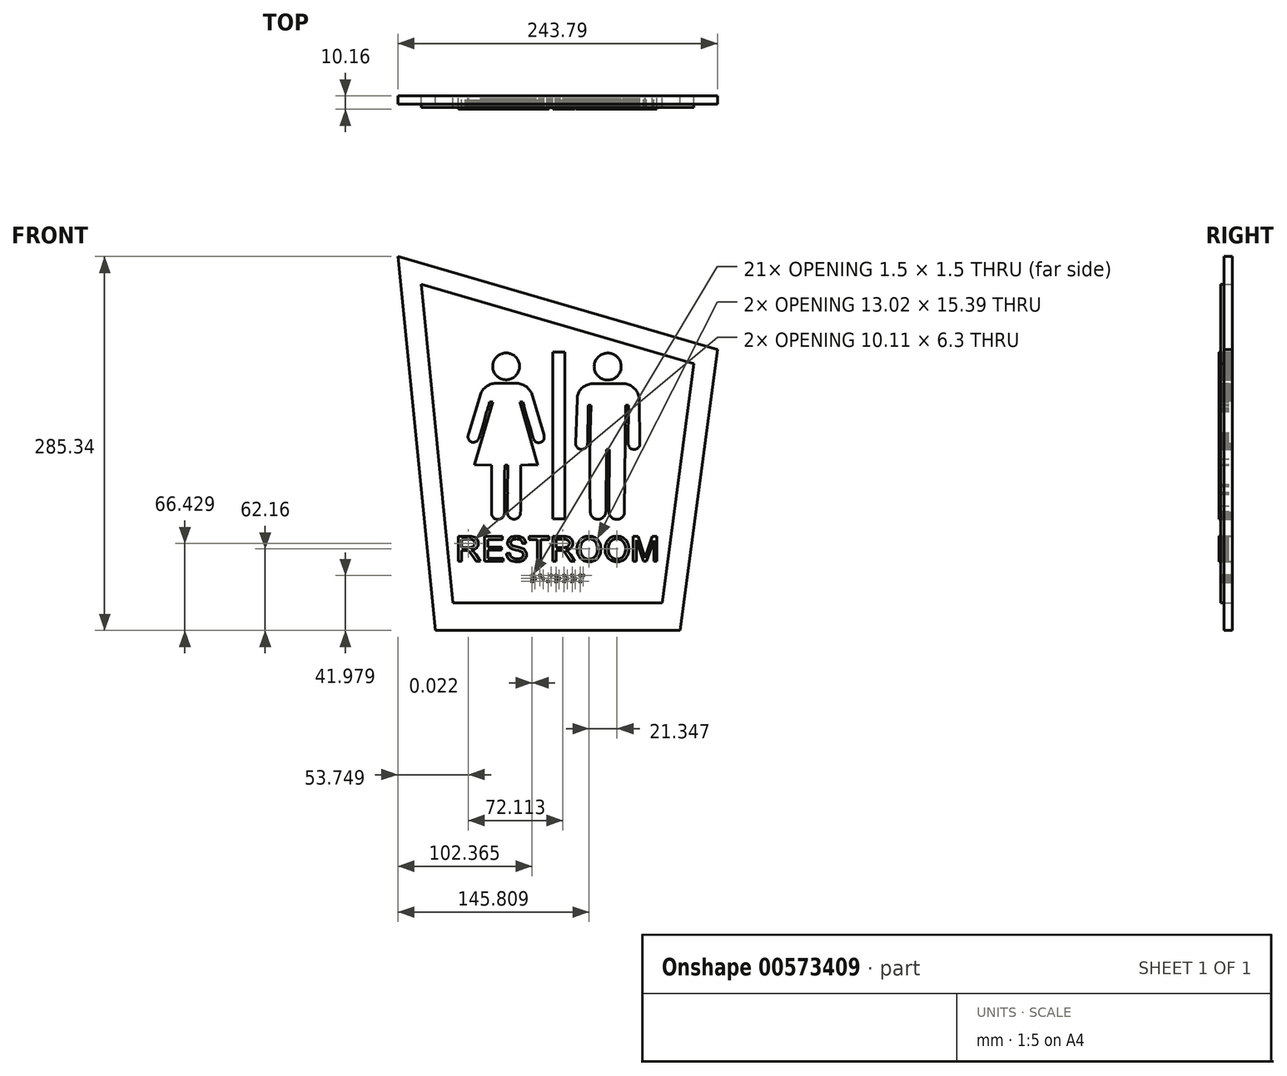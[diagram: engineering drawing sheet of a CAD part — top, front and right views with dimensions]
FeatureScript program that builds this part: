
annotation { "Feature Type Name" : "Feature", "Feature Type Description" : "" }
export const myFeature = defineFeature(function(context is Context, id is Id, definition is map)
    precondition{}
    {
        {
            var Q0;
            Q0=qCreatedBy(makeId("Front.planeOp"),FACE);
            var sketch = newSketch(context, id + "F0", { "sketchPlane" : qUnion([Q0])});
            skLineSegment(sketch, "E0", {"start": v(-172.43, -33.74) * mm, "end": v(-163.18, -33.74) * mm});
            skLineSegment(sketch, "E1", {"start": v(-163.18, -33.74) * mm, "end": v(-163.18, 93.38) * mm});
            skLineSegment(sketch, "E2", {"start": v(-163.18, 93.38) * mm, "end": v(-172.43, 93.38) * mm});
            skLineSegment(sketch, "E3", {"start": v(-172.43, 93.38) * mm, "end": v(-172.43, -33.74) * mm});
            skLineSegment(sketch, "E4", {"start": v(-119.78, 69.44) * mm, "end": v(-142.07, 69.36) * mm});
            skLineSegment(sketch, "E5", {"start": v(-142.07, 69.36) * mm, "end": v(-143.08, 69.24) * mm});
            skLineSegment(sketch, "E6", {"start": v(-143.08, 69.24) * mm, "end": v(-144.08, 69.04) * mm});
            skLineSegment(sketch, "E7", {"start": v(-144.08, 69.04) * mm, "end": v(-145.06, 68.76) * mm});
            skLineSegment(sketch, "E8", {"start": v(-145.06, 68.76) * mm, "end": v(-146.02, 68.41) * mm});
            skLineSegment(sketch, "E9", {"start": v(-146.02, 68.41) * mm, "end": v(-146.95, 68) * mm});
            skLineSegment(sketch, "E10", {"start": v(-146.95, 68) * mm, "end": v(-147.85, 67.5) * mm});
            skLineSegment(sketch, "E11", {"start": v(-147.85, 67.5) * mm, "end": v(-148.7, 66.95) * mm});
            skLineSegment(sketch, "E12", {"start": v(-148.7, 66.95) * mm, "end": v(-149.52, 66.33) * mm});
            skLineSegment(sketch, "E13", {"start": v(-149.52, 66.33) * mm, "end": v(-150.28, 65.66) * mm});
            skLineSegment(sketch, "E14", {"start": v(-150.28, 65.66) * mm, "end": v(-151, 64.92) * mm});
            skLineSegment(sketch, "E15", {"start": v(-151, 64.92) * mm, "end": v(-151.65, 64.14) * mm});
            skLineSegment(sketch, "E16", {"start": v(-151.65, 64.14) * mm, "end": v(-152.25, 63.31) * mm});
            skLineSegment(sketch, "E17", {"start": v(-152.25, 63.31) * mm, "end": v(-152.65, 62.43) * mm});
            skLineSegment(sketch, "E18", {"start": v(-152.65, 62.43) * mm, "end": v(-152.99, 61.51) * mm});
            skLineSegment(sketch, "E19", {"start": v(-152.99, 61.51) * mm, "end": v(-153.26, 60.57) * mm});
            skLineSegment(sketch, "E20", {"start": v(-153.26, 60.57) * mm, "end": v(-153.46, 59.62) * mm});
            skLineSegment(sketch, "E21", {"start": v(-153.46, 59.62) * mm, "end": v(-153.6, 58.65) * mm});
            skLineSegment(sketch, "E22", {"start": v(-153.6, 58.65) * mm, "end": v(-153.65, 57.68) * mm});
            skLineSegment(sketch, "E23", {"start": v(-153.65, 57.68) * mm, "end": v(-154.88, 23.77) * mm});
            skLineSegment(sketch, "E24", {"start": v(-154.88, 23.77) * mm, "end": v(-154.84, 23.18) * mm});
            skLineSegment(sketch, "E25", {"start": v(-154.84, 23.18) * mm, "end": v(-154.73, 22.59) * mm});
            skLineSegment(sketch, "E26", {"start": v(-154.73, 22.59) * mm, "end": v(-154.54, 22.02) * mm});
            skLineSegment(sketch, "E27", {"start": v(-154.54, 22.02) * mm, "end": v(-154.28, 21.48) * mm});
            skLineSegment(sketch, "E28", {"start": v(-154.28, 21.48) * mm, "end": v(-153.95, 20.98) * mm});
            skLineSegment(sketch, "E29", {"start": v(-153.95, 20.98) * mm, "end": v(-153.56, 20.53) * mm});
            skLineSegment(sketch, "E30", {"start": v(-153.56, 20.53) * mm, "end": v(-153.11, 20.14) * mm});
            skLineSegment(sketch, "E31", {"start": v(-153.11, 20.14) * mm, "end": v(-152.61, 19.8) * mm});
            skLineSegment(sketch, "E32", {"start": v(-152.61, 19.8) * mm, "end": v(-152.08, 19.54) * mm});
            skLineSegment(sketch, "E33", {"start": v(-152.08, 19.54) * mm, "end": v(-151.51, 19.34) * mm});
            skLineSegment(sketch, "E34", {"start": v(-151.51, 19.34) * mm, "end": v(-150.93, 19.22) * mm});
            skLineSegment(sketch, "E35", {"start": v(-150.93, 19.22) * mm, "end": v(-150.33, 19.18) * mm});
            skLineSegment(sketch, "E36", {"start": v(-150.33, 19.18) * mm, "end": v(-149.73, 19.22) * mm});
            skLineSegment(sketch, "E37", {"start": v(-149.73, 19.22) * mm, "end": v(-149.15, 19.33) * mm});
            skLineSegment(sketch, "E38", {"start": v(-149.15, 19.33) * mm, "end": v(-148.58, 19.53) * mm});
            skLineSegment(sketch, "E39", {"start": v(-148.58, 19.53) * mm, "end": v(-148.04, 19.8) * mm});
            skLineSegment(sketch, "E40", {"start": v(-148.04, 19.8) * mm, "end": v(-147.54, 20.12) * mm});
            skLineSegment(sketch, "E41", {"start": v(-147.54, 20.12) * mm, "end": v(-147.1, 20.52) * mm});
            skLineSegment(sketch, "E42", {"start": v(-147.1, 20.52) * mm, "end": v(-146.7, 20.97) * mm});
            skLineSegment(sketch, "E43", {"start": v(-146.7, 20.97) * mm, "end": v(-146.37, 21.46) * mm});
            skLineSegment(sketch, "E44", {"start": v(-146.37, 21.46) * mm, "end": v(-146.1, 22) * mm});
            skLineSegment(sketch, "E45", {"start": v(-146.1, 22) * mm, "end": v(-145.91, 22.57) * mm});
            skLineSegment(sketch, "E46", {"start": v(-145.91, 22.57) * mm, "end": v(-145.8, 23.16) * mm});
            skLineSegment(sketch, "E47", {"start": v(-145.8, 23.16) * mm, "end": v(-145.76, 23.75) * mm});
            skLineSegment(sketch, "E48", {"start": v(-145.76, 23.75) * mm, "end": v(-145.43, 52.87) * mm});
            skLineSegment(sketch, "E49", {"start": v(-145.43, 52.87) * mm, "end": v(-143.25, 52.85) * mm});
            skLineSegment(sketch, "E50", {"start": v(-143.25, 52.85) * mm, "end": v(-143.72, 32.37) * mm});
            skLineSegment(sketch, "E51", {"start": v(-143.72, 32.37) * mm, "end": v(-143.99, 11.9) * mm});
            skLineSegment(sketch, "E52", {"start": v(-143.99, 11.9) * mm, "end": v(-143.93, -8.58) * mm});
            skLineSegment(sketch, "E53", {"start": v(-143.93, -8.58) * mm, "end": v(-143.66, -29.05) * mm});
            skLineSegment(sketch, "E54", {"start": v(-143.66, -29.05) * mm, "end": v(-143.56, -29.71) * mm});
            skLineSegment(sketch, "E55", {"start": v(-143.56, -29.71) * mm, "end": v(-143.37, -30.35) * mm});
            skLineSegment(sketch, "E56", {"start": v(-143.37, -30.35) * mm, "end": v(-143.12, -30.97) * mm});
            skLineSegment(sketch, "E57", {"start": v(-143.12, -30.97) * mm, "end": v(-142.8, -31.56) * mm});
            skLineSegment(sketch, "E58", {"start": v(-142.8, -31.56) * mm, "end": v(-142.4, -32.1) * mm});
            skLineSegment(sketch, "E59", {"start": v(-142.4, -32.1) * mm, "end": v(-141.96, -32.6) * mm});
            skLineSegment(sketch, "E60", {"start": v(-141.96, -32.6) * mm, "end": v(-141.46, -33.04) * mm});
            skLineSegment(sketch, "E61", {"start": v(-141.46, -33.04) * mm, "end": v(-140.92, -33.43) * mm});
            skLineSegment(sketch, "E62", {"start": v(-140.92, -33.43) * mm, "end": v(-140.33, -33.75) * mm});
            skLineSegment(sketch, "E63", {"start": v(-140.33, -33.75) * mm, "end": v(-139.71, -34) * mm});
            skLineSegment(sketch, "E64", {"start": v(-139.71, -34) * mm, "end": v(-139.07, -34.18) * mm});
            skLineSegment(sketch, "E65", {"start": v(-139.07, -34.18) * mm, "end": v(-138.4, -34.3) * mm});
            skLineSegment(sketch, "E66", {"start": v(-138.4, -34.3) * mm, "end": v(-137.74, -34.32) * mm});
            skLineSegment(sketch, "E67", {"start": v(-137.74, -34.32) * mm, "end": v(-137.07, -34.28) * mm});
            skLineSegment(sketch, "E68", {"start": v(-137.07, -34.28) * mm, "end": v(-136.42, -34.16) * mm});
            skLineSegment(sketch, "E69", {"start": v(-136.42, -34.16) * mm, "end": v(-135.78, -33.97) * mm});
            skLineSegment(sketch, "E70", {"start": v(-135.78, -33.97) * mm, "end": v(-135.16, -33.7) * mm});
            skLineSegment(sketch, "E71", {"start": v(-135.16, -33.7) * mm, "end": v(-134.58, -33.38) * mm});
            skLineSegment(sketch, "E72", {"start": v(-134.58, -33.38) * mm, "end": v(-134.04, -32.98) * mm});
            skLineSegment(sketch, "E73", {"start": v(-134.04, -32.98) * mm, "end": v(-133.55, -32.53) * mm});
            skLineSegment(sketch, "E74", {"start": v(-133.55, -32.53) * mm, "end": v(-133.11, -32.03) * mm});
            skLineSegment(sketch, "E75", {"start": v(-133.11, -32.03) * mm, "end": v(-132.73, -31.48) * mm});
            skLineSegment(sketch, "E76", {"start": v(-132.73, -31.48) * mm, "end": v(-132.42, -30.89) * mm});
            skLineSegment(sketch, "E77", {"start": v(-132.42, -30.89) * mm, "end": v(-132.18, -30.26) * mm});
            skLineSegment(sketch, "E78", {"start": v(-132.18, -30.26) * mm, "end": v(-132, -29.62) * mm});
            skLineSegment(sketch, "E79", {"start": v(-132, -29.62) * mm, "end": v(-131.9, -28.96) * mm});
            skLineSegment(sketch, "E80", {"start": v(-131.9, -28.96) * mm, "end": v(-131.8, -28.12) * mm});
            skLineSegment(sketch, "E81", {"start": v(-131.8, -28.12) * mm, "end": v(-131.31, 19.01) * mm});
            skLineSegment(sketch, "E82", {"start": v(-131.31, 19.01) * mm, "end": v(-129.15, 19) * mm});
            skLineSegment(sketch, "E83", {"start": v(-129.15, 19) * mm, "end": v(-129.56, -24.14) * mm});
            skLineSegment(sketch, "E84", {"start": v(-129.56, -24.14) * mm, "end": v(-129.37, -29.3) * mm});
            skLineSegment(sketch, "E85", {"start": v(-129.37, -29.3) * mm, "end": v(-129.23, -29.95) * mm});
            skLineSegment(sketch, "E86", {"start": v(-129.23, -29.95) * mm, "end": v(-129.02, -30.58) * mm});
            skLineSegment(sketch, "E87", {"start": v(-129.02, -30.58) * mm, "end": v(-128.73, -31.18) * mm});
            skLineSegment(sketch, "E88", {"start": v(-128.73, -31.18) * mm, "end": v(-128.38, -31.75) * mm});
            skLineSegment(sketch, "E89", {"start": v(-128.38, -31.75) * mm, "end": v(-127.97, -32.27) * mm});
            skLineSegment(sketch, "E90", {"start": v(-127.97, -32.27) * mm, "end": v(-127.5, -32.75) * mm});
            skLineSegment(sketch, "E91", {"start": v(-127.5, -32.75) * mm, "end": v(-126.99, -33.17) * mm});
            skLineSegment(sketch, "E92", {"start": v(-126.99, -33.17) * mm, "end": v(-126.43, -33.52) * mm});
            skLineSegment(sketch, "E93", {"start": v(-126.43, -33.52) * mm, "end": v(-125.83, -33.82) * mm});
            skLineSegment(sketch, "E94", {"start": v(-125.83, -33.82) * mm, "end": v(-125.2, -34.05) * mm});
            skLineSegment(sketch, "E95", {"start": v(-125.2, -34.05) * mm, "end": v(-124.56, -34.2) * mm});
            skLineSegment(sketch, "E96", {"start": v(-124.56, -34.2) * mm, "end": v(-123.9, -34.28) * mm});
            skLineSegment(sketch, "E97", {"start": v(-123.9, -34.28) * mm, "end": v(-123.23, -34.29) * mm});
            skLineSegment(sketch, "E98", {"start": v(-123.23, -34.29) * mm, "end": v(-122.57, -34.22) * mm});
            skLineSegment(sketch, "E99", {"start": v(-122.57, -34.22) * mm, "end": v(-121.92, -34.08) * mm});
            skLineSegment(sketch, "E100", {"start": v(-121.92, -34.08) * mm, "end": v(-121.3, -33.87) * mm});
            skLineSegment(sketch, "E101", {"start": v(-121.3, -33.87) * mm, "end": v(-120.69, -33.59) * mm});
            skLineSegment(sketch, "E102", {"start": v(-120.69, -33.59) * mm, "end": v(-120.12, -33.24) * mm});
            skLineSegment(sketch, "E103", {"start": v(-120.12, -33.24) * mm, "end": v(-119.6, -32.83) * mm});
            skLineSegment(sketch, "E104", {"start": v(-119.6, -32.83) * mm, "end": v(-119.12, -32.37) * mm});
            skLineSegment(sketch, "E105", {"start": v(-119.12, -32.37) * mm, "end": v(-118.7, -31.85) * mm});
            skLineSegment(sketch, "E106", {"start": v(-118.7, -31.85) * mm, "end": v(-118.33, -31.3) * mm});
            skLineSegment(sketch, "E107", {"start": v(-118.33, -31.3) * mm, "end": v(-118.04, -30.7) * mm});
            skLineSegment(sketch, "E108", {"start": v(-118.04, -30.7) * mm, "end": v(-117.8, -30.07) * mm});
            skLineSegment(sketch, "E109", {"start": v(-117.8, -30.07) * mm, "end": v(-117.65, -29.43) * mm});
            skLineSegment(sketch, "E110", {"start": v(-117.65, -29.43) * mm, "end": v(-117.57, -28.77) * mm});
            skLineSegment(sketch, "E111", {"start": v(-117.57, -28.77) * mm, "end": v(-117.56, -28.1) * mm});
            skLineSegment(sketch, "E112", {"start": v(-117.56, -28.1) * mm, "end": v(-116.87, 52.77) * mm});
            skLineSegment(sketch, "E113", {"start": v(-116.87, 52.77) * mm, "end": v(-114.63, 52.77) * mm});
            skLineSegment(sketch, "E114", {"start": v(-114.63, 52.77) * mm, "end": v(-114.74, 23.45) * mm});
            skLineSegment(sketch, "E115", {"start": v(-114.74, 23.45) * mm, "end": v(-114.72, 23.1) * mm});
            skLineSegment(sketch, "E116", {"start": v(-114.72, 23.1) * mm, "end": v(-114.67, 22.74) * mm});
            skLineSegment(sketch, "E117", {"start": v(-114.67, 22.74) * mm, "end": v(-114.54, 22.17) * mm});
            skLineSegment(sketch, "E118", {"start": v(-114.54, 22.17) * mm, "end": v(-114.33, 21.63) * mm});
            skLineSegment(sketch, "E119", {"start": v(-114.33, 21.63) * mm, "end": v(-114.04, 21.11) * mm});
            skLineSegment(sketch, "E120", {"start": v(-114.04, 21.11) * mm, "end": v(-113.7, 20.64) * mm});
            skLineSegment(sketch, "E121", {"start": v(-113.7, 20.64) * mm, "end": v(-113.3, 20.22) * mm});
            skLineSegment(sketch, "E122", {"start": v(-113.3, 20.22) * mm, "end": v(-112.84, 19.85) * mm});
            skLineSegment(sketch, "E123", {"start": v(-112.84, 19.85) * mm, "end": v(-112.33, 19.55) * mm});
            skLineSegment(sketch, "E124", {"start": v(-112.33, 19.55) * mm, "end": v(-111.8, 19.31) * mm});
            skLineSegment(sketch, "E125", {"start": v(-111.8, 19.31) * mm, "end": v(-111.24, 19.15) * mm});
            skLineSegment(sketch, "E126", {"start": v(-111.24, 19.15) * mm, "end": v(-110.66, 19.06) * mm});
            skLineSegment(sketch, "E127", {"start": v(-110.66, 19.06) * mm, "end": v(-110.07, 19.05) * mm});
            skLineSegment(sketch, "E128", {"start": v(-110.07, 19.05) * mm, "end": v(-109.49, 19.12) * mm});
            skLineSegment(sketch, "E129", {"start": v(-109.49, 19.12) * mm, "end": v(-108.92, 19.26) * mm});
            skLineSegment(sketch, "E130", {"start": v(-108.92, 19.26) * mm, "end": v(-108.37, 19.48) * mm});
            skLineSegment(sketch, "E131", {"start": v(-108.37, 19.48) * mm, "end": v(-107.86, 19.76) * mm});
            skLineSegment(sketch, "E132", {"start": v(-107.86, 19.76) * mm, "end": v(-107.4, 20.11) * mm});
            skLineSegment(sketch, "E133", {"start": v(-107.4, 20.11) * mm, "end": v(-106.97, 20.52) * mm});
            skLineSegment(sketch, "E134", {"start": v(-106.97, 20.52) * mm, "end": v(-106.61, 20.98) * mm});
            skLineSegment(sketch, "E135", {"start": v(-106.61, 20.98) * mm, "end": v(-106.31, 21.48) * mm});
            skLineSegment(sketch, "E136", {"start": v(-106.31, 21.48) * mm, "end": v(-106.08, 22.02) * mm});
            skLineSegment(sketch, "E137", {"start": v(-106.08, 22.02) * mm, "end": v(-105.92, 22.59) * mm});
            skLineSegment(sketch, "E138", {"start": v(-105.92, 22.59) * mm, "end": v(-105.84, 23.17) * mm});
            skLineSegment(sketch, "E139", {"start": v(-105.84, 23.17) * mm, "end": v(-105.83, 23.75) * mm});
            skLineSegment(sketch, "E140", {"start": v(-105.83, 23.75) * mm, "end": v(-106.14, 56.43) * mm});
            skLineSegment(sketch, "E141", {"start": v(-106.14, 56.43) * mm, "end": v(-106.16, 56.95) * mm});
            skLineSegment(sketch, "E142", {"start": v(-106.16, 56.95) * mm, "end": v(-106.2, 57.47) * mm});
            skLineSegment(sketch, "E143", {"start": v(-106.2, 57.47) * mm, "end": v(-106.26, 58) * mm});
            skLineSegment(sketch, "E144", {"start": v(-106.26, 58) * mm, "end": v(-106.34, 58.51) * mm});
            skLineSegment(sketch, "E145", {"start": v(-106.34, 58.51) * mm, "end": v(-106.55, 59.49) * mm});
            skLineSegment(sketch, "E146", {"start": v(-106.55, 59.49) * mm, "end": v(-106.83, 60.44) * mm});
            skLineSegment(sketch, "E147", {"start": v(-106.83, 60.44) * mm, "end": v(-107.18, 61.37) * mm});
            skLineSegment(sketch, "E148", {"start": v(-107.18, 61.37) * mm, "end": v(-107.6, 62.27) * mm});
            skLineSegment(sketch, "E149", {"start": v(-107.6, 62.27) * mm, "end": v(-108.09, 63.14) * mm});
            skLineSegment(sketch, "E150", {"start": v(-108.09, 63.14) * mm, "end": v(-108.64, 63.96) * mm});
            skLineSegment(sketch, "E151", {"start": v(-108.64, 63.96) * mm, "end": v(-109.25, 64.75) * mm});
            skLineSegment(sketch, "E152", {"start": v(-109.25, 64.75) * mm, "end": v(-109.92, 65.48) * mm});
            skLineSegment(sketch, "E153", {"start": v(-109.92, 65.48) * mm, "end": v(-110.64, 66.17) * mm});
            skLineSegment(sketch, "E154", {"start": v(-110.64, 66.17) * mm, "end": v(-111.41, 66.8) * mm});
            skLineSegment(sketch, "E155", {"start": v(-111.41, 66.8) * mm, "end": v(-112.23, 67.36) * mm});
            skLineSegment(sketch, "E156", {"start": v(-112.23, 67.36) * mm, "end": v(-113.09, 67.86) * mm});
            skLineSegment(sketch, "E157", {"start": v(-113.09, 67.86) * mm, "end": v(-113.98, 68.3) * mm});
            skLineSegment(sketch, "E158", {"start": v(-113.98, 68.3) * mm, "end": v(-114.9, 68.67) * mm});
            skLineSegment(sketch, "E159", {"start": v(-114.9, 68.67) * mm, "end": v(-115.85, 68.97) * mm});
            skLineSegment(sketch, "E160", {"start": v(-115.85, 68.97) * mm, "end": v(-116.82, 69.2) * mm});
            skLineSegment(sketch, "E161", {"start": v(-116.82, 69.2) * mm, "end": v(-117.8, 69.36) * mm});
            skLineSegment(sketch, "E162", {"start": v(-117.8, 69.36) * mm, "end": v(-118.79, 69.44) * mm});
            skLineSegment(sketch, "E163", {"start": v(-118.79, 69.44) * mm, "end": v(-119.78, 69.44) * mm});
            skLineSegment(sketch, "E164", {"start": v(-140.72, 82.37) * mm, "end": v(-140.7, 81.57) * mm});
            skLineSegment(sketch, "E165", {"start": v(-140.7, 81.57) * mm, "end": v(-140.6, 80.77) * mm});
            skLineSegment(sketch, "E166", {"start": v(-140.6, 80.77) * mm, "end": v(-140.43, 79.9) * mm});
            skLineSegment(sketch, "E167", {"start": v(-140.43, 79.9) * mm, "end": v(-140.17, 79.03) * mm});
            skLineSegment(sketch, "E168", {"start": v(-140.17, 79.03) * mm, "end": v(-139.85, 78.19) * mm});
            skLineSegment(sketch, "E169", {"start": v(-139.85, 78.19) * mm, "end": v(-139.45, 77.38) * mm});
            skLineSegment(sketch, "E170", {"start": v(-139.45, 77.38) * mm, "end": v(-138.98, 76.6) * mm});
            skLineSegment(sketch, "E171", {"start": v(-138.98, 76.6) * mm, "end": v(-138.45, 75.88) * mm});
            skLineSegment(sketch, "E172", {"start": v(-138.45, 75.88) * mm, "end": v(-137.86, 75.2) * mm});
            skLineSegment(sketch, "E173", {"start": v(-137.86, 75.2) * mm, "end": v(-137.2, 74.58) * mm});
            skLineSegment(sketch, "E174", {"start": v(-137.2, 74.58) * mm, "end": v(-136.5, 74.02) * mm});
            skLineSegment(sketch, "E175", {"start": v(-136.5, 74.02) * mm, "end": v(-135.76, 73.52) * mm});
            skLineSegment(sketch, "E176", {"start": v(-135.76, 73.52) * mm, "end": v(-134.97, 73.08) * mm});
            skLineSegment(sketch, "E177", {"start": v(-134.97, 73.08) * mm, "end": v(-134.15, 72.72) * mm});
            skLineSegment(sketch, "E178", {"start": v(-134.15, 72.72) * mm, "end": v(-133.3, 72.43) * mm});
            skLineSegment(sketch, "E179", {"start": v(-133.3, 72.43) * mm, "end": v(-132.42, 72.21) * mm});
            skLineSegment(sketch, "E180", {"start": v(-132.42, 72.21) * mm, "end": v(-131.53, 72.08) * mm});
            skLineSegment(sketch, "E181", {"start": v(-131.53, 72.08) * mm, "end": v(-130.63, 72.02) * mm});
            skLineSegment(sketch, "E182", {"start": v(-130.63, 72.02) * mm, "end": v(-129.73, 72.04) * mm});
            skLineSegment(sketch, "E183", {"start": v(-129.73, 72.04) * mm, "end": v(-128.84, 72.13) * mm});
            skLineSegment(sketch, "E184", {"start": v(-128.84, 72.13) * mm, "end": v(-127.95, 72.3) * mm});
            skLineSegment(sketch, "E185", {"start": v(-127.95, 72.3) * mm, "end": v(-127.09, 72.56) * mm});
            skLineSegment(sketch, "E186", {"start": v(-127.09, 72.56) * mm, "end": v(-126.25, 72.89) * mm});
            skLineSegment(sketch, "E187", {"start": v(-126.25, 72.89) * mm, "end": v(-125.44, 73.28) * mm});
            skLineSegment(sketch, "E188", {"start": v(-125.44, 73.28) * mm, "end": v(-124.67, 73.75) * mm});
            skLineSegment(sketch, "E189", {"start": v(-124.67, 73.75) * mm, "end": v(-123.97, 74.26) * mm});
            skLineSegment(sketch, "E190", {"start": v(-123.97, 74.26) * mm, "end": v(-123.31, 74.83) * mm});
            skLineSegment(sketch, "E191", {"start": v(-123.31, 74.83) * mm, "end": v(-122.7, 75.46) * mm});
            skLineSegment(sketch, "E192", {"start": v(-122.7, 75.46) * mm, "end": v(-122.16, 76.13) * mm});
            skLineSegment(sketch, "E193", {"start": v(-122.16, 76.13) * mm, "end": v(-121.66, 76.84) * mm});
            skLineSegment(sketch, "E194", {"start": v(-121.66, 76.84) * mm, "end": v(-121.23, 77.6) * mm});
            skLineSegment(sketch, "E195", {"start": v(-121.23, 77.6) * mm, "end": v(-120.87, 78.39) * mm});
            skLineSegment(sketch, "E196", {"start": v(-120.87, 78.39) * mm, "end": v(-120.57, 79.2) * mm});
            skLineSegment(sketch, "E197", {"start": v(-120.57, 79.2) * mm, "end": v(-120.34, 80.04) * mm});
            skLineSegment(sketch, "E198", {"start": v(-120.34, 80.04) * mm, "end": v(-120.18, 80.9) * mm});
            skLineSegment(sketch, "E199", {"start": v(-120.18, 80.9) * mm, "end": v(-120.1, 81.76) * mm});
            skLineSegment(sketch, "E200", {"start": v(-120.1, 81.76) * mm, "end": v(-120.08, 82.56) * mm});
            skLineSegment(sketch, "E201", {"start": v(-120.08, 82.56) * mm, "end": v(-120.13, 83.36) * mm});
            skLineSegment(sketch, "E202", {"start": v(-120.13, 83.36) * mm, "end": v(-120.24, 84.17) * mm});
            skLineSegment(sketch, "E203", {"start": v(-120.24, 84.17) * mm, "end": v(-120.42, 84.98) * mm});
            skLineSegment(sketch, "E204", {"start": v(-120.42, 84.98) * mm, "end": v(-120.66, 85.77) * mm});
            skLineSegment(sketch, "E205", {"start": v(-120.66, 85.77) * mm, "end": v(-120.97, 86.53) * mm});
            skLineSegment(sketch, "E206", {"start": v(-120.97, 86.53) * mm, "end": v(-121.33, 87.27) * mm});
            skLineSegment(sketch, "E207", {"start": v(-121.33, 87.27) * mm, "end": v(-121.76, 87.98) * mm});
            skLineSegment(sketch, "E208", {"start": v(-121.76, 87.98) * mm, "end": v(-122.24, 88.66) * mm});
            skLineSegment(sketch, "E209", {"start": v(-122.24, 88.66) * mm, "end": v(-122.77, 89.3) * mm});
            skLineSegment(sketch, "E210", {"start": v(-122.77, 89.3) * mm, "end": v(-123.35, 89.88) * mm});
            skLineSegment(sketch, "E211", {"start": v(-123.35, 89.88) * mm, "end": v(-123.97, 90.42) * mm});
            skLineSegment(sketch, "E212", {"start": v(-123.97, 90.42) * mm, "end": v(-124.7, 90.95) * mm});
            skLineSegment(sketch, "E213", {"start": v(-124.7, 90.95) * mm, "end": v(-125.47, 91.41) * mm});
            skLineSegment(sketch, "E214", {"start": v(-125.47, 91.41) * mm, "end": v(-126.28, 91.8) * mm});
            skLineSegment(sketch, "E215", {"start": v(-126.28, 91.8) * mm, "end": v(-127.12, 92.13) * mm});
            skLineSegment(sketch, "E216", {"start": v(-127.12, 92.13) * mm, "end": v(-127.99, 92.38) * mm});
            skLineSegment(sketch, "E217", {"start": v(-127.99, 92.38) * mm, "end": v(-128.87, 92.55) * mm});
            skLineSegment(sketch, "E218", {"start": v(-128.87, 92.55) * mm, "end": v(-129.77, 92.65) * mm});
            skLineSegment(sketch, "E219", {"start": v(-129.77, 92.65) * mm, "end": v(-130.67, 92.66) * mm});
            skLineSegment(sketch, "E220", {"start": v(-130.67, 92.66) * mm, "end": v(-131.57, 92.6) * mm});
            skLineSegment(sketch, "E221", {"start": v(-131.57, 92.6) * mm, "end": v(-132.46, 92.46) * mm});
            skLineSegment(sketch, "E222", {"start": v(-132.46, 92.46) * mm, "end": v(-133.33, 92.24) * mm});
            skLineSegment(sketch, "E223", {"start": v(-133.33, 92.24) * mm, "end": v(-134.19, 91.95) * mm});
            skLineSegment(sketch, "E224", {"start": v(-134.19, 91.95) * mm, "end": v(-135, 91.58) * mm});
            skLineSegment(sketch, "E225", {"start": v(-135, 91.58) * mm, "end": v(-135.8, 91.14) * mm});
            skLineSegment(sketch, "E226", {"start": v(-135.8, 91.14) * mm, "end": v(-136.54, 90.64) * mm});
            skLineSegment(sketch, "E227", {"start": v(-136.54, 90.64) * mm, "end": v(-137.24, 90.07) * mm});
            skLineSegment(sketch, "E228", {"start": v(-137.24, 90.07) * mm, "end": v(-137.9, 89.44) * mm});
            skLineSegment(sketch, "E229", {"start": v(-137.9, 89.44) * mm, "end": v(-138.48, 88.76) * mm});
            skLineSegment(sketch, "E230", {"start": v(-138.48, 88.76) * mm, "end": v(-139.01, 88.03) * mm});
            skLineSegment(sketch, "E231", {"start": v(-139.01, 88.03) * mm, "end": v(-139.47, 87.26) * mm});
            skLineSegment(sketch, "E232", {"start": v(-139.47, 87.26) * mm, "end": v(-139.87, 86.45) * mm});
            skLineSegment(sketch, "E233", {"start": v(-139.87, 86.45) * mm, "end": v(-140.19, 85.6) * mm});
            skLineSegment(sketch, "E234", {"start": v(-140.19, 85.6) * mm, "end": v(-140.42, 84.82) * mm});
            skLineSegment(sketch, "E235", {"start": v(-140.42, 84.82) * mm, "end": v(-140.58, 84) * mm});
            skLineSegment(sketch, "E236", {"start": v(-140.58, 84) * mm, "end": v(-140.68, 83.2) * mm});
            skLineSegment(sketch, "E237", {"start": v(-140.68, 83.2) * mm, "end": v(-140.72, 82.37) * mm});
            skLineSegment(sketch, "E238", {"start": v(-215.65, 69.67) * mm, "end": v(-216.63, 69.6) * mm});
            skLineSegment(sketch, "E239", {"start": v(-216.63, 69.6) * mm, "end": v(-217.6, 69.44) * mm});
            skLineSegment(sketch, "E240", {"start": v(-217.6, 69.44) * mm, "end": v(-218.56, 69.21) * mm});
            skLineSegment(sketch, "E241", {"start": v(-218.56, 69.21) * mm, "end": v(-219.5, 68.92) * mm});
            skLineSegment(sketch, "E242", {"start": v(-219.5, 68.92) * mm, "end": v(-220.42, 68.56) * mm});
            skLineSegment(sketch, "E243", {"start": v(-220.42, 68.56) * mm, "end": v(-221.3, 68.13) * mm});
            skLineSegment(sketch, "E244", {"start": v(-221.3, 68.13) * mm, "end": v(-222.16, 67.64) * mm});
            skLineSegment(sketch, "E245", {"start": v(-222.16, 67.64) * mm, "end": v(-222.98, 67.09) * mm});
            skLineSegment(sketch, "E246", {"start": v(-222.98, 67.09) * mm, "end": v(-223.75, 66.48) * mm});
            skLineSegment(sketch, "E247", {"start": v(-223.75, 66.48) * mm, "end": v(-224.48, 65.82) * mm});
            skLineSegment(sketch, "E248", {"start": v(-224.48, 65.82) * mm, "end": v(-225.16, 65.1) * mm});
            skLineSegment(sketch, "E249", {"start": v(-225.16, 65.1) * mm, "end": v(-225.78, 64.34) * mm});
            skLineSegment(sketch, "E250", {"start": v(-225.78, 64.34) * mm, "end": v(-226.35, 63.53) * mm});
            skLineSegment(sketch, "E251", {"start": v(-226.35, 63.53) * mm, "end": v(-226.86, 62.69) * mm});
            skLineSegment(sketch, "E252", {"start": v(-226.86, 62.69) * mm, "end": v(-227.3, 61.8) * mm});
            skLineSegment(sketch, "E253", {"start": v(-227.3, 61.8) * mm, "end": v(-236.47, 31.18) * mm});
            skLineSegment(sketch, "E254", {"start": v(-236.47, 31.18) * mm, "end": v(-236.7, 30.52) * mm});
            skLineSegment(sketch, "E255", {"start": v(-236.7, 30.52) * mm, "end": v(-236.85, 29.84) * mm});
            skLineSegment(sketch, "E256", {"start": v(-236.85, 29.84) * mm, "end": v(-236.93, 29.15) * mm});
            skLineSegment(sketch, "E257", {"start": v(-236.93, 29.15) * mm, "end": v(-236.94, 28.46) * mm});
            skLineSegment(sketch, "E258", {"start": v(-236.94, 28.46) * mm, "end": v(-236.88, 27.76) * mm});
            skLineSegment(sketch, "E259", {"start": v(-236.88, 27.76) * mm, "end": v(-236.72, 27.22) * mm});
            skLineSegment(sketch, "E260", {"start": v(-236.72, 27.22) * mm, "end": v(-236.5, 26.7) * mm});
            skLineSegment(sketch, "E261", {"start": v(-236.5, 26.7) * mm, "end": v(-236.2, 26.22) * mm});
            skLineSegment(sketch, "E262", {"start": v(-236.2, 26.22) * mm, "end": v(-235.83, 25.79) * mm});
            skLineSegment(sketch, "E263", {"start": v(-235.83, 25.79) * mm, "end": v(-235.41, 25.4) * mm});
            skLineSegment(sketch, "E264", {"start": v(-235.41, 25.4) * mm, "end": v(-234.95, 25.09) * mm});
            skLineSegment(sketch, "E265", {"start": v(-234.95, 25.09) * mm, "end": v(-234.44, 24.84) * mm});
            skLineSegment(sketch, "E266", {"start": v(-234.44, 24.84) * mm, "end": v(-233.9, 24.66) * mm});
            skLineSegment(sketch, "E267", {"start": v(-233.9, 24.66) * mm, "end": v(-233.35, 24.55) * mm});
            skLineSegment(sketch, "E268", {"start": v(-233.35, 24.55) * mm, "end": v(-232.78, 24.53) * mm});
            skLineSegment(sketch, "E269", {"start": v(-232.78, 24.53) * mm, "end": v(-232.22, 24.58) * mm});
            skLineSegment(sketch, "E270", {"start": v(-232.22, 24.58) * mm, "end": v(-231.67, 24.7) * mm});
            skLineSegment(sketch, "E271", {"start": v(-231.67, 24.7) * mm, "end": v(-231.14, 24.91) * mm});
            skLineSegment(sketch, "E272", {"start": v(-231.14, 24.91) * mm, "end": v(-230.65, 25.19) * mm});
            skLineSegment(sketch, "E273", {"start": v(-230.65, 25.19) * mm, "end": v(-230.2, 25.53) * mm});
            skLineSegment(sketch, "E274", {"start": v(-230.2, 25.53) * mm, "end": v(-229.8, 25.9) * mm});
            skLineSegment(sketch, "E275", {"start": v(-229.8, 25.9) * mm, "end": v(-229.46, 26.3) * mm});
            skLineSegment(sketch, "E276", {"start": v(-229.46, 26.3) * mm, "end": v(-229.17, 26.76) * mm});
            skLineSegment(sketch, "E277", {"start": v(-229.17, 26.76) * mm, "end": v(-228.93, 27.24) * mm});
            skLineSegment(sketch, "E278", {"start": v(-228.93, 27.24) * mm, "end": v(-228.59, 28.13) * mm});
            skLineSegment(sketch, "E279", {"start": v(-228.59, 28.13) * mm, "end": v(-228.26, 29.04) * mm});
            skLineSegment(sketch, "E280", {"start": v(-228.26, 29.04) * mm, "end": v(-227.92, 30.09) * mm});
            skLineSegment(sketch, "E281", {"start": v(-227.92, 30.09) * mm, "end": v(-227.68, 30.87) * mm});
            skLineSegment(sketch, "E282", {"start": v(-227.68, 30.87) * mm, "end": v(-227.35, 31.98) * mm});
            skLineSegment(sketch, "E283", {"start": v(-227.35, 31.98) * mm, "end": v(-225.14, 39.4) * mm});
            skLineSegment(sketch, "E284", {"start": v(-225.14, 39.4) * mm, "end": v(-222.61, 47.94) * mm});
            skLineSegment(sketch, "E285", {"start": v(-222.61, 47.94) * mm, "end": v(-222.2, 49.44) * mm});
            skLineSegment(sketch, "E286", {"start": v(-222.2, 49.44) * mm, "end": v(-221.78, 50.92) * mm});
            skLineSegment(sketch, "E287", {"start": v(-221.78, 50.92) * mm, "end": v(-221.33, 52.4) * mm});
            skLineSegment(sketch, "E288", {"start": v(-221.33, 52.4) * mm, "end": v(-220.86, 53.88) * mm});
            skLineSegment(sketch, "E289", {"start": v(-220.86, 53.88) * mm, "end": v(-220.48, 55.23) * mm});
            skLineSegment(sketch, "E290", {"start": v(-220.48, 55.23) * mm, "end": v(-219.2, 55.23) * mm});
            skLineSegment(sketch, "E291", {"start": v(-219.2, 55.23) * mm, "end": v(-218.93, 55.2) * mm});
            skLineSegment(sketch, "E292", {"start": v(-218.93, 55.2) * mm, "end": v(-218.67, 55.2) * mm});
            skLineSegment(sketch, "E293", {"start": v(-218.67, 55.2) * mm, "end": v(-218.4, 55.2) * mm});
            skLineSegment(sketch, "E294", {"start": v(-218.4, 55.2) * mm, "end": v(-218.15, 55.23) * mm});
            skLineSegment(sketch, "E295", {"start": v(-218.15, 55.23) * mm, "end": v(-231.99, 7.54) * mm});
            skLineSegment(sketch, "E296", {"start": v(-231.99, 7.54) * mm, "end": v(-232.03, 7.34) * mm});
            skLineSegment(sketch, "E297", {"start": v(-232.03, 7.34) * mm, "end": v(-231.62, 7.27) * mm});
            skLineSegment(sketch, "E298", {"start": v(-231.62, 7.27) * mm, "end": v(-231.5, 7.27) * mm});
            skLineSegment(sketch, "E299", {"start": v(-231.5, 7.27) * mm, "end": v(-231.36, 7.26) * mm});
            skLineSegment(sketch, "E300", {"start": v(-231.36, 7.26) * mm, "end": v(-230.97, 7.26) * mm});
            skLineSegment(sketch, "E301", {"start": v(-230.97, 7.26) * mm, "end": v(-230.26, 7.25) * mm});
            skLineSegment(sketch, "E302", {"start": v(-230.26, 7.25) * mm, "end": v(-219.05, 7.22) * mm});
            skLineSegment(sketch, "E303", {"start": v(-219.05, 7.22) * mm, "end": v(-219.11, -28.37) * mm});
            skLineSegment(sketch, "E304", {"start": v(-219.11, -28.37) * mm, "end": v(-219.11, -28.68) * mm});
            skLineSegment(sketch, "E305", {"start": v(-219.11, -28.68) * mm, "end": v(-219.11, -28.9) * mm});
            skLineSegment(sketch, "E306", {"start": v(-219.11, -28.9) * mm, "end": v(-219.1, -29.25) * mm});
            skLineSegment(sketch, "E307", {"start": v(-219.1, -29.25) * mm, "end": v(-219.08, -29.59) * mm});
            skLineSegment(sketch, "E308", {"start": v(-219.08, -29.59) * mm, "end": v(-219.05, -29.89) * mm});
            skLineSegment(sketch, "E309", {"start": v(-219.05, -29.89) * mm, "end": v(-218.98, -30.34) * mm});
            skLineSegment(sketch, "E310", {"start": v(-218.98, -30.34) * mm, "end": v(-218.89, -30.79) * mm});
            skLineSegment(sketch, "E311", {"start": v(-218.89, -30.79) * mm, "end": v(-218.7, -31.33) * mm});
            skLineSegment(sketch, "E312", {"start": v(-218.7, -31.33) * mm, "end": v(-218.46, -31.84) * mm});
            skLineSegment(sketch, "E313", {"start": v(-218.46, -31.84) * mm, "end": v(-218.15, -32.33) * mm});
            skLineSegment(sketch, "E314", {"start": v(-218.15, -32.33) * mm, "end": v(-217.79, -32.77) * mm});
            skLineSegment(sketch, "E315", {"start": v(-217.79, -32.77) * mm, "end": v(-217.37, -33.16) * mm});
            skLineSegment(sketch, "E316", {"start": v(-217.37, -33.16) * mm, "end": v(-216.91, -33.5) * mm});
            skLineSegment(sketch, "E317", {"start": v(-216.91, -33.5) * mm, "end": v(-216.42, -33.79) * mm});
            skLineSegment(sketch, "E318", {"start": v(-216.42, -33.79) * mm, "end": v(-215.9, -34) * mm});
            skLineSegment(sketch, "E319", {"start": v(-215.9, -34) * mm, "end": v(-215.34, -34.16) * mm});
            skLineSegment(sketch, "E320", {"start": v(-215.34, -34.16) * mm, "end": v(-214.78, -34.25) * mm});
            skLineSegment(sketch, "E321", {"start": v(-214.78, -34.25) * mm, "end": v(-214.2, -34.28) * mm});
            skLineSegment(sketch, "E322", {"start": v(-214.2, -34.28) * mm, "end": v(-213.64, -34.23) * mm});
            skLineSegment(sketch, "E323", {"start": v(-213.64, -34.23) * mm, "end": v(-213.1, -34.13) * mm});
            skLineSegment(sketch, "E324", {"start": v(-213.1, -34.13) * mm, "end": v(-212.56, -33.97) * mm});
            skLineSegment(sketch, "E325", {"start": v(-212.56, -33.97) * mm, "end": v(-212.05, -33.76) * mm});
            skLineSegment(sketch, "E326", {"start": v(-212.05, -33.76) * mm, "end": v(-211.57, -33.48) * mm});
            skLineSegment(sketch, "E327", {"start": v(-211.57, -33.48) * mm, "end": v(-211.13, -33.22) * mm});
            skLineSegment(sketch, "E328", {"start": v(-211.13, -33.22) * mm, "end": v(-210.73, -32.9) * mm});
            skLineSegment(sketch, "E329", {"start": v(-210.73, -32.9) * mm, "end": v(-210.37, -32.54) * mm});
            skLineSegment(sketch, "E330", {"start": v(-210.37, -32.54) * mm, "end": v(-210.06, -32.13) * mm});
            skLineSegment(sketch, "E331", {"start": v(-210.06, -32.13) * mm, "end": v(-209.8, -31.68) * mm});
            skLineSegment(sketch, "E332", {"start": v(-209.8, -31.68) * mm, "end": v(-209.61, -31.21) * mm});
            skLineSegment(sketch, "E333", {"start": v(-209.61, -31.21) * mm, "end": v(-209.54, -31.01) * mm});
            skLineSegment(sketch, "E334", {"start": v(-209.54, -31.01) * mm, "end": v(-209.43, -30.72) * mm});
            skLineSegment(sketch, "E335", {"start": v(-209.43, -30.72) * mm, "end": v(-209.33, -30.41) * mm});
            skLineSegment(sketch, "E336", {"start": v(-209.33, -30.41) * mm, "end": v(-209.29, -30.2) * mm});
            skLineSegment(sketch, "E337", {"start": v(-209.29, -30.2) * mm, "end": v(-209.23, -29.9) * mm});
            skLineSegment(sketch, "E338", {"start": v(-209.23, -29.9) * mm, "end": v(-209.2, -29.58) * mm});
            skLineSegment(sketch, "E339", {"start": v(-209.2, -29.58) * mm, "end": v(-209.16, -29.38) * mm});
            skLineSegment(sketch, "E340", {"start": v(-209.16, -29.38) * mm, "end": v(-209.13, -29.17) * mm});
            skLineSegment(sketch, "E341", {"start": v(-209.13, -29.17) * mm, "end": v(-209.11, -28.96) * mm});
            skLineSegment(sketch, "E342", {"start": v(-209.11, -28.96) * mm, "end": v(-209.11, -28.76) * mm});
            skLineSegment(sketch, "E343", {"start": v(-209.11, -28.76) * mm, "end": v(-209.1, -8.98) * mm});
            skLineSegment(sketch, "E344", {"start": v(-209.1, -8.98) * mm, "end": v(-209.07, -8.65) * mm});
            skLineSegment(sketch, "E345", {"start": v(-209.07, -8.65) * mm, "end": v(-209.04, -7.98) * mm});
            skLineSegment(sketch, "E346", {"start": v(-209.04, -7.98) * mm, "end": v(-209.03, -7.65) * mm});
            skLineSegment(sketch, "E347", {"start": v(-209.03, -7.65) * mm, "end": v(-209, -0.26) * mm});
            skLineSegment(sketch, "E348", {"start": v(-209, -0.26) * mm, "end": v(-208.93, 7.12) * mm});
            skLineSegment(sketch, "E349", {"start": v(-208.93, 7.12) * mm, "end": v(-206.68, 7.14) * mm});
            skLineSegment(sketch, "E350", {"start": v(-206.68, 7.14) * mm, "end": v(-206.74, -13.44) * mm});
            skLineSegment(sketch, "E351", {"start": v(-206.74, -13.44) * mm, "end": v(-206.72, -13.9) * mm});
            skLineSegment(sketch, "E352", {"start": v(-206.72, -13.9) * mm, "end": v(-206.72, -14.35) * mm});
            skLineSegment(sketch, "E353", {"start": v(-206.72, -14.35) * mm, "end": v(-206.74, -14.8) * mm});
            skLineSegment(sketch, "E354", {"start": v(-206.74, -14.8) * mm, "end": v(-206.78, -15.25) * mm});
            skLineSegment(sketch, "E355", {"start": v(-206.78, -15.25) * mm, "end": v(-206.82, -28.63) * mm});
            skLineSegment(sketch, "E356", {"start": v(-206.82, -28.63) * mm, "end": v(-206.82, -28.93) * mm});
            skLineSegment(sketch, "E357", {"start": v(-206.82, -28.93) * mm, "end": v(-206.81, -29.16) * mm});
            skLineSegment(sketch, "E358", {"start": v(-206.81, -29.16) * mm, "end": v(-206.8, -29.5) * mm});
            skLineSegment(sketch, "E359", {"start": v(-206.8, -29.5) * mm, "end": v(-206.76, -29.83) * mm});
            skLineSegment(sketch, "E360", {"start": v(-206.76, -29.83) * mm, "end": v(-206.7, -30.12) * mm});
            skLineSegment(sketch, "E361", {"start": v(-206.7, -30.12) * mm, "end": v(-206.66, -30.34) * mm});
            skLineSegment(sketch, "E362", {"start": v(-206.66, -30.34) * mm, "end": v(-206.57, -30.66) * mm});
            skLineSegment(sketch, "E363", {"start": v(-206.57, -30.66) * mm, "end": v(-206.48, -30.99) * mm});
            skLineSegment(sketch, "E364", {"start": v(-206.48, -30.99) * mm, "end": v(-206.2, -31.53) * mm});
            skLineSegment(sketch, "E365", {"start": v(-206.2, -31.53) * mm, "end": v(-205.88, -32.03) * mm});
            skLineSegment(sketch, "E366", {"start": v(-205.88, -32.03) * mm, "end": v(-205.5, -32.5) * mm});
            skLineSegment(sketch, "E367", {"start": v(-205.5, -32.5) * mm, "end": v(-205.08, -32.93) * mm});
            skLineSegment(sketch, "E368", {"start": v(-205.08, -32.93) * mm, "end": v(-204.6, -33.3) * mm});
            skLineSegment(sketch, "E369", {"start": v(-204.6, -33.3) * mm, "end": v(-204.1, -33.62) * mm});
            skLineSegment(sketch, "E370", {"start": v(-204.1, -33.62) * mm, "end": v(-203.78, -33.76) * mm});
            skLineSegment(sketch, "E371", {"start": v(-203.78, -33.76) * mm, "end": v(-203.46, -33.9) * mm});
            skLineSegment(sketch, "E372", {"start": v(-203.46, -33.9) * mm, "end": v(-203.14, -34.01) * mm});
            skLineSegment(sketch, "E373", {"start": v(-203.14, -34.01) * mm, "end": v(-202.81, -34.13) * mm});
            skLineSegment(sketch, "E374", {"start": v(-202.81, -34.13) * mm, "end": v(-202.34, -34.22) * mm});
            skLineSegment(sketch, "E375", {"start": v(-202.34, -34.22) * mm, "end": v(-201.86, -34.26) * mm});
            skLineSegment(sketch, "E376", {"start": v(-201.86, -34.26) * mm, "end": v(-201.38, -34.24) * mm});
            skLineSegment(sketch, "E377", {"start": v(-201.38, -34.24) * mm, "end": v(-200.9, -34.17) * mm});
            skLineSegment(sketch, "E378", {"start": v(-200.9, -34.17) * mm, "end": v(-200.44, -34.05) * mm});
            skLineSegment(sketch, "E379", {"start": v(-200.44, -34.05) * mm, "end": v(-200, -33.87) * mm});
            skLineSegment(sketch, "E380", {"start": v(-200, -33.87) * mm, "end": v(-199.53, -33.63) * mm});
            skLineSegment(sketch, "E381", {"start": v(-199.53, -33.63) * mm, "end": v(-199.08, -33.35) * mm});
            skLineSegment(sketch, "E382", {"start": v(-199.08, -33.35) * mm, "end": v(-198.67, -33.03) * mm});
            skLineSegment(sketch, "E383", {"start": v(-198.67, -33.03) * mm, "end": v(-198.29, -32.67) * mm});
            skLineSegment(sketch, "E384", {"start": v(-198.29, -32.67) * mm, "end": v(-197.94, -32.28) * mm});
            skLineSegment(sketch, "E385", {"start": v(-197.94, -32.28) * mm, "end": v(-197.65, -31.8) * mm});
            skLineSegment(sketch, "E386", {"start": v(-197.65, -31.8) * mm, "end": v(-197.4, -31.29) * mm});
            skLineSegment(sketch, "E387", {"start": v(-197.4, -31.29) * mm, "end": v(-197.21, -30.76) * mm});
            skLineSegment(sketch, "E388", {"start": v(-197.21, -30.76) * mm, "end": v(-197.07, -30.22) * mm});
            skLineSegment(sketch, "E389", {"start": v(-197.07, -30.22) * mm, "end": v(-196.98, -29.66) * mm});
            skLineSegment(sketch, "E390", {"start": v(-196.98, -29.66) * mm, "end": v(-196.92, -29.34) * mm});
            skLineSegment(sketch, "E391", {"start": v(-196.92, -29.34) * mm, "end": v(-196.9, -27.47) * mm});
            skLineSegment(sketch, "E392", {"start": v(-196.9, -27.47) * mm, "end": v(-196.8, 7.2) * mm});
            skLineSegment(sketch, "E393", {"start": v(-196.8, 7.2) * mm, "end": v(-191.14, 7.23) * mm});
            skLineSegment(sketch, "E394", {"start": v(-191.14, 7.23) * mm, "end": v(-188.32, 7.25) * mm});
            skLineSegment(sketch, "E395", {"start": v(-188.32, 7.25) * mm, "end": v(-185.49, 7.24) * mm});
            skLineSegment(sketch, "E396", {"start": v(-185.49, 7.24) * mm, "end": v(-183.82, 7.22) * mm});
            skLineSegment(sketch, "E397", {"start": v(-183.82, 7.22) * mm, "end": v(-197.42, 55.23) * mm});
            skLineSegment(sketch, "E398", {"start": v(-197.42, 55.23) * mm, "end": v(-196.82, 55.23) * mm});
            skLineSegment(sketch, "E399", {"start": v(-196.82, 55.23) * mm, "end": v(-195.63, 55.22) * mm});
            skLineSegment(sketch, "E400", {"start": v(-195.63, 55.22) * mm, "end": v(-195.03, 55.2) * mm});
            skLineSegment(sketch, "E401", {"start": v(-195.03, 55.2) * mm, "end": v(-194.32, 52.47) * mm});
            skLineSegment(sketch, "E402", {"start": v(-194.32, 52.47) * mm, "end": v(-193.73, 50.25) * mm});
            skLineSegment(sketch, "E403", {"start": v(-193.73, 50.25) * mm, "end": v(-193.12, 48.03) * mm});
            skLineSegment(sketch, "E404", {"start": v(-193.12, 48.03) * mm, "end": v(-191.85, 43.6) * mm});
            skLineSegment(sketch, "E405", {"start": v(-191.85, 43.6) * mm, "end": v(-189.6, 35.73) * mm});
            skLineSegment(sketch, "E406", {"start": v(-189.6, 35.73) * mm, "end": v(-188.9, 33.37) * mm});
            skLineSegment(sketch, "E407", {"start": v(-188.9, 33.37) * mm, "end": v(-188.43, 31.73) * mm});
            skLineSegment(sketch, "E408", {"start": v(-188.43, 31.73) * mm, "end": v(-187.6, 28.69) * mm});
            skLineSegment(sketch, "E409", {"start": v(-187.6, 28.69) * mm, "end": v(-187.48, 28.37) * mm});
            skLineSegment(sketch, "E410", {"start": v(-187.48, 28.37) * mm, "end": v(-187.36, 28.05) * mm});
            skLineSegment(sketch, "E411", {"start": v(-187.36, 28.05) * mm, "end": v(-187.24, 27.73) * mm});
            skLineSegment(sketch, "E412", {"start": v(-187.24, 27.73) * mm, "end": v(-187.14, 27.4) * mm});
            skLineSegment(sketch, "E413", {"start": v(-187.14, 27.4) * mm, "end": v(-186.95, 26.93) * mm});
            skLineSegment(sketch, "E414", {"start": v(-186.95, 26.93) * mm, "end": v(-186.71, 26.47) * mm});
            skLineSegment(sketch, "E415", {"start": v(-186.71, 26.47) * mm, "end": v(-186.44, 26.04) * mm});
            skLineSegment(sketch, "E416", {"start": v(-186.44, 26.04) * mm, "end": v(-186.13, 25.63) * mm});
            skLineSegment(sketch, "E417", {"start": v(-186.13, 25.63) * mm, "end": v(-185.72, 25.24) * mm});
            skLineSegment(sketch, "E418", {"start": v(-185.72, 25.24) * mm, "end": v(-185.26, 24.9) * mm});
            skLineSegment(sketch, "E419", {"start": v(-185.26, 24.9) * mm, "end": v(-184.76, 24.64) * mm});
            skLineSegment(sketch, "E420", {"start": v(-184.76, 24.64) * mm, "end": v(-184.23, 24.44) * mm});
            skLineSegment(sketch, "E421", {"start": v(-184.23, 24.44) * mm, "end": v(-183.68, 24.32) * mm});
            skLineSegment(sketch, "E422", {"start": v(-183.68, 24.32) * mm, "end": v(-183.11, 24.27) * mm});
            skLineSegment(sketch, "E423", {"start": v(-183.11, 24.27) * mm, "end": v(-182.54, 24.3) * mm});
            skLineSegment(sketch, "E424", {"start": v(-182.54, 24.3) * mm, "end": v(-181.99, 24.4) * mm});
            skLineSegment(sketch, "E425", {"start": v(-181.99, 24.4) * mm, "end": v(-181.45, 24.57) * mm});
            skLineSegment(sketch, "E426", {"start": v(-181.45, 24.57) * mm, "end": v(-180.94, 24.82) * mm});
            skLineSegment(sketch, "E427", {"start": v(-180.94, 24.82) * mm, "end": v(-180.46, 25.13) * mm});
            skLineSegment(sketch, "E428", {"start": v(-180.46, 25.13) * mm, "end": v(-180.04, 25.5) * mm});
            skLineSegment(sketch, "E429", {"start": v(-180.04, 25.5) * mm, "end": v(-179.66, 25.94) * mm});
            skLineSegment(sketch, "E430", {"start": v(-179.66, 25.94) * mm, "end": v(-179.35, 26.4) * mm});
            skLineSegment(sketch, "E431", {"start": v(-179.35, 26.4) * mm, "end": v(-179.1, 26.92) * mm});
            skLineSegment(sketch, "E432", {"start": v(-179.1, 26.92) * mm, "end": v(-178.93, 27.46) * mm});
            skLineSegment(sketch, "E433", {"start": v(-178.93, 27.46) * mm, "end": v(-178.9, 27.82) * mm});
            skLineSegment(sketch, "E434", {"start": v(-178.9, 27.82) * mm, "end": v(-178.85, 28.53) * mm});
            skLineSegment(sketch, "E435", {"start": v(-178.85, 28.53) * mm, "end": v(-178.83, 28.89) * mm});
            skLineSegment(sketch, "E436", {"start": v(-178.83, 28.89) * mm, "end": v(-178.86, 29.25) * mm});
            skLineSegment(sketch, "E437", {"start": v(-178.86, 29.25) * mm, "end": v(-178.9, 29.6) * mm});
            skLineSegment(sketch, "E438", {"start": v(-178.9, 29.6) * mm, "end": v(-178.97, 29.96) * mm});
            skLineSegment(sketch, "E439", {"start": v(-178.97, 29.96) * mm, "end": v(-179.05, 30.32) * mm});
            skLineSegment(sketch, "E440", {"start": v(-179.05, 30.32) * mm, "end": v(-188.59, 62.2) * mm});
            skLineSegment(sketch, "E441", {"start": v(-188.59, 62.2) * mm, "end": v(-188.84, 62.66) * mm});
            skLineSegment(sketch, "E442", {"start": v(-188.84, 62.66) * mm, "end": v(-189.22, 63.34) * mm});
            skLineSegment(sketch, "E443", {"start": v(-189.22, 63.34) * mm, "end": v(-189.64, 63.99) * mm});
            skLineSegment(sketch, "E444", {"start": v(-189.64, 63.99) * mm, "end": v(-189.94, 64.4) * mm});
            skLineSegment(sketch, "E445", {"start": v(-189.94, 64.4) * mm, "end": v(-190.43, 65) * mm});
            skLineSegment(sketch, "E446", {"start": v(-190.43, 65) * mm, "end": v(-190.94, 65.59) * mm});
            skLineSegment(sketch, "E447", {"start": v(-190.94, 65.59) * mm, "end": v(-191.33, 65.93) * mm});
            skLineSegment(sketch, "E448", {"start": v(-191.33, 65.93) * mm, "end": v(-192.08, 66.64) * mm});
            skLineSegment(sketch, "E449", {"start": v(-192.08, 66.64) * mm, "end": v(-192.45, 67) * mm});
            skLineSegment(sketch, "E450", {"start": v(-192.45, 67) * mm, "end": v(-193.25, 67.54) * mm});
            skLineSegment(sketch, "E451", {"start": v(-193.25, 67.54) * mm, "end": v(-194.08, 68.03) * mm});
            skLineSegment(sketch, "E452", {"start": v(-194.08, 68.03) * mm, "end": v(-194.95, 68.45) * mm});
            skLineSegment(sketch, "E453", {"start": v(-194.95, 68.45) * mm, "end": v(-195.85, 68.81) * mm});
            skLineSegment(sketch, "E454", {"start": v(-195.85, 68.81) * mm, "end": v(-196.76, 69.11) * mm});
            skLineSegment(sketch, "E455", {"start": v(-196.76, 69.11) * mm, "end": v(-197.7, 69.34) * mm});
            skLineSegment(sketch, "E456", {"start": v(-197.7, 69.34) * mm, "end": v(-198.65, 69.5) * mm});
            skLineSegment(sketch, "E457", {"start": v(-198.65, 69.5) * mm, "end": v(-199.61, 69.6) * mm});
            skLineSegment(sketch, "E458", {"start": v(-199.61, 69.6) * mm, "end": v(-200.58, 69.63) * mm});
            skLineSegment(sketch, "E459", {"start": v(-200.58, 69.63) * mm, "end": v(-201.45, 69.71) * mm});
            skLineSegment(sketch, "E460", {"start": v(-201.45, 69.71) * mm, "end": v(-201.69, 69.72) * mm});
            skLineSegment(sketch, "E461", {"start": v(-201.69, 69.72) * mm, "end": v(-202.24, 69.73) * mm});
            skLineSegment(sketch, "E462", {"start": v(-202.24, 69.73) * mm, "end": v(-203.3, 69.74) * mm});
            skLineSegment(sketch, "E463", {"start": v(-203.3, 69.74) * mm, "end": v(-209, 69.74) * mm});
            skLineSegment(sketch, "E464", {"start": v(-209, 69.74) * mm, "end": v(-215.65, 69.67) * mm});
            skLineSegment(sketch, "E465", {"start": v(-216.94, 77.68) * mm, "end": v(-216.67, 77.25) * mm});
            skLineSegment(sketch, "E466", {"start": v(-216.67, 77.25) * mm, "end": v(-216.4, 76.83) * mm});
            skLineSegment(sketch, "E467", {"start": v(-216.4, 76.83) * mm, "end": v(-216.12, 76.4) * mm});
            skLineSegment(sketch, "E468", {"start": v(-216.12, 76.4) * mm, "end": v(-215.83, 76) * mm});
            skLineSegment(sketch, "E469", {"start": v(-215.83, 76) * mm, "end": v(-215.65, 75.82) * mm});
            skLineSegment(sketch, "E470", {"start": v(-215.65, 75.82) * mm, "end": v(-215.48, 75.64) * mm});
            skLineSegment(sketch, "E471", {"start": v(-215.48, 75.64) * mm, "end": v(-215.31, 75.46) * mm});
            skLineSegment(sketch, "E472", {"start": v(-215.31, 75.46) * mm, "end": v(-215.15, 75.27) * mm});
            skLineSegment(sketch, "E473", {"start": v(-215.15, 75.27) * mm, "end": v(-214.55, 74.72) * mm});
            skLineSegment(sketch, "E474", {"start": v(-214.55, 74.72) * mm, "end": v(-213.92, 74.23) * mm});
            skLineSegment(sketch, "E475", {"start": v(-213.92, 74.23) * mm, "end": v(-213.25, 73.78) * mm});
            skLineSegment(sketch, "E476", {"start": v(-213.25, 73.78) * mm, "end": v(-212.55, 73.38) * mm});
            skLineSegment(sketch, "E477", {"start": v(-212.55, 73.38) * mm, "end": v(-211.83, 73.03) * mm});
            skLineSegment(sketch, "E478", {"start": v(-211.83, 73.03) * mm, "end": v(-211.59, 72.96) * mm});
            skLineSegment(sketch, "E479", {"start": v(-211.59, 72.96) * mm, "end": v(-211.35, 72.87) * mm});
            skLineSegment(sketch, "E480", {"start": v(-211.35, 72.87) * mm, "end": v(-211.12, 72.79) * mm});
            skLineSegment(sketch, "E481", {"start": v(-211.12, 72.79) * mm, "end": v(-210.88, 72.7) * mm});
            skLineSegment(sketch, "E482", {"start": v(-210.88, 72.7) * mm, "end": v(-210.04, 72.48) * mm});
            skLineSegment(sketch, "E483", {"start": v(-210.04, 72.48) * mm, "end": v(-209.18, 72.34) * mm});
            skLineSegment(sketch, "E484", {"start": v(-209.18, 72.34) * mm, "end": v(-208.32, 72.28) * mm});
            skLineSegment(sketch, "E485", {"start": v(-208.32, 72.28) * mm, "end": v(-207.45, 72.28) * mm});
            skLineSegment(sketch, "E486", {"start": v(-207.45, 72.28) * mm, "end": v(-206.58, 72.36) * mm});
            skLineSegment(sketch, "E487", {"start": v(-206.58, 72.36) * mm, "end": v(-205.73, 72.5) * mm});
            skLineSegment(sketch, "E488", {"start": v(-205.73, 72.5) * mm, "end": v(-204.89, 72.72) * mm});
            skLineSegment(sketch, "E489", {"start": v(-204.89, 72.72) * mm, "end": v(-204.07, 73) * mm});
            skLineSegment(sketch, "E490", {"start": v(-204.07, 73) * mm, "end": v(-203.27, 73.36) * mm});
            skLineSegment(sketch, "E491", {"start": v(-203.27, 73.36) * mm, "end": v(-202.51, 73.78) * mm});
            skLineSegment(sketch, "E492", {"start": v(-202.51, 73.78) * mm, "end": v(-201.79, 74.26) * mm});
            skLineSegment(sketch, "E493", {"start": v(-201.79, 74.26) * mm, "end": v(-201.7, 74.35) * mm});
            skLineSegment(sketch, "E494", {"start": v(-201.7, 74.35) * mm, "end": v(-201.56, 74.48) * mm});
            skLineSegment(sketch, "E495", {"start": v(-201.56, 74.48) * mm, "end": v(-201.42, 74.6) * mm});
            skLineSegment(sketch, "E496", {"start": v(-201.42, 74.6) * mm, "end": v(-201.32, 74.7) * mm});
            skLineSegment(sketch, "E497", {"start": v(-201.32, 74.7) * mm, "end": v(-201.17, 74.8) * mm});
            skLineSegment(sketch, "E498", {"start": v(-201.17, 74.8) * mm, "end": v(-201.02, 74.93) * mm});
            skLineSegment(sketch, "E499", {"start": v(-201.02, 74.93) * mm, "end": v(-200.41, 75.52) * mm});
            skLineSegment(sketch, "E500", {"start": v(-200.41, 75.52) * mm, "end": v(-199.86, 76.17) * mm});
            skLineSegment(sketch, "E501", {"start": v(-199.86, 76.17) * mm, "end": v(-199.35, 76.86) * mm});
            skLineSegment(sketch, "E502", {"start": v(-199.35, 76.86) * mm, "end": v(-198.91, 77.59) * mm});
            skLineSegment(sketch, "E503", {"start": v(-198.91, 77.59) * mm, "end": v(-198.53, 78.35) * mm});
            skLineSegment(sketch, "E504", {"start": v(-198.53, 78.35) * mm, "end": v(-198.22, 79.15) * mm});
            skLineSegment(sketch, "E505", {"start": v(-198.22, 79.15) * mm, "end": v(-197.97, 79.97) * mm});
            skLineSegment(sketch, "E506", {"start": v(-197.97, 79.97) * mm, "end": v(-197.8, 80.8) * mm});
            skLineSegment(sketch, "E507", {"start": v(-197.8, 80.8) * mm, "end": v(-197.69, 81.65) * mm});
            skLineSegment(sketch, "E508", {"start": v(-197.69, 81.65) * mm, "end": v(-197.65, 82.5) * mm});
            skLineSegment(sketch, "E509", {"start": v(-197.65, 82.5) * mm, "end": v(-197.69, 83.35) * mm});
            skLineSegment(sketch, "E510", {"start": v(-197.69, 83.35) * mm, "end": v(-197.8, 84.2) * mm});
            skLineSegment(sketch, "E511", {"start": v(-197.8, 84.2) * mm, "end": v(-197.97, 85.04) * mm});
            skLineSegment(sketch, "E512", {"start": v(-197.97, 85.04) * mm, "end": v(-198.22, 85.85) * mm});
            skLineSegment(sketch, "E513", {"start": v(-198.22, 85.85) * mm, "end": v(-198.53, 86.65) * mm});
            skLineSegment(sketch, "E514", {"start": v(-198.53, 86.65) * mm, "end": v(-198.91, 87.41) * mm});
            skLineSegment(sketch, "E515", {"start": v(-198.91, 87.41) * mm, "end": v(-199.35, 88.14) * mm});
            skLineSegment(sketch, "E516", {"start": v(-199.35, 88.14) * mm, "end": v(-199.86, 88.83) * mm});
            skLineSegment(sketch, "E517", {"start": v(-199.86, 88.83) * mm, "end": v(-200.41, 89.48) * mm});
            skLineSegment(sketch, "E518", {"start": v(-200.41, 89.48) * mm, "end": v(-201.02, 90.08) * mm});
            skLineSegment(sketch, "E519", {"start": v(-201.02, 90.08) * mm, "end": v(-201.12, 90.15) * mm});
            skLineSegment(sketch, "E520", {"start": v(-201.12, 90.15) * mm, "end": v(-201.27, 90.27) * mm});
            skLineSegment(sketch, "E521", {"start": v(-201.27, 90.27) * mm, "end": v(-201.42, 90.4) * mm});
            skLineSegment(sketch, "E522", {"start": v(-201.42, 90.4) * mm, "end": v(-201.51, 90.48) * mm});
            skLineSegment(sketch, "E523", {"start": v(-201.51, 90.48) * mm, "end": v(-201.65, 90.6) * mm});
            skLineSegment(sketch, "E524", {"start": v(-201.65, 90.6) * mm, "end": v(-201.79, 90.74) * mm});
            skLineSegment(sketch, "E525", {"start": v(-201.79, 90.74) * mm, "end": v(-202.5, 91.22) * mm});
            skLineSegment(sketch, "E526", {"start": v(-202.5, 91.22) * mm, "end": v(-203.26, 91.64) * mm});
            skLineSegment(sketch, "E527", {"start": v(-203.26, 91.64) * mm, "end": v(-204.05, 92) * mm});
            skLineSegment(sketch, "E528", {"start": v(-204.05, 92) * mm, "end": v(-204.87, 92.28) * mm});
            skLineSegment(sketch, "E529", {"start": v(-204.87, 92.28) * mm, "end": v(-205.7, 92.5) * mm});
            skLineSegment(sketch, "E530", {"start": v(-205.7, 92.5) * mm, "end": v(-206.56, 92.65) * mm});
            skLineSegment(sketch, "E531", {"start": v(-206.56, 92.65) * mm, "end": v(-207.42, 92.72) * mm});
            skLineSegment(sketch, "E532", {"start": v(-207.42, 92.72) * mm, "end": v(-208.29, 92.72) * mm});
            skLineSegment(sketch, "E533", {"start": v(-208.29, 92.72) * mm, "end": v(-209.15, 92.65) * mm});
            skLineSegment(sketch, "E534", {"start": v(-209.15, 92.65) * mm, "end": v(-210, 92.51) * mm});
            skLineSegment(sketch, "E535", {"start": v(-210, 92.51) * mm, "end": v(-210.84, 92.3) * mm});
            skLineSegment(sketch, "E536", {"start": v(-210.84, 92.3) * mm, "end": v(-211.66, 92.02) * mm});
            skLineSegment(sketch, "E537", {"start": v(-211.66, 92.02) * mm, "end": v(-212.45, 91.67) * mm});
            skLineSegment(sketch, "E538", {"start": v(-212.45, 91.67) * mm, "end": v(-213.21, 91.25) * mm});
            skLineSegment(sketch, "E539", {"start": v(-213.21, 91.25) * mm, "end": v(-213.94, 90.78) * mm});
            skLineSegment(sketch, "E540", {"start": v(-213.94, 90.78) * mm, "end": v(-214.62, 90.24) * mm});
            skLineSegment(sketch, "E541", {"start": v(-214.62, 90.24) * mm, "end": v(-215.25, 89.65) * mm});
            skLineSegment(sketch, "E542", {"start": v(-215.25, 89.65) * mm, "end": v(-215.83, 89) * mm});
            skLineSegment(sketch, "E543", {"start": v(-215.83, 89) * mm, "end": v(-216.12, 88.6) * mm});
            skLineSegment(sketch, "E544", {"start": v(-216.12, 88.6) * mm, "end": v(-216.4, 88.18) * mm});
            skLineSegment(sketch, "E545", {"start": v(-216.4, 88.18) * mm, "end": v(-216.67, 87.76) * mm});
            skLineSegment(sketch, "E546", {"start": v(-216.67, 87.76) * mm, "end": v(-216.94, 87.34) * mm});
            skLineSegment(sketch, "E547", {"start": v(-216.94, 87.34) * mm, "end": v(-217.1, 87) * mm});
            skLineSegment(sketch, "E548", {"start": v(-217.1, 87) * mm, "end": v(-217.34, 86.48) * mm});
            skLineSegment(sketch, "E549", {"start": v(-217.34, 86.48) * mm, "end": v(-217.55, 85.95) * mm});
            skLineSegment(sketch, "E550", {"start": v(-217.55, 85.95) * mm, "end": v(-217.67, 85.6) * mm});
            skLineSegment(sketch, "E551", {"start": v(-217.67, 85.6) * mm, "end": v(-217.82, 85.05) * mm});
            skLineSegment(sketch, "E552", {"start": v(-217.82, 85.05) * mm, "end": v(-217.96, 84.5) * mm});
            skLineSegment(sketch, "E553", {"start": v(-217.96, 84.5) * mm, "end": v(-218.09, 83.63) * mm});
            skLineSegment(sketch, "E554", {"start": v(-218.09, 83.63) * mm, "end": v(-218.14, 82.76) * mm});
            skLineSegment(sketch, "E555", {"start": v(-218.14, 82.76) * mm, "end": v(-218.12, 81.88) * mm});
            skLineSegment(sketch, "E556", {"start": v(-218.12, 81.88) * mm, "end": v(-218.02, 81) * mm});
            skLineSegment(sketch, "E557", {"start": v(-218.02, 81) * mm, "end": v(-217.86, 80.14) * mm});
            skLineSegment(sketch, "E558", {"start": v(-217.86, 80.14) * mm, "end": v(-217.62, 79.3) * mm});
            skLineSegment(sketch, "E559", {"start": v(-217.62, 79.3) * mm, "end": v(-217.31, 78.48) * mm});
            skLineSegment(sketch, "E560", {"start": v(-217.31, 78.48) * mm, "end": v(-216.94, 77.68) * mm});
            skLineSegment(sketch, "E561", {"start": v(-111.05, -66.41) * mm, "end": v(-111.05, -47.36) * mm});
            skLineSegment(sketch, "E562", {"start": v(-111.05, -47.36) * mm, "end": v(-107.26, -47.36) * mm});
            skLineSegment(sketch, "E563", {"start": v(-107.26, -47.36) * mm, "end": v(-102.75, -60.85) * mm});
            skLineSegment(sketch, "E564", {"start": v(-102.75, -60.85) * mm, "end": v(-102.21, -62.5) * mm});
            skLineSegment(sketch, "E565", {"start": v(-102.21, -62.5) * mm, "end": v(-101.84, -63.67) * mm});
            skLineSegment(sketch, "E566", {"start": v(-101.84, -63.67) * mm, "end": v(-101.42, -62.39) * mm});
            skLineSegment(sketch, "E567", {"start": v(-101.42, -62.39) * mm, "end": v(-100.83, -60.62) * mm});
            skLineSegment(sketch, "E568", {"start": v(-100.83, -60.62) * mm, "end": v(-96.27, -47.36) * mm});
            skLineSegment(sketch, "E569", {"start": v(-96.27, -47.36) * mm, "end": v(-92.87, -47.36) * mm});
            skLineSegment(sketch, "E570", {"start": v(-92.87, -47.36) * mm, "end": v(-92.87, -66.41) * mm});
            skLineSegment(sketch, "E571", {"start": v(-92.87, -66.41) * mm, "end": v(-95.3, -66.41) * mm});
            skLineSegment(sketch, "E572", {"start": v(-95.3, -66.41) * mm, "end": v(-95.3, -50.47) * mm});
            skLineSegment(sketch, "E573", {"start": v(-95.3, -50.47) * mm, "end": v(-100.84, -66.41) * mm});
            skLineSegment(sketch, "E574", {"start": v(-100.84, -66.41) * mm, "end": v(-103.11, -66.41) * mm});
            skLineSegment(sketch, "E575", {"start": v(-103.11, -66.41) * mm, "end": v(-108.62, -50.2) * mm});
            skLineSegment(sketch, "E576", {"start": v(-108.62, -50.2) * mm, "end": v(-108.62, -66.41) * mm});
            skLineSegment(sketch, "E577", {"start": v(-108.62, -66.41) * mm, "end": v(-111.05, -66.41) * mm});
            skLineSegment(sketch, "E578", {"start": v(-129.9, -49.71) * mm, "end": v(-129.02, -48.9) * mm});
            skLineSegment(sketch, "E579", {"start": v(-129.02, -48.9) * mm, "end": v(-128.04, -48.23) * mm});
            skLineSegment(sketch, "E580", {"start": v(-128.04, -48.23) * mm, "end": v(-126.98, -47.7) * mm});
            skLineSegment(sketch, "E581", {"start": v(-126.98, -47.7) * mm, "end": v(-125.8, -47.32) * mm});
            skLineSegment(sketch, "E582", {"start": v(-125.8, -47.32) * mm, "end": v(-124.57, -47.1) * mm});
            skLineSegment(sketch, "E583", {"start": v(-124.57, -47.1) * mm, "end": v(-123.32, -47.03) * mm});
            skLineSegment(sketch, "E584", {"start": v(-123.32, -47.03) * mm, "end": v(-122.08, -47.1) * mm});
            skLineSegment(sketch, "E585", {"start": v(-122.08, -47.1) * mm, "end": v(-120.86, -47.33) * mm});
            skLineSegment(sketch, "E586", {"start": v(-120.86, -47.33) * mm, "end": v(-119.68, -47.73) * mm});
            skLineSegment(sketch, "E587", {"start": v(-119.68, -47.73) * mm, "end": v(-118.56, -48.29) * mm});
            skLineSegment(sketch, "E588", {"start": v(-118.56, -48.29) * mm, "end": v(-117.57, -48.98) * mm});
            skLineSegment(sketch, "E589", {"start": v(-117.57, -48.98) * mm, "end": v(-116.69, -49.8) * mm});
            skLineSegment(sketch, "E590", {"start": v(-116.69, -49.8) * mm, "end": v(-115.94, -50.75) * mm});
            skLineSegment(sketch, "E591", {"start": v(-115.94, -50.75) * mm, "end": v(-115.34, -51.8) * mm});
            skLineSegment(sketch, "E592", {"start": v(-115.34, -51.8) * mm, "end": v(-114.85, -52.98) * mm});
            skLineSegment(sketch, "E593", {"start": v(-114.85, -52.98) * mm, "end": v(-114.5, -54.2) * mm});
            skLineSegment(sketch, "E594", {"start": v(-114.5, -54.2) * mm, "end": v(-114.3, -55.55) * mm});
            skLineSegment(sketch, "E595", {"start": v(-114.3, -55.55) * mm, "end": v(-114.22, -56.92) * mm});
            skLineSegment(sketch, "E596", {"start": v(-114.22, -56.92) * mm, "end": v(-114.28, -58.26) * mm});
            skLineSegment(sketch, "E597", {"start": v(-114.28, -58.26) * mm, "end": v(-114.5, -59.58) * mm});
            skLineSegment(sketch, "E598", {"start": v(-114.5, -59.58) * mm, "end": v(-114.87, -60.87) * mm});
            skLineSegment(sketch, "E599", {"start": v(-114.87, -60.87) * mm, "end": v(-115.4, -62.1) * mm});
            skLineSegment(sketch, "E600", {"start": v(-115.4, -62.1) * mm, "end": v(-116.01, -63.15) * mm});
            skLineSegment(sketch, "E601", {"start": v(-116.01, -63.15) * mm, "end": v(-116.78, -64.09) * mm});
            skLineSegment(sketch, "E602", {"start": v(-116.78, -64.09) * mm, "end": v(-117.69, -64.9) * mm});
            skLineSegment(sketch, "E603", {"start": v(-117.69, -64.9) * mm, "end": v(-118.7, -65.56) * mm});
            skLineSegment(sketch, "E604", {"start": v(-118.7, -65.56) * mm, "end": v(-119.8, -66.08) * mm});
            skLineSegment(sketch, "E605", {"start": v(-119.8, -66.08) * mm, "end": v(-120.94, -66.45) * mm});
            skLineSegment(sketch, "E606", {"start": v(-120.94, -66.45) * mm, "end": v(-122.13, -66.67) * mm});
            skLineSegment(sketch, "E607", {"start": v(-122.13, -66.67) * mm, "end": v(-123.33, -66.74) * mm});
            skLineSegment(sketch, "E608", {"start": v(-123.33, -66.74) * mm, "end": v(-124.6, -66.67) * mm});
            skLineSegment(sketch, "E609", {"start": v(-124.6, -66.67) * mm, "end": v(-125.83, -66.43) * mm});
            skLineSegment(sketch, "E610", {"start": v(-125.83, -66.43) * mm, "end": v(-127.02, -66.02) * mm});
            skLineSegment(sketch, "E611", {"start": v(-127.02, -66.02) * mm, "end": v(-128.14, -65.44) * mm});
            skLineSegment(sketch, "E612", {"start": v(-128.14, -65.44) * mm, "end": v(-129.13, -64.74) * mm});
            skLineSegment(sketch, "E613", {"start": v(-129.13, -64.74) * mm, "end": v(-130, -63.9) * mm});
            skLineSegment(sketch, "E614", {"start": v(-130, -63.9) * mm, "end": v(-130.75, -62.95) * mm});
            skLineSegment(sketch, "E615", {"start": v(-130.75, -62.95) * mm, "end": v(-131.35, -61.9) * mm});
            skLineSegment(sketch, "E616", {"start": v(-131.35, -61.9) * mm, "end": v(-131.83, -60.76) * mm});
            skLineSegment(sketch, "E617", {"start": v(-131.83, -60.76) * mm, "end": v(-132.17, -59.58) * mm});
            skLineSegment(sketch, "E618", {"start": v(-132.17, -59.58) * mm, "end": v(-132.38, -58.36) * mm});
            skLineSegment(sketch, "E619", {"start": v(-132.38, -58.36) * mm, "end": v(-132.44, -57.14) * mm});
            skLineSegment(sketch, "E620", {"start": v(-132.44, -57.14) * mm, "end": v(-132.39, -55.7) * mm});
            skLineSegment(sketch, "E621", {"start": v(-132.39, -55.7) * mm, "end": v(-132.17, -54.3) * mm});
            skLineSegment(sketch, "E622", {"start": v(-132.17, -54.3) * mm, "end": v(-131.8, -52.9) * mm});
            skLineSegment(sketch, "E623", {"start": v(-131.8, -52.9) * mm, "end": v(-131.33, -51.75) * mm});
            skLineSegment(sketch, "E624", {"start": v(-131.33, -51.75) * mm, "end": v(-130.69, -50.68) * mm});
            skLineSegment(sketch, "E625", {"start": v(-130.69, -50.68) * mm, "end": v(-129.9, -49.71) * mm});
            skLineSegment(sketch, "E626", {"start": v(-128, -62.6) * mm, "end": v(-127.37, -63.2) * mm});
            skLineSegment(sketch, "E627", {"start": v(-127.37, -63.2) * mm, "end": v(-126.67, -63.7) * mm});
            skLineSegment(sketch, "E628", {"start": v(-126.67, -63.7) * mm, "end": v(-125.9, -64.09) * mm});
            skLineSegment(sketch, "E629", {"start": v(-125.9, -64.09) * mm, "end": v(-125.08, -64.37) * mm});
            skLineSegment(sketch, "E630", {"start": v(-125.08, -64.37) * mm, "end": v(-124.22, -64.53) * mm});
            skLineSegment(sketch, "E631", {"start": v(-124.22, -64.53) * mm, "end": v(-123.35, -64.58) * mm});
            skLineSegment(sketch, "E632", {"start": v(-123.35, -64.58) * mm, "end": v(-122.3, -64.52) * mm});
            skLineSegment(sketch, "E633", {"start": v(-122.3, -64.52) * mm, "end": v(-121.28, -64.28) * mm});
            skLineSegment(sketch, "E634", {"start": v(-121.28, -64.28) * mm, "end": v(-120.31, -63.87) * mm});
            skLineSegment(sketch, "E635", {"start": v(-120.31, -63.87) * mm, "end": v(-119.43, -63.3) * mm});
            skLineSegment(sketch, "E636", {"start": v(-119.43, -63.3) * mm, "end": v(-118.66, -62.58) * mm});
            skLineSegment(sketch, "E637", {"start": v(-118.66, -62.58) * mm, "end": v(-118.09, -61.84) * mm});
            skLineSegment(sketch, "E638", {"start": v(-118.09, -61.84) * mm, "end": v(-117.62, -61.03) * mm});
            skLineSegment(sketch, "E639", {"start": v(-117.62, -61.03) * mm, "end": v(-117.28, -60.16) * mm});
            skLineSegment(sketch, "E640", {"start": v(-117.28, -60.16) * mm, "end": v(-117.02, -59.1) * mm});
            skLineSegment(sketch, "E641", {"start": v(-117.02, -59.1) * mm, "end": v(-116.86, -58) * mm});
            skLineSegment(sketch, "E642", {"start": v(-116.86, -58) * mm, "end": v(-116.82, -56.9) * mm});
            skLineSegment(sketch, "E643", {"start": v(-116.82, -56.9) * mm, "end": v(-116.9, -55.52) * mm});
            skLineSegment(sketch, "E644", {"start": v(-116.9, -55.52) * mm, "end": v(-117.16, -54.15) * mm});
            skLineSegment(sketch, "E645", {"start": v(-117.16, -54.15) * mm, "end": v(-117.6, -52.84) * mm});
            skLineSegment(sketch, "E646", {"start": v(-117.6, -52.84) * mm, "end": v(-118.03, -52.05) * mm});
            skLineSegment(sketch, "E647", {"start": v(-118.03, -52.05) * mm, "end": v(-118.56, -51.32) * mm});
            skLineSegment(sketch, "E648", {"start": v(-118.56, -51.32) * mm, "end": v(-119.2, -50.69) * mm});
            skLineSegment(sketch, "E649", {"start": v(-119.2, -50.69) * mm, "end": v(-119.9, -50.15) * mm});
            skLineSegment(sketch, "E650", {"start": v(-119.9, -50.15) * mm, "end": v(-120.69, -49.74) * mm});
            skLineSegment(sketch, "E651", {"start": v(-120.69, -49.74) * mm, "end": v(-121.52, -49.44) * mm});
            skLineSegment(sketch, "E652", {"start": v(-121.52, -49.44) * mm, "end": v(-122.4, -49.25) * mm});
            skLineSegment(sketch, "E653", {"start": v(-122.4, -49.25) * mm, "end": v(-123.3, -49.2) * mm});
            skLineSegment(sketch, "E654", {"start": v(-123.3, -49.2) * mm, "end": v(-124.32, -49.26) * mm});
            skLineSegment(sketch, "E655", {"start": v(-124.32, -49.26) * mm, "end": v(-125.32, -49.49) * mm});
            skLineSegment(sketch, "E656", {"start": v(-125.32, -49.49) * mm, "end": v(-126.26, -49.86) * mm});
            skLineSegment(sketch, "E657", {"start": v(-126.26, -49.86) * mm, "end": v(-127.13, -50.38) * mm});
            skLineSegment(sketch, "E658", {"start": v(-127.13, -50.38) * mm, "end": v(-127.91, -51.04) * mm});
            skLineSegment(sketch, "E659", {"start": v(-127.91, -51.04) * mm, "end": v(-128.53, -51.77) * mm});
            skLineSegment(sketch, "E660", {"start": v(-128.53, -51.77) * mm, "end": v(-129.02, -52.6) * mm});
            skLineSegment(sketch, "E661", {"start": v(-129.02, -52.6) * mm, "end": v(-129.36, -53.5) * mm});
            skLineSegment(sketch, "E662", {"start": v(-129.36, -53.5) * mm, "end": v(-129.65, -54.7) * mm});
            skLineSegment(sketch, "E663", {"start": v(-129.65, -54.7) * mm, "end": v(-129.8, -55.93) * mm});
            skLineSegment(sketch, "E664", {"start": v(-129.8, -55.93) * mm, "end": v(-129.84, -57.18) * mm});
            skLineSegment(sketch, "E665", {"start": v(-129.84, -57.18) * mm, "end": v(-129.8, -58.22) * mm});
            skLineSegment(sketch, "E666", {"start": v(-129.8, -58.22) * mm, "end": v(-129.65, -59.25) * mm});
            skLineSegment(sketch, "E667", {"start": v(-129.65, -59.25) * mm, "end": v(-129.38, -60.25) * mm});
            skLineSegment(sketch, "E668", {"start": v(-129.38, -60.25) * mm, "end": v(-129.03, -61.1) * mm});
            skLineSegment(sketch, "E669", {"start": v(-129.03, -61.1) * mm, "end": v(-128.57, -61.89) * mm});
            skLineSegment(sketch, "E670", {"start": v(-128.57, -61.89) * mm, "end": v(-128, -62.6) * mm});
            skLineSegment(sketch, "E671", {"start": v(-151.24, -49.71) * mm, "end": v(-150.37, -48.9) * mm});
            skLineSegment(sketch, "E672", {"start": v(-150.37, -48.9) * mm, "end": v(-149.4, -48.23) * mm});
            skLineSegment(sketch, "E673", {"start": v(-149.4, -48.23) * mm, "end": v(-148.33, -47.7) * mm});
            skLineSegment(sketch, "E674", {"start": v(-148.33, -47.7) * mm, "end": v(-147.14, -47.32) * mm});
            skLineSegment(sketch, "E675", {"start": v(-147.14, -47.32) * mm, "end": v(-145.91, -47.1) * mm});
            skLineSegment(sketch, "E676", {"start": v(-145.91, -47.1) * mm, "end": v(-144.67, -47.03) * mm});
            skLineSegment(sketch, "E677", {"start": v(-144.67, -47.03) * mm, "end": v(-143.43, -47.1) * mm});
            skLineSegment(sketch, "E678", {"start": v(-143.43, -47.1) * mm, "end": v(-142.2, -47.33) * mm});
            skLineSegment(sketch, "E679", {"start": v(-142.2, -47.33) * mm, "end": v(-141.03, -47.73) * mm});
            skLineSegment(sketch, "E680", {"start": v(-141.03, -47.73) * mm, "end": v(-139.91, -48.29) * mm});
            skLineSegment(sketch, "E681", {"start": v(-139.91, -48.29) * mm, "end": v(-138.92, -48.98) * mm});
            skLineSegment(sketch, "E682", {"start": v(-138.92, -48.98) * mm, "end": v(-138.04, -49.8) * mm});
            skLineSegment(sketch, "E683", {"start": v(-138.04, -49.8) * mm, "end": v(-137.29, -50.75) * mm});
            skLineSegment(sketch, "E684", {"start": v(-137.29, -50.75) * mm, "end": v(-136.68, -51.8) * mm});
            skLineSegment(sketch, "E685", {"start": v(-136.68, -51.8) * mm, "end": v(-136.2, -52.98) * mm});
            skLineSegment(sketch, "E686", {"start": v(-136.2, -52.98) * mm, "end": v(-135.85, -54.2) * mm});
            skLineSegment(sketch, "E687", {"start": v(-135.85, -54.2) * mm, "end": v(-135.64, -55.55) * mm});
            skLineSegment(sketch, "E688", {"start": v(-135.64, -55.55) * mm, "end": v(-135.57, -56.92) * mm});
            skLineSegment(sketch, "E689", {"start": v(-135.57, -56.92) * mm, "end": v(-135.63, -58.26) * mm});
            skLineSegment(sketch, "E690", {"start": v(-135.63, -58.26) * mm, "end": v(-135.85, -59.58) * mm});
            skLineSegment(sketch, "E691", {"start": v(-135.85, -59.58) * mm, "end": v(-136.22, -60.87) * mm});
            skLineSegment(sketch, "E692", {"start": v(-136.22, -60.87) * mm, "end": v(-136.74, -62.1) * mm});
            skLineSegment(sketch, "E693", {"start": v(-136.74, -62.1) * mm, "end": v(-137.36, -63.15) * mm});
            skLineSegment(sketch, "E694", {"start": v(-137.36, -63.15) * mm, "end": v(-138.13, -64.09) * mm});
            skLineSegment(sketch, "E695", {"start": v(-138.13, -64.09) * mm, "end": v(-139.04, -64.9) * mm});
            skLineSegment(sketch, "E696", {"start": v(-139.04, -64.9) * mm, "end": v(-140.06, -65.56) * mm});
            skLineSegment(sketch, "E697", {"start": v(-140.06, -65.56) * mm, "end": v(-141.14, -66.08) * mm});
            skLineSegment(sketch, "E698", {"start": v(-141.14, -66.08) * mm, "end": v(-142.28, -66.45) * mm});
            skLineSegment(sketch, "E699", {"start": v(-142.28, -66.45) * mm, "end": v(-143.47, -66.67) * mm});
            skLineSegment(sketch, "E700", {"start": v(-143.47, -66.67) * mm, "end": v(-144.68, -66.74) * mm});
            skLineSegment(sketch, "E701", {"start": v(-144.68, -66.74) * mm, "end": v(-145.94, -66.67) * mm});
            skLineSegment(sketch, "E702", {"start": v(-145.94, -66.67) * mm, "end": v(-147.18, -66.43) * mm});
            skLineSegment(sketch, "E703", {"start": v(-147.18, -66.43) * mm, "end": v(-148.37, -66.02) * mm});
            skLineSegment(sketch, "E704", {"start": v(-148.37, -66.02) * mm, "end": v(-149.49, -65.44) * mm});
            skLineSegment(sketch, "E705", {"start": v(-149.49, -65.44) * mm, "end": v(-150.48, -64.74) * mm});
            skLineSegment(sketch, "E706", {"start": v(-150.48, -64.74) * mm, "end": v(-151.35, -63.9) * mm});
            skLineSegment(sketch, "E707", {"start": v(-151.35, -63.9) * mm, "end": v(-152.1, -62.95) * mm});
            skLineSegment(sketch, "E708", {"start": v(-152.1, -62.95) * mm, "end": v(-152.7, -61.9) * mm});
            skLineSegment(sketch, "E709", {"start": v(-152.7, -61.9) * mm, "end": v(-153.17, -60.76) * mm});
            skLineSegment(sketch, "E710", {"start": v(-153.17, -60.76) * mm, "end": v(-153.52, -59.58) * mm});
            skLineSegment(sketch, "E711", {"start": v(-153.52, -59.58) * mm, "end": v(-153.72, -58.36) * mm});
            skLineSegment(sketch, "E712", {"start": v(-153.72, -58.36) * mm, "end": v(-153.8, -57.14) * mm});
            skLineSegment(sketch, "E713", {"start": v(-153.8, -57.14) * mm, "end": v(-153.73, -55.7) * mm});
            skLineSegment(sketch, "E714", {"start": v(-153.73, -55.7) * mm, "end": v(-153.52, -54.3) * mm});
            skLineSegment(sketch, "E715", {"start": v(-153.52, -54.3) * mm, "end": v(-153.15, -52.9) * mm});
            skLineSegment(sketch, "E716", {"start": v(-153.15, -52.9) * mm, "end": v(-152.67, -51.75) * mm});
            skLineSegment(sketch, "E717", {"start": v(-152.67, -51.75) * mm, "end": v(-152.03, -50.68) * mm});
            skLineSegment(sketch, "E718", {"start": v(-152.03, -50.68) * mm, "end": v(-151.24, -49.71) * mm});
            skLineSegment(sketch, "E719", {"start": v(-149.34, -62.6) * mm, "end": v(-148.72, -63.2) * mm});
            skLineSegment(sketch, "E720", {"start": v(-148.72, -63.2) * mm, "end": v(-148.02, -63.7) * mm});
            skLineSegment(sketch, "E721", {"start": v(-148.02, -63.7) * mm, "end": v(-147.25, -64.09) * mm});
            skLineSegment(sketch, "E722", {"start": v(-147.25, -64.09) * mm, "end": v(-146.42, -64.37) * mm});
            skLineSegment(sketch, "E723", {"start": v(-146.42, -64.37) * mm, "end": v(-145.57, -64.53) * mm});
            skLineSegment(sketch, "E724", {"start": v(-145.57, -64.53) * mm, "end": v(-144.7, -64.58) * mm});
            skLineSegment(sketch, "E725", {"start": v(-144.7, -64.58) * mm, "end": v(-143.65, -64.52) * mm});
            skLineSegment(sketch, "E726", {"start": v(-143.65, -64.52) * mm, "end": v(-142.62, -64.28) * mm});
            skLineSegment(sketch, "E727", {"start": v(-142.62, -64.28) * mm, "end": v(-141.66, -63.87) * mm});
            skLineSegment(sketch, "E728", {"start": v(-141.66, -63.87) * mm, "end": v(-140.78, -63.3) * mm});
            skLineSegment(sketch, "E729", {"start": v(-140.78, -63.3) * mm, "end": v(-140, -62.58) * mm});
            skLineSegment(sketch, "E730", {"start": v(-140, -62.58) * mm, "end": v(-139.43, -61.84) * mm});
            skLineSegment(sketch, "E731", {"start": v(-139.43, -61.84) * mm, "end": v(-138.97, -61.03) * mm});
            skLineSegment(sketch, "E732", {"start": v(-138.97, -61.03) * mm, "end": v(-138.63, -60.16) * mm});
            skLineSegment(sketch, "E733", {"start": v(-138.63, -60.16) * mm, "end": v(-138.36, -59.1) * mm});
            skLineSegment(sketch, "E734", {"start": v(-138.36, -59.1) * mm, "end": v(-138.21, -58) * mm});
            skLineSegment(sketch, "E735", {"start": v(-138.21, -58) * mm, "end": v(-138.17, -56.9) * mm});
            skLineSegment(sketch, "E736", {"start": v(-138.17, -56.9) * mm, "end": v(-138.24, -55.52) * mm});
            skLineSegment(sketch, "E737", {"start": v(-138.24, -55.52) * mm, "end": v(-138.5, -54.15) * mm});
            skLineSegment(sketch, "E738", {"start": v(-138.5, -54.15) * mm, "end": v(-138.96, -52.84) * mm});
            skLineSegment(sketch, "E739", {"start": v(-138.96, -52.84) * mm, "end": v(-139.38, -52.05) * mm});
            skLineSegment(sketch, "E740", {"start": v(-139.38, -52.05) * mm, "end": v(-139.9, -51.32) * mm});
            skLineSegment(sketch, "E741", {"start": v(-139.9, -51.32) * mm, "end": v(-140.54, -50.69) * mm});
            skLineSegment(sketch, "E742", {"start": v(-140.54, -50.69) * mm, "end": v(-141.26, -50.15) * mm});
            skLineSegment(sketch, "E743", {"start": v(-141.26, -50.15) * mm, "end": v(-142.03, -49.74) * mm});
            skLineSegment(sketch, "E744", {"start": v(-142.03, -49.74) * mm, "end": v(-142.86, -49.44) * mm});
            skLineSegment(sketch, "E745", {"start": v(-142.86, -49.44) * mm, "end": v(-143.75, -49.25) * mm});
            skLineSegment(sketch, "E746", {"start": v(-143.75, -49.25) * mm, "end": v(-144.66, -49.2) * mm});
            skLineSegment(sketch, "E747", {"start": v(-144.66, -49.2) * mm, "end": v(-145.67, -49.26) * mm});
            skLineSegment(sketch, "E748", {"start": v(-145.67, -49.26) * mm, "end": v(-146.66, -49.49) * mm});
            skLineSegment(sketch, "E749", {"start": v(-146.66, -49.49) * mm, "end": v(-147.6, -49.86) * mm});
            skLineSegment(sketch, "E750", {"start": v(-147.6, -49.86) * mm, "end": v(-148.48, -50.38) * mm});
            skLineSegment(sketch, "E751", {"start": v(-148.48, -50.38) * mm, "end": v(-149.26, -51.04) * mm});
            skLineSegment(sketch, "E752", {"start": v(-149.26, -51.04) * mm, "end": v(-149.88, -51.77) * mm});
            skLineSegment(sketch, "E753", {"start": v(-149.88, -51.77) * mm, "end": v(-150.37, -52.6) * mm});
            skLineSegment(sketch, "E754", {"start": v(-150.37, -52.6) * mm, "end": v(-150.7, -53.5) * mm});
            skLineSegment(sketch, "E755", {"start": v(-150.7, -53.5) * mm, "end": v(-151, -54.7) * mm});
            skLineSegment(sketch, "E756", {"start": v(-151, -54.7) * mm, "end": v(-151.15, -55.93) * mm});
            skLineSegment(sketch, "E757", {"start": v(-151.15, -55.93) * mm, "end": v(-151.2, -57.18) * mm});
            skLineSegment(sketch, "E758", {"start": v(-151.2, -57.18) * mm, "end": v(-151.15, -58.22) * mm});
            skLineSegment(sketch, "E759", {"start": v(-151.15, -58.22) * mm, "end": v(-151, -59.25) * mm});
            skLineSegment(sketch, "E760", {"start": v(-151, -59.25) * mm, "end": v(-150.73, -60.25) * mm});
            skLineSegment(sketch, "E761", {"start": v(-150.73, -60.25) * mm, "end": v(-150.38, -61.1) * mm});
            skLineSegment(sketch, "E762", {"start": v(-150.38, -61.1) * mm, "end": v(-149.91, -61.89) * mm});
            skLineSegment(sketch, "E763", {"start": v(-149.91, -61.89) * mm, "end": v(-149.34, -62.6) * mm});
            skLineSegment(sketch, "E764", {"start": v(-172.2, -66.41) * mm, "end": v(-172.2, -47.36) * mm});
            skLineSegment(sketch, "E765", {"start": v(-172.2, -47.36) * mm, "end": v(-163.76, -47.36) * mm});
            skLineSegment(sketch, "E766", {"start": v(-163.76, -47.36) * mm, "end": v(-162.45, -47.38) * mm});
            skLineSegment(sketch, "E767", {"start": v(-162.45, -47.38) * mm, "end": v(-161.15, -47.56) * mm});
            skLineSegment(sketch, "E768", {"start": v(-161.15, -47.56) * mm, "end": v(-159.88, -47.88) * mm});
            skLineSegment(sketch, "E769", {"start": v(-159.88, -47.88) * mm, "end": v(-159.25, -48.2) * mm});
            skLineSegment(sketch, "E770", {"start": v(-159.25, -48.2) * mm, "end": v(-158.67, -48.6) * mm});
            skLineSegment(sketch, "E771", {"start": v(-158.67, -48.6) * mm, "end": v(-158.17, -49.1) * mm});
            skLineSegment(sketch, "E772", {"start": v(-158.17, -49.1) * mm, "end": v(-157.77, -49.7) * mm});
            skLineSegment(sketch, "E773", {"start": v(-157.77, -49.7) * mm, "end": v(-157.32, -50.6) * mm});
            skLineSegment(sketch, "E774", {"start": v(-157.32, -50.6) * mm, "end": v(-157.06, -51.56) * mm});
            skLineSegment(sketch, "E775", {"start": v(-157.06, -51.56) * mm, "end": v(-156.97, -52.56) * mm});
            skLineSegment(sketch, "E776", {"start": v(-156.97, -52.56) * mm, "end": v(-157.04, -53.5) * mm});
            skLineSegment(sketch, "E777", {"start": v(-157.04, -53.5) * mm, "end": v(-157.3, -54.4) * mm});
            skLineSegment(sketch, "E778", {"start": v(-157.3, -54.4) * mm, "end": v(-157.71, -55.24) * mm});
            skLineSegment(sketch, "E779", {"start": v(-157.71, -55.24) * mm, "end": v(-158.29, -55.98) * mm});
            skLineSegment(sketch, "E780", {"start": v(-158.29, -55.98) * mm, "end": v(-158.8, -56.43) * mm});
            skLineSegment(sketch, "E781", {"start": v(-158.8, -56.43) * mm, "end": v(-159.35, -56.81) * mm});
            skLineSegment(sketch, "E782", {"start": v(-159.35, -56.81) * mm, "end": v(-159.96, -57.12) * mm});
            skLineSegment(sketch, "E783", {"start": v(-159.96, -57.12) * mm, "end": v(-161.13, -57.51) * mm});
            skLineSegment(sketch, "E784", {"start": v(-161.13, -57.51) * mm, "end": v(-162.34, -57.75) * mm});
            skLineSegment(sketch, "E785", {"start": v(-162.34, -57.75) * mm, "end": v(-161.46, -58.23) * mm});
            skLineSegment(sketch, "E786", {"start": v(-161.46, -58.23) * mm, "end": v(-160.82, -58.7) * mm});
            skLineSegment(sketch, "E787", {"start": v(-160.82, -58.7) * mm, "end": v(-160.26, -59.25) * mm});
            skLineSegment(sketch, "E788", {"start": v(-160.26, -59.25) * mm, "end": v(-159.75, -59.84) * mm});
            skLineSegment(sketch, "E789", {"start": v(-159.75, -59.84) * mm, "end": v(-158.73, -61.23) * mm});
            skLineSegment(sketch, "E790", {"start": v(-158.73, -61.23) * mm, "end": v(-155.41, -66.41) * mm});
            skLineSegment(sketch, "E791", {"start": v(-155.41, -66.41) * mm, "end": v(-158.59, -66.41) * mm});
            skLineSegment(sketch, "E792", {"start": v(-158.59, -66.41) * mm, "end": v(-161.1, -62.45) * mm});
            skLineSegment(sketch, "E793", {"start": v(-161.1, -62.45) * mm, "end": v(-161.99, -61.12) * mm});
            skLineSegment(sketch, "E794", {"start": v(-161.99, -61.12) * mm, "end": v(-162.93, -59.83) * mm});
            skLineSegment(sketch, "E795", {"start": v(-162.93, -59.83) * mm, "end": v(-163.52, -59.14) * mm});
            skLineSegment(sketch, "E796", {"start": v(-163.52, -59.14) * mm, "end": v(-164.2, -58.55) * mm});
            skLineSegment(sketch, "E797", {"start": v(-164.2, -58.55) * mm, "end": v(-164.76, -58.25) * mm});
            skLineSegment(sketch, "E798", {"start": v(-164.76, -58.25) * mm, "end": v(-165.36, -58.05) * mm});
            skLineSegment(sketch, "E799", {"start": v(-165.36, -58.05) * mm, "end": v(-165.92, -57.98) * mm});
            skLineSegment(sketch, "E800", {"start": v(-165.92, -57.98) * mm, "end": v(-166.76, -57.96) * mm});
            skLineSegment(sketch, "E801", {"start": v(-166.76, -57.96) * mm, "end": v(-169.68, -57.96) * mm});
            skLineSegment(sketch, "E802", {"start": v(-169.68, -57.96) * mm, "end": v(-169.68, -66.41) * mm});
            skLineSegment(sketch, "E803", {"start": v(-169.68, -66.41) * mm, "end": v(-172.2, -66.41) * mm});
            skLineSegment(sketch, "E804", {"start": v(-169.68, -55.77) * mm, "end": v(-164.26, -55.77) * mm});
            skLineSegment(sketch, "E805", {"start": v(-164.26, -55.77) * mm, "end": v(-163.35, -55.75) * mm});
            skLineSegment(sketch, "E806", {"start": v(-163.35, -55.75) * mm, "end": v(-162.45, -55.64) * mm});
            skLineSegment(sketch, "E807", {"start": v(-162.45, -55.64) * mm, "end": v(-161.56, -55.41) * mm});
            skLineSegment(sketch, "E808", {"start": v(-161.56, -55.41) * mm, "end": v(-160.99, -55.15) * mm});
            skLineSegment(sketch, "E809", {"start": v(-160.99, -55.15) * mm, "end": v(-160.48, -54.76) * mm});
            skLineSegment(sketch, "E810", {"start": v(-160.48, -54.76) * mm, "end": v(-160.08, -54.27) * mm});
            skLineSegment(sketch, "E811", {"start": v(-160.08, -54.27) * mm, "end": v(-159.8, -53.74) * mm});
            skLineSegment(sketch, "E812", {"start": v(-159.8, -53.74) * mm, "end": v(-159.63, -53.16) * mm});
            skLineSegment(sketch, "E813", {"start": v(-159.63, -53.16) * mm, "end": v(-159.57, -52.56) * mm});
            skLineSegment(sketch, "E814", {"start": v(-159.57, -52.56) * mm, "end": v(-159.63, -51.94) * mm});
            skLineSegment(sketch, "E815", {"start": v(-159.63, -51.94) * mm, "end": v(-159.81, -51.34) * mm});
            skLineSegment(sketch, "E816", {"start": v(-159.81, -51.34) * mm, "end": v(-160.13, -50.8) * mm});
            skLineSegment(sketch, "E817", {"start": v(-160.13, -50.8) * mm, "end": v(-160.55, -50.34) * mm});
            skLineSegment(sketch, "E818", {"start": v(-160.55, -50.34) * mm, "end": v(-161.15, -49.94) * mm});
            skLineSegment(sketch, "E819", {"start": v(-161.15, -49.94) * mm, "end": v(-161.82, -49.69) * mm});
            skLineSegment(sketch, "E820", {"start": v(-161.82, -49.69) * mm, "end": v(-162.73, -49.52) * mm});
            skLineSegment(sketch, "E821", {"start": v(-162.73, -49.52) * mm, "end": v(-163.65, -49.47) * mm});
            skLineSegment(sketch, "E822", {"start": v(-163.65, -49.47) * mm, "end": v(-169.68, -49.47) * mm});
            skLineSegment(sketch, "E823", {"start": v(-169.68, -49.47) * mm, "end": v(-169.68, -55.77) * mm});
            skLineSegment(sketch, "E824", {"start": v(-184.06, -66.41) * mm, "end": v(-184.06, -49.61) * mm});
            skLineSegment(sketch, "E825", {"start": v(-184.06, -49.61) * mm, "end": v(-190.34, -49.61) * mm});
            skLineSegment(sketch, "E826", {"start": v(-190.34, -49.61) * mm, "end": v(-190.34, -47.36) * mm});
            skLineSegment(sketch, "E827", {"start": v(-190.34, -47.36) * mm, "end": v(-175.24, -47.36) * mm});
            skLineSegment(sketch, "E828", {"start": v(-175.24, -47.36) * mm, "end": v(-175.24, -49.61) * mm});
            skLineSegment(sketch, "E829", {"start": v(-175.24, -49.61) * mm, "end": v(-181.54, -49.61) * mm});
            skLineSegment(sketch, "E830", {"start": v(-181.54, -49.61) * mm, "end": v(-181.54, -66.41) * mm});
            skLineSegment(sketch, "E831", {"start": v(-181.54, -66.41) * mm, "end": v(-184.06, -66.41) * mm});
            skLineSegment(sketch, "E832", {"start": v(-205.14, -60.09) * mm, "end": v(-205, -60.9) * mm});
            skLineSegment(sketch, "E833", {"start": v(-205, -60.9) * mm, "end": v(-204.74, -61.7) * mm});
            skLineSegment(sketch, "E834", {"start": v(-204.74, -61.7) * mm, "end": v(-204.36, -62.43) * mm});
            skLineSegment(sketch, "E835", {"start": v(-204.36, -62.43) * mm, "end": v(-203.82, -63.05) * mm});
            skLineSegment(sketch, "E836", {"start": v(-203.82, -63.05) * mm, "end": v(-203.17, -63.55) * mm});
            skLineSegment(sketch, "E837", {"start": v(-203.17, -63.55) * mm, "end": v(-202.44, -63.91) * mm});
            skLineSegment(sketch, "E838", {"start": v(-202.44, -63.91) * mm, "end": v(-201.76, -64.16) * mm});
            skLineSegment(sketch, "E839", {"start": v(-201.76, -64.16) * mm, "end": v(-201.06, -64.34) * mm});
            skLineSegment(sketch, "E840", {"start": v(-201.06, -64.34) * mm, "end": v(-200.29, -64.44) * mm});
            skLineSegment(sketch, "E841", {"start": v(-200.29, -64.44) * mm, "end": v(-199.52, -64.48) * mm});
            skLineSegment(sketch, "E842", {"start": v(-199.52, -64.48) * mm, "end": v(-198.65, -64.44) * mm});
            skLineSegment(sketch, "E843", {"start": v(-198.65, -64.44) * mm, "end": v(-197.8, -64.3) * mm});
            skLineSegment(sketch, "E844", {"start": v(-197.8, -64.3) * mm, "end": v(-196.97, -64.05) * mm});
            skLineSegment(sketch, "E845", {"start": v(-196.97, -64.05) * mm, "end": v(-196.27, -63.75) * mm});
            skLineSegment(sketch, "E846", {"start": v(-196.27, -63.75) * mm, "end": v(-195.67, -63.29) * mm});
            skLineSegment(sketch, "E847", {"start": v(-195.67, -63.29) * mm, "end": v(-195.2, -62.69) * mm});
            skLineSegment(sketch, "E848", {"start": v(-195.2, -62.69) * mm, "end": v(-194.9, -62) * mm});
            skLineSegment(sketch, "E849", {"start": v(-194.9, -62) * mm, "end": v(-194.79, -61.24) * mm});
            skLineSegment(sketch, "E850", {"start": v(-194.79, -61.24) * mm, "end": v(-194.84, -60.69) * mm});
            skLineSegment(sketch, "E851", {"start": v(-194.84, -60.69) * mm, "end": v(-195.01, -60.16) * mm});
            skLineSegment(sketch, "E852", {"start": v(-195.01, -60.16) * mm, "end": v(-195.3, -59.68) * mm});
            skLineSegment(sketch, "E853", {"start": v(-195.3, -59.68) * mm, "end": v(-195.62, -59.34) * mm});
            skLineSegment(sketch, "E854", {"start": v(-195.62, -59.34) * mm, "end": v(-196, -59.06) * mm});
            skLineSegment(sketch, "E855", {"start": v(-196, -59.06) * mm, "end": v(-196.5, -58.78) * mm});
            skLineSegment(sketch, "E856", {"start": v(-196.5, -58.78) * mm, "end": v(-197.02, -58.55) * mm});
            skLineSegment(sketch, "E857", {"start": v(-197.02, -58.55) * mm, "end": v(-198.7, -58.04) * mm});
            skLineSegment(sketch, "E858", {"start": v(-198.7, -58.04) * mm, "end": v(-200.41, -57.62) * mm});
            skLineSegment(sketch, "E859", {"start": v(-200.41, -57.62) * mm, "end": v(-202.64, -57.01) * mm});
            skLineSegment(sketch, "E860", {"start": v(-202.64, -57.01) * mm, "end": v(-203.38, -56.75) * mm});
            skLineSegment(sketch, "E861", {"start": v(-203.38, -56.75) * mm, "end": v(-204.09, -56.44) * mm});
            skLineSegment(sketch, "E862", {"start": v(-204.09, -56.44) * mm, "end": v(-204.78, -56.04) * mm});
            skLineSegment(sketch, "E863", {"start": v(-204.78, -56.04) * mm, "end": v(-205.4, -55.54) * mm});
            skLineSegment(sketch, "E864", {"start": v(-205.4, -55.54) * mm, "end": v(-205.91, -54.95) * mm});
            skLineSegment(sketch, "E865", {"start": v(-205.91, -54.95) * mm, "end": v(-206.33, -54.27) * mm});
            skLineSegment(sketch, "E866", {"start": v(-206.33, -54.27) * mm, "end": v(-206.62, -53.54) * mm});
            skLineSegment(sketch, "E867", {"start": v(-206.62, -53.54) * mm, "end": v(-206.75, -52.92) * mm});
            skLineSegment(sketch, "E868", {"start": v(-206.75, -52.92) * mm, "end": v(-206.8, -52.29) * mm});
            skLineSegment(sketch, "E869", {"start": v(-206.8, -52.29) * mm, "end": v(-206.7, -51.34) * mm});
            skLineSegment(sketch, "E870", {"start": v(-206.7, -51.34) * mm, "end": v(-206.42, -50.43) * mm});
            skLineSegment(sketch, "E871", {"start": v(-206.42, -50.43) * mm, "end": v(-205.97, -49.6) * mm});
            skLineSegment(sketch, "E872", {"start": v(-205.97, -49.6) * mm, "end": v(-205.5, -48.98) * mm});
            skLineSegment(sketch, "E873", {"start": v(-205.5, -48.98) * mm, "end": v(-204.92, -48.46) * mm});
            skLineSegment(sketch, "E874", {"start": v(-204.92, -48.46) * mm, "end": v(-204.28, -48.02) * mm});
            skLineSegment(sketch, "E875", {"start": v(-204.28, -48.02) * mm, "end": v(-203.58, -47.69) * mm});
            skLineSegment(sketch, "E876", {"start": v(-203.58, -47.69) * mm, "end": v(-202.76, -47.4) * mm});
            skLineSegment(sketch, "E877", {"start": v(-202.76, -47.4) * mm, "end": v(-201.92, -47.2) * mm});
            skLineSegment(sketch, "E878", {"start": v(-201.92, -47.2) * mm, "end": v(-201, -47.08) * mm});
            skLineSegment(sketch, "E879", {"start": v(-201, -47.08) * mm, "end": v(-200.09, -47.04) * mm});
            skLineSegment(sketch, "E880", {"start": v(-200.09, -47.04) * mm, "end": v(-198.81, -47.1) * mm});
            skLineSegment(sketch, "E881", {"start": v(-198.81, -47.1) * mm, "end": v(-197.56, -47.33) * mm});
            skLineSegment(sketch, "E882", {"start": v(-197.56, -47.33) * mm, "end": v(-196.35, -47.72) * mm});
            skLineSegment(sketch, "E883", {"start": v(-196.35, -47.72) * mm, "end": v(-195.62, -48.08) * mm});
            skLineSegment(sketch, "E884", {"start": v(-195.62, -48.08) * mm, "end": v(-194.95, -48.54) * mm});
            skLineSegment(sketch, "E885", {"start": v(-194.95, -48.54) * mm, "end": v(-194.36, -49.1) * mm});
            skLineSegment(sketch, "E886", {"start": v(-194.36, -49.1) * mm, "end": v(-193.86, -49.73) * mm});
            skLineSegment(sketch, "E887", {"start": v(-193.86, -49.73) * mm, "end": v(-193.48, -50.41) * mm});
            skLineSegment(sketch, "E888", {"start": v(-193.48, -50.41) * mm, "end": v(-193.2, -51.14) * mm});
            skLineSegment(sketch, "E889", {"start": v(-193.2, -51.14) * mm, "end": v(-193, -51.93) * mm});
            skLineSegment(sketch, "E890", {"start": v(-193, -51.93) * mm, "end": v(-192.93, -52.73) * mm});
            skLineSegment(sketch, "E891", {"start": v(-192.93, -52.73) * mm, "end": v(-195.34, -52.91) * mm});
            skLineSegment(sketch, "E892", {"start": v(-195.34, -52.91) * mm, "end": v(-195.46, -52.15) * mm});
            skLineSegment(sketch, "E893", {"start": v(-195.46, -52.15) * mm, "end": v(-195.73, -51.42) * mm});
            skLineSegment(sketch, "E894", {"start": v(-195.73, -51.42) * mm, "end": v(-196.13, -50.75) * mm});
            skLineSegment(sketch, "E895", {"start": v(-196.13, -50.75) * mm, "end": v(-196.66, -50.18) * mm});
            skLineSegment(sketch, "E896", {"start": v(-196.66, -50.18) * mm, "end": v(-197.32, -49.77) * mm});
            skLineSegment(sketch, "E897", {"start": v(-197.32, -49.77) * mm, "end": v(-198.05, -49.5) * mm});
            skLineSegment(sketch, "E898", {"start": v(-198.05, -49.5) * mm, "end": v(-199.01, -49.31) * mm});
            skLineSegment(sketch, "E899", {"start": v(-199.01, -49.31) * mm, "end": v(-199.98, -49.26) * mm});
            skLineSegment(sketch, "E900", {"start": v(-199.98, -49.26) * mm, "end": v(-200.98, -49.3) * mm});
            skLineSegment(sketch, "E901", {"start": v(-200.98, -49.3) * mm, "end": v(-201.96, -49.47) * mm});
            skLineSegment(sketch, "E902", {"start": v(-201.96, -49.47) * mm, "end": v(-202.67, -49.71) * mm});
            skLineSegment(sketch, "E903", {"start": v(-202.67, -49.71) * mm, "end": v(-203.32, -50.1) * mm});
            skLineSegment(sketch, "E904", {"start": v(-203.32, -50.1) * mm, "end": v(-203.76, -50.52) * mm});
            skLineSegment(sketch, "E905", {"start": v(-203.76, -50.52) * mm, "end": v(-204.1, -51.02) * mm});
            skLineSegment(sketch, "E906", {"start": v(-204.1, -51.02) * mm, "end": v(-204.3, -51.56) * mm});
            skLineSegment(sketch, "E907", {"start": v(-204.3, -51.56) * mm, "end": v(-204.36, -52.12) * mm});
            skLineSegment(sketch, "E908", {"start": v(-204.36, -52.12) * mm, "end": v(-204.32, -52.6) * mm});
            skLineSegment(sketch, "E909", {"start": v(-204.32, -52.6) * mm, "end": v(-204.18, -53.06) * mm});
            skLineSegment(sketch, "E910", {"start": v(-204.18, -53.06) * mm, "end": v(-203.94, -53.46) * mm});
            skLineSegment(sketch, "E911", {"start": v(-203.94, -53.46) * mm, "end": v(-203.62, -53.81) * mm});
            skLineSegment(sketch, "E912", {"start": v(-203.62, -53.81) * mm, "end": v(-203, -54.2) * mm});
            skLineSegment(sketch, "E913", {"start": v(-203, -54.2) * mm, "end": v(-202.3, -54.48) * mm});
            skLineSegment(sketch, "E914", {"start": v(-202.3, -54.48) * mm, "end": v(-201.07, -54.86) * mm});
            skLineSegment(sketch, "E915", {"start": v(-201.07, -54.86) * mm, "end": v(-199.82, -55.17) * mm});
            skLineSegment(sketch, "E916", {"start": v(-199.82, -55.17) * mm, "end": v(-197.23, -55.82) * mm});
            skLineSegment(sketch, "E917", {"start": v(-197.23, -55.82) * mm, "end": v(-196.4, -56.07) * mm});
            skLineSegment(sketch, "E918", {"start": v(-196.4, -56.07) * mm, "end": v(-195.6, -56.38) * mm});
            skLineSegment(sketch, "E919", {"start": v(-195.6, -56.38) * mm, "end": v(-194.67, -56.88) * mm});
            skLineSegment(sketch, "E920", {"start": v(-194.67, -56.88) * mm, "end": v(-193.84, -57.53) * mm});
            skLineSegment(sketch, "E921", {"start": v(-193.84, -57.53) * mm, "end": v(-193.15, -58.33) * mm});
            skLineSegment(sketch, "E922", {"start": v(-193.15, -58.33) * mm, "end": v(-192.8, -58.94) * mm});
            skLineSegment(sketch, "E923", {"start": v(-192.8, -58.94) * mm, "end": v(-192.55, -59.6) * mm});
            skLineSegment(sketch, "E924", {"start": v(-192.55, -59.6) * mm, "end": v(-192.4, -60.3) * mm});
            skLineSegment(sketch, "E925", {"start": v(-192.4, -60.3) * mm, "end": v(-192.36, -61.04) * mm});
            skLineSegment(sketch, "E926", {"start": v(-192.36, -61.04) * mm, "end": v(-192.46, -62.04) * mm});
            skLineSegment(sketch, "E927", {"start": v(-192.46, -62.04) * mm, "end": v(-192.75, -63) * mm});
            skLineSegment(sketch, "E928", {"start": v(-192.75, -63) * mm, "end": v(-193.23, -63.9) * mm});
            skLineSegment(sketch, "E929", {"start": v(-193.23, -63.9) * mm, "end": v(-193.73, -64.55) * mm});
            skLineSegment(sketch, "E930", {"start": v(-193.73, -64.55) * mm, "end": v(-194.32, -65.13) * mm});
            skLineSegment(sketch, "E931", {"start": v(-194.32, -65.13) * mm, "end": v(-195, -65.61) * mm});
            skLineSegment(sketch, "E932", {"start": v(-195, -65.61) * mm, "end": v(-195.73, -66) * mm});
            skLineSegment(sketch, "E933", {"start": v(-195.73, -66) * mm, "end": v(-196.58, -66.32) * mm});
            skLineSegment(sketch, "E934", {"start": v(-196.58, -66.32) * mm, "end": v(-197.46, -66.55) * mm});
            skLineSegment(sketch, "E935", {"start": v(-197.46, -66.55) * mm, "end": v(-198.42, -66.7) * mm});
            skLineSegment(sketch, "E936", {"start": v(-198.42, -66.7) * mm, "end": v(-199.4, -66.74) * mm});
            skLineSegment(sketch, "E937", {"start": v(-199.4, -66.74) * mm, "end": v(-200.87, -66.68) * mm});
            skLineSegment(sketch, "E938", {"start": v(-200.87, -66.68) * mm, "end": v(-202.33, -66.43) * mm});
            skLineSegment(sketch, "E939", {"start": v(-202.33, -66.43) * mm, "end": v(-203.73, -65.99) * mm});
            skLineSegment(sketch, "E940", {"start": v(-203.73, -65.99) * mm, "end": v(-204.54, -65.58) * mm});
            skLineSegment(sketch, "E941", {"start": v(-204.54, -65.58) * mm, "end": v(-205.27, -65.06) * mm});
            skLineSegment(sketch, "E942", {"start": v(-205.27, -65.06) * mm, "end": v(-205.92, -64.43) * mm});
            skLineSegment(sketch, "E943", {"start": v(-205.92, -64.43) * mm, "end": v(-206.47, -63.72) * mm});
            skLineSegment(sketch, "E944", {"start": v(-206.47, -63.72) * mm, "end": v(-206.91, -62.94) * mm});
            skLineSegment(sketch, "E945", {"start": v(-206.91, -62.94) * mm, "end": v(-207.23, -62.1) * mm});
            skLineSegment(sketch, "E946", {"start": v(-207.23, -62.1) * mm, "end": v(-207.44, -61.2) * mm});
            skLineSegment(sketch, "E947", {"start": v(-207.44, -61.2) * mm, "end": v(-207.52, -60.3) * mm});
            skLineSegment(sketch, "E948", {"start": v(-207.52, -60.3) * mm, "end": v(-205.14, -60.09) * mm});
            skLineSegment(sketch, "E949", {"start": v(-224.36, -66.41) * mm, "end": v(-224.36, -47.36) * mm});
            skLineSegment(sketch, "E950", {"start": v(-224.36, -47.36) * mm, "end": v(-210.59, -47.36) * mm});
            skLineSegment(sketch, "E951", {"start": v(-210.59, -47.36) * mm, "end": v(-210.59, -49.61) * mm});
            skLineSegment(sketch, "E952", {"start": v(-210.59, -49.61) * mm, "end": v(-221.84, -49.61) * mm});
            skLineSegment(sketch, "E953", {"start": v(-221.84, -49.61) * mm, "end": v(-221.84, -55.45) * mm});
            skLineSegment(sketch, "E954", {"start": v(-221.84, -55.45) * mm, "end": v(-211.3, -55.45) * mm});
            skLineSegment(sketch, "E955", {"start": v(-211.3, -55.45) * mm, "end": v(-211.3, -57.68) * mm});
            skLineSegment(sketch, "E956", {"start": v(-211.3, -57.68) * mm, "end": v(-221.84, -57.68) * mm});
            skLineSegment(sketch, "E957", {"start": v(-221.84, -57.68) * mm, "end": v(-221.84, -64.17) * mm});
            skLineSegment(sketch, "E958", {"start": v(-221.84, -64.17) * mm, "end": v(-210.14, -64.17) * mm});
            skLineSegment(sketch, "E959", {"start": v(-210.14, -64.17) * mm, "end": v(-210.14, -66.41) * mm});
            skLineSegment(sketch, "E960", {"start": v(-210.14, -66.41) * mm, "end": v(-224.36, -66.41) * mm});
            skLineSegment(sketch, "E961", {"start": v(-244.32, -66.41) * mm, "end": v(-244.32, -47.36) * mm});
            skLineSegment(sketch, "E962", {"start": v(-244.32, -47.36) * mm, "end": v(-235.87, -47.36) * mm});
            skLineSegment(sketch, "E963", {"start": v(-235.87, -47.36) * mm, "end": v(-234.56, -47.38) * mm});
            skLineSegment(sketch, "E964", {"start": v(-234.56, -47.38) * mm, "end": v(-233.27, -47.56) * mm});
            skLineSegment(sketch, "E965", {"start": v(-233.27, -47.56) * mm, "end": v(-232, -47.88) * mm});
            skLineSegment(sketch, "E966", {"start": v(-232, -47.88) * mm, "end": v(-231.36, -48.2) * mm});
            skLineSegment(sketch, "E967", {"start": v(-231.36, -48.2) * mm, "end": v(-230.79, -48.6) * mm});
            skLineSegment(sketch, "E968", {"start": v(-230.79, -48.6) * mm, "end": v(-230.29, -49.1) * mm});
            skLineSegment(sketch, "E969", {"start": v(-230.29, -49.1) * mm, "end": v(-229.88, -49.7) * mm});
            skLineSegment(sketch, "E970", {"start": v(-229.88, -49.7) * mm, "end": v(-229.44, -50.6) * mm});
            skLineSegment(sketch, "E971", {"start": v(-229.44, -50.6) * mm, "end": v(-229.17, -51.56) * mm});
            skLineSegment(sketch, "E972", {"start": v(-229.17, -51.56) * mm, "end": v(-229.09, -52.56) * mm});
            skLineSegment(sketch, "E973", {"start": v(-229.09, -52.56) * mm, "end": v(-229.15, -53.5) * mm});
            skLineSegment(sketch, "E974", {"start": v(-229.15, -53.5) * mm, "end": v(-229.4, -54.4) * mm});
            skLineSegment(sketch, "E975", {"start": v(-229.4, -54.4) * mm, "end": v(-229.82, -55.24) * mm});
            skLineSegment(sketch, "E976", {"start": v(-229.82, -55.24) * mm, "end": v(-230.4, -55.98) * mm});
            skLineSegment(sketch, "E977", {"start": v(-230.4, -55.98) * mm, "end": v(-230.9, -56.43) * mm});
            skLineSegment(sketch, "E978", {"start": v(-230.9, -56.43) * mm, "end": v(-231.46, -56.81) * mm});
            skLineSegment(sketch, "E979", {"start": v(-231.46, -56.81) * mm, "end": v(-232.07, -57.12) * mm});
            skLineSegment(sketch, "E980", {"start": v(-232.07, -57.12) * mm, "end": v(-233.24, -57.51) * mm});
            skLineSegment(sketch, "E981", {"start": v(-233.24, -57.51) * mm, "end": v(-234.45, -57.75) * mm});
            skLineSegment(sketch, "E982", {"start": v(-234.45, -57.75) * mm, "end": v(-233.57, -58.23) * mm});
            skLineSegment(sketch, "E983", {"start": v(-233.57, -58.23) * mm, "end": v(-232.93, -58.7) * mm});
            skLineSegment(sketch, "E984", {"start": v(-232.93, -58.7) * mm, "end": v(-232.38, -59.25) * mm});
            skLineSegment(sketch, "E985", {"start": v(-232.38, -59.25) * mm, "end": v(-231.86, -59.84) * mm});
            skLineSegment(sketch, "E986", {"start": v(-231.86, -59.84) * mm, "end": v(-230.84, -61.23) * mm});
            skLineSegment(sketch, "E987", {"start": v(-230.84, -61.23) * mm, "end": v(-227.53, -66.41) * mm});
            skLineSegment(sketch, "E988", {"start": v(-227.53, -66.41) * mm, "end": v(-230.7, -66.41) * mm});
            skLineSegment(sketch, "E989", {"start": v(-230.7, -66.41) * mm, "end": v(-233.22, -62.45) * mm});
            skLineSegment(sketch, "E990", {"start": v(-233.22, -62.45) * mm, "end": v(-234.1, -61.12) * mm});
            skLineSegment(sketch, "E991", {"start": v(-234.1, -61.12) * mm, "end": v(-235.04, -59.83) * mm});
            skLineSegment(sketch, "E992", {"start": v(-235.04, -59.83) * mm, "end": v(-235.63, -59.14) * mm});
            skLineSegment(sketch, "E993", {"start": v(-235.63, -59.14) * mm, "end": v(-236.32, -58.55) * mm});
            skLineSegment(sketch, "E994", {"start": v(-236.32, -58.55) * mm, "end": v(-236.87, -58.25) * mm});
            skLineSegment(sketch, "E995", {"start": v(-236.87, -58.25) * mm, "end": v(-237.47, -58.05) * mm});
            skLineSegment(sketch, "E996", {"start": v(-237.47, -58.05) * mm, "end": v(-238.03, -57.98) * mm});
            skLineSegment(sketch, "E997", {"start": v(-238.03, -57.98) * mm, "end": v(-238.87, -57.96) * mm});
            skLineSegment(sketch, "E998", {"start": v(-238.87, -57.96) * mm, "end": v(-241.8, -57.96) * mm});
            skLineSegment(sketch, "E999", {"start": v(-241.8, -57.96) * mm, "end": v(-241.8, -66.41) * mm});
            skLineSegment(sketch, "E1000", {"start": v(-241.8, -66.41) * mm, "end": v(-244.32, -66.41) * mm});
            skLineSegment(sketch, "E1001", {"start": v(-241.8, -55.77) * mm, "end": v(-236.38, -55.77) * mm});
            skLineSegment(sketch, "E1002", {"start": v(-236.38, -55.77) * mm, "end": v(-235.46, -55.75) * mm});
            skLineSegment(sketch, "E1003", {"start": v(-235.46, -55.75) * mm, "end": v(-234.56, -55.64) * mm});
            skLineSegment(sketch, "E1004", {"start": v(-234.56, -55.64) * mm, "end": v(-233.67, -55.41) * mm});
            skLineSegment(sketch, "E1005", {"start": v(-233.67, -55.41) * mm, "end": v(-233.1, -55.15) * mm});
            skLineSegment(sketch, "E1006", {"start": v(-233.1, -55.15) * mm, "end": v(-232.6, -54.76) * mm});
            skLineSegment(sketch, "E1007", {"start": v(-232.6, -54.76) * mm, "end": v(-232.2, -54.27) * mm});
            skLineSegment(sketch, "E1008", {"start": v(-232.2, -54.27) * mm, "end": v(-231.91, -53.74) * mm});
            skLineSegment(sketch, "E1009", {"start": v(-231.91, -53.74) * mm, "end": v(-231.74, -53.16) * mm});
            skLineSegment(sketch, "E1010", {"start": v(-231.74, -53.16) * mm, "end": v(-231.69, -52.56) * mm});
            skLineSegment(sketch, "E1011", {"start": v(-231.69, -52.56) * mm, "end": v(-231.74, -51.94) * mm});
            skLineSegment(sketch, "E1012", {"start": v(-231.74, -51.94) * mm, "end": v(-231.93, -51.34) * mm});
            skLineSegment(sketch, "E1013", {"start": v(-231.93, -51.34) * mm, "end": v(-232.24, -50.8) * mm});
            skLineSegment(sketch, "E1014", {"start": v(-232.24, -50.8) * mm, "end": v(-232.67, -50.34) * mm});
            skLineSegment(sketch, "E1015", {"start": v(-232.67, -50.34) * mm, "end": v(-233.26, -49.94) * mm});
            skLineSegment(sketch, "E1016", {"start": v(-233.26, -49.94) * mm, "end": v(-233.93, -49.69) * mm});
            skLineSegment(sketch, "E1017", {"start": v(-233.93, -49.69) * mm, "end": v(-234.84, -49.52) * mm});
            skLineSegment(sketch, "E1018", {"start": v(-234.84, -49.52) * mm, "end": v(-235.77, -49.47) * mm});
            skLineSegment(sketch, "E1019", {"start": v(-235.77, -49.47) * mm, "end": v(-241.8, -49.47) * mm});
            skLineSegment(sketch, "E1020", {"start": v(-241.8, -49.47) * mm, "end": v(-241.8, -55.77) * mm});
            skLineSegment(sketch, "E1021", {"start": v(-186.57, -79.36) * mm, "end": v(-186.5, -79.07) * mm});
            skLineSegment(sketch, "E1022", {"start": v(-186.5, -79.07) * mm, "end": v(-186.35, -78.83) * mm});
            skLineSegment(sketch, "E1023", {"start": v(-186.35, -78.83) * mm, "end": v(-186.1, -78.67) * mm});
            skLineSegment(sketch, "E1024", {"start": v(-186.1, -78.67) * mm, "end": v(-185.82, -78.6) * mm});
            skLineSegment(sketch, "E1025", {"start": v(-185.82, -78.6) * mm, "end": v(-185.53, -78.67) * mm});
            skLineSegment(sketch, "E1026", {"start": v(-185.53, -78.67) * mm, "end": v(-185.29, -78.83) * mm});
            skLineSegment(sketch, "E1027", {"start": v(-185.29, -78.83) * mm, "end": v(-185.13, -79.07) * mm});
            skLineSegment(sketch, "E1028", {"start": v(-185.13, -79.07) * mm, "end": v(-185.07, -79.36) * mm});
            skLineSegment(sketch, "E1029", {"start": v(-185.07, -79.36) * mm, "end": v(-185.13, -79.64) * mm});
            skLineSegment(sketch, "E1030", {"start": v(-185.13, -79.64) * mm, "end": v(-185.29, -79.89) * mm});
            skLineSegment(sketch, "E1031", {"start": v(-185.29, -79.89) * mm, "end": v(-185.53, -80.05) * mm});
            skLineSegment(sketch, "E1032", {"start": v(-185.53, -80.05) * mm, "end": v(-185.82, -80.1) * mm});
            skLineSegment(sketch, "E1033", {"start": v(-185.82, -80.1) * mm, "end": v(-186.1, -80.05) * mm});
            skLineSegment(sketch, "E1034", {"start": v(-186.1, -80.05) * mm, "end": v(-186.35, -79.89) * mm});
            skLineSegment(sketch, "E1035", {"start": v(-186.35, -79.89) * mm, "end": v(-186.5, -79.64) * mm});
            skLineSegment(sketch, "E1036", {"start": v(-186.5, -79.64) * mm, "end": v(-186.57, -79.36) * mm});
            skLineSegment(sketch, "E1037", {"start": v(-188.85, -81.64) * mm, "end": v(-188.8, -81.36) * mm});
            skLineSegment(sketch, "E1038", {"start": v(-188.8, -81.36) * mm, "end": v(-188.63, -81.11) * mm});
            skLineSegment(sketch, "E1039", {"start": v(-188.63, -81.11) * mm, "end": v(-188.39, -80.95) * mm});
            skLineSegment(sketch, "E1040", {"start": v(-188.39, -80.95) * mm, "end": v(-188.1, -80.9) * mm});
            skLineSegment(sketch, "E1041", {"start": v(-188.1, -80.9) * mm, "end": v(-187.82, -80.95) * mm});
            skLineSegment(sketch, "E1042", {"start": v(-187.82, -80.95) * mm, "end": v(-187.57, -81.11) * mm});
            skLineSegment(sketch, "E1043", {"start": v(-187.57, -81.11) * mm, "end": v(-187.41, -81.36) * mm});
            skLineSegment(sketch, "E1044", {"start": v(-187.41, -81.36) * mm, "end": v(-187.35, -81.64) * mm});
            skLineSegment(sketch, "E1045", {"start": v(-187.35, -81.64) * mm, "end": v(-187.41, -81.93) * mm});
            skLineSegment(sketch, "E1046", {"start": v(-187.41, -81.93) * mm, "end": v(-187.57, -82.17) * mm});
            skLineSegment(sketch, "E1047", {"start": v(-187.57, -82.17) * mm, "end": v(-187.82, -82.33) * mm});
            skLineSegment(sketch, "E1048", {"start": v(-187.82, -82.33) * mm, "end": v(-188.1, -82.4) * mm});
            skLineSegment(sketch, "E1049", {"start": v(-188.1, -82.4) * mm, "end": v(-188.39, -82.33) * mm});
            skLineSegment(sketch, "E1050", {"start": v(-188.39, -82.33) * mm, "end": v(-188.63, -82.17) * mm});
            skLineSegment(sketch, "E1051", {"start": v(-188.63, -82.17) * mm, "end": v(-188.8, -81.93) * mm});
            skLineSegment(sketch, "E1052", {"start": v(-188.8, -81.93) * mm, "end": v(-188.85, -81.64) * mm});
            skLineSegment(sketch, "E1053", {"start": v(-188.85, -79.36) * mm, "end": v(-188.8, -79.07) * mm});
            skLineSegment(sketch, "E1054", {"start": v(-188.8, -79.07) * mm, "end": v(-188.63, -78.83) * mm});
            skLineSegment(sketch, "E1055", {"start": v(-188.63, -78.83) * mm, "end": v(-188.39, -78.67) * mm});
            skLineSegment(sketch, "E1056", {"start": v(-188.39, -78.67) * mm, "end": v(-188.1, -78.6) * mm});
            skLineSegment(sketch, "E1057", {"start": v(-188.1, -78.6) * mm, "end": v(-187.82, -78.67) * mm});
            skLineSegment(sketch, "E1058", {"start": v(-187.82, -78.67) * mm, "end": v(-187.57, -78.83) * mm});
            skLineSegment(sketch, "E1059", {"start": v(-187.57, -78.83) * mm, "end": v(-187.41, -79.07) * mm});
            skLineSegment(sketch, "E1060", {"start": v(-187.41, -79.07) * mm, "end": v(-187.35, -79.36) * mm});
            skLineSegment(sketch, "E1061", {"start": v(-187.35, -79.36) * mm, "end": v(-187.41, -79.64) * mm});
            skLineSegment(sketch, "E1062", {"start": v(-187.41, -79.64) * mm, "end": v(-187.57, -79.89) * mm});
            skLineSegment(sketch, "E1063", {"start": v(-187.57, -79.89) * mm, "end": v(-187.82, -80.05) * mm});
            skLineSegment(sketch, "E1064", {"start": v(-187.82, -80.05) * mm, "end": v(-188.1, -80.1) * mm});
            skLineSegment(sketch, "E1065", {"start": v(-188.1, -80.1) * mm, "end": v(-188.39, -80.05) * mm});
            skLineSegment(sketch, "E1066", {"start": v(-188.39, -80.05) * mm, "end": v(-188.63, -79.89) * mm});
            skLineSegment(sketch, "E1067", {"start": v(-188.63, -79.89) * mm, "end": v(-188.8, -79.64) * mm});
            skLineSegment(sketch, "E1068", {"start": v(-188.8, -79.64) * mm, "end": v(-188.85, -79.36) * mm});
            skLineSegment(sketch, "E1069", {"start": v(-188.87, -77.07) * mm, "end": v(-188.82, -76.78) * mm});
            skLineSegment(sketch, "E1070", {"start": v(-188.82, -76.78) * mm, "end": v(-188.65, -76.54) * mm});
            skLineSegment(sketch, "E1071", {"start": v(-188.65, -76.54) * mm, "end": v(-188.41, -76.38) * mm});
            skLineSegment(sketch, "E1072", {"start": v(-188.41, -76.38) * mm, "end": v(-188.12, -76.32) * mm});
            skLineSegment(sketch, "E1073", {"start": v(-188.12, -76.32) * mm, "end": v(-187.84, -76.38) * mm});
            skLineSegment(sketch, "E1074", {"start": v(-187.84, -76.38) * mm, "end": v(-187.6, -76.54) * mm});
            skLineSegment(sketch, "E1075", {"start": v(-187.6, -76.54) * mm, "end": v(-187.43, -76.78) * mm});
            skLineSegment(sketch, "E1076", {"start": v(-187.43, -76.78) * mm, "end": v(-187.38, -77.07) * mm});
            skLineSegment(sketch, "E1077", {"start": v(-187.38, -77.07) * mm, "end": v(-187.43, -77.36) * mm});
            skLineSegment(sketch, "E1078", {"start": v(-187.43, -77.36) * mm, "end": v(-187.6, -77.6) * mm});
            skLineSegment(sketch, "E1079", {"start": v(-187.6, -77.6) * mm, "end": v(-187.84, -77.76) * mm});
            skLineSegment(sketch, "E1080", {"start": v(-187.84, -77.76) * mm, "end": v(-188.12, -77.82) * mm});
            skLineSegment(sketch, "E1081", {"start": v(-188.12, -77.82) * mm, "end": v(-188.41, -77.76) * mm});
            skLineSegment(sketch, "E1082", {"start": v(-188.41, -77.76) * mm, "end": v(-188.65, -77.6) * mm});
            skLineSegment(sketch, "E1083", {"start": v(-188.65, -77.6) * mm, "end": v(-188.82, -77.36) * mm});
            skLineSegment(sketch, "E1084", {"start": v(-188.82, -77.36) * mm, "end": v(-188.87, -77.07) * mm});
            skLineSegment(sketch, "E1085", {"start": v(-180.44, -79.36) * mm, "end": v(-180.39, -79.07) * mm});
            skLineSegment(sketch, "E1086", {"start": v(-180.39, -79.07) * mm, "end": v(-180.23, -78.83) * mm});
            skLineSegment(sketch, "E1087", {"start": v(-180.23, -78.83) * mm, "end": v(-179.98, -78.67) * mm});
            skLineSegment(sketch, "E1088", {"start": v(-179.98, -78.67) * mm, "end": v(-179.7, -78.6) * mm});
            skLineSegment(sketch, "E1089", {"start": v(-179.7, -78.6) * mm, "end": v(-179.4, -78.67) * mm});
            skLineSegment(sketch, "E1090", {"start": v(-179.4, -78.67) * mm, "end": v(-179.17, -78.83) * mm});
            skLineSegment(sketch, "E1091", {"start": v(-179.17, -78.83) * mm, "end": v(-179, -79.07) * mm});
            skLineSegment(sketch, "E1092", {"start": v(-179, -79.07) * mm, "end": v(-178.95, -79.36) * mm});
            skLineSegment(sketch, "E1093", {"start": v(-178.95, -79.36) * mm, "end": v(-179, -79.64) * mm});
            skLineSegment(sketch, "E1094", {"start": v(-179, -79.64) * mm, "end": v(-179.17, -79.89) * mm});
            skLineSegment(sketch, "E1095", {"start": v(-179.17, -79.89) * mm, "end": v(-179.4, -80.05) * mm});
            skLineSegment(sketch, "E1096", {"start": v(-179.4, -80.05) * mm, "end": v(-179.7, -80.1) * mm});
            skLineSegment(sketch, "E1097", {"start": v(-179.7, -80.1) * mm, "end": v(-179.98, -80.05) * mm});
            skLineSegment(sketch, "E1098", {"start": v(-179.98, -80.05) * mm, "end": v(-180.23, -79.89) * mm});
            skLineSegment(sketch, "E1099", {"start": v(-180.23, -79.89) * mm, "end": v(-180.39, -79.64) * mm});
            skLineSegment(sketch, "E1100", {"start": v(-180.39, -79.64) * mm, "end": v(-180.44, -79.36) * mm});
            skLineSegment(sketch, "E1101", {"start": v(-182.75, -77.07) * mm, "end": v(-182.7, -76.78) * mm});
            skLineSegment(sketch, "E1102", {"start": v(-182.7, -76.78) * mm, "end": v(-182.53, -76.54) * mm});
            skLineSegment(sketch, "E1103", {"start": v(-182.53, -76.54) * mm, "end": v(-182.29, -76.38) * mm});
            skLineSegment(sketch, "E1104", {"start": v(-182.29, -76.38) * mm, "end": v(-182, -76.32) * mm});
            skLineSegment(sketch, "E1105", {"start": v(-182, -76.32) * mm, "end": v(-181.72, -76.38) * mm});
            skLineSegment(sketch, "E1106", {"start": v(-181.72, -76.38) * mm, "end": v(-181.47, -76.54) * mm});
            skLineSegment(sketch, "E1107", {"start": v(-181.47, -76.54) * mm, "end": v(-181.31, -76.78) * mm});
            skLineSegment(sketch, "E1108", {"start": v(-181.31, -76.78) * mm, "end": v(-181.25, -77.07) * mm});
            skLineSegment(sketch, "E1109", {"start": v(-181.25, -77.07) * mm, "end": v(-181.31, -77.36) * mm});
            skLineSegment(sketch, "E1110", {"start": v(-181.31, -77.36) * mm, "end": v(-181.47, -77.6) * mm});
            skLineSegment(sketch, "E1111", {"start": v(-181.47, -77.6) * mm, "end": v(-181.72, -77.76) * mm});
            skLineSegment(sketch, "E1112", {"start": v(-181.72, -77.76) * mm, "end": v(-182, -77.82) * mm});
            skLineSegment(sketch, "E1113", {"start": v(-182, -77.82) * mm, "end": v(-182.29, -77.76) * mm});
            skLineSegment(sketch, "E1114", {"start": v(-182.29, -77.76) * mm, "end": v(-182.53, -77.6) * mm});
            skLineSegment(sketch, "E1115", {"start": v(-182.53, -77.6) * mm, "end": v(-182.7, -77.36) * mm});
            skLineSegment(sketch, "E1116", {"start": v(-182.7, -77.36) * mm, "end": v(-182.75, -77.07) * mm});
            skLineSegment(sketch, "E1117", {"start": v(-176.6, -81.64) * mm, "end": v(-176.55, -81.36) * mm});
            skLineSegment(sketch, "E1118", {"start": v(-176.55, -81.36) * mm, "end": v(-176.39, -81.11) * mm});
            skLineSegment(sketch, "E1119", {"start": v(-176.39, -81.11) * mm, "end": v(-176.15, -80.95) * mm});
            skLineSegment(sketch, "E1120", {"start": v(-176.15, -80.95) * mm, "end": v(-175.86, -80.9) * mm});
            skLineSegment(sketch, "E1121", {"start": v(-175.86, -80.9) * mm, "end": v(-175.57, -80.95) * mm});
            skLineSegment(sketch, "E1122", {"start": v(-175.57, -80.95) * mm, "end": v(-175.33, -81.11) * mm});
            skLineSegment(sketch, "E1123", {"start": v(-175.33, -81.11) * mm, "end": v(-175.17, -81.36) * mm});
            skLineSegment(sketch, "E1124", {"start": v(-175.17, -81.36) * mm, "end": v(-175.11, -81.64) * mm});
            skLineSegment(sketch, "E1125", {"start": v(-175.11, -81.64) * mm, "end": v(-175.17, -81.93) * mm});
            skLineSegment(sketch, "E1126", {"start": v(-175.17, -81.93) * mm, "end": v(-175.33, -82.17) * mm});
            skLineSegment(sketch, "E1127", {"start": v(-175.33, -82.17) * mm, "end": v(-175.57, -82.33) * mm});
            skLineSegment(sketch, "E1128", {"start": v(-175.57, -82.33) * mm, "end": v(-175.86, -82.4) * mm});
            skLineSegment(sketch, "E1129", {"start": v(-175.86, -82.4) * mm, "end": v(-176.15, -82.33) * mm});
            skLineSegment(sketch, "E1130", {"start": v(-176.15, -82.33) * mm, "end": v(-176.39, -82.17) * mm});
            skLineSegment(sketch, "E1131", {"start": v(-176.39, -82.17) * mm, "end": v(-176.55, -81.93) * mm});
            skLineSegment(sketch, "E1132", {"start": v(-176.55, -81.93) * mm, "end": v(-176.6, -81.64) * mm});
            skLineSegment(sketch, "E1133", {"start": v(-174.3, -77.1) * mm, "end": v(-174.24, -76.8) * mm});
            skLineSegment(sketch, "E1134", {"start": v(-174.24, -76.8) * mm, "end": v(-174.08, -76.56) * mm});
            skLineSegment(sketch, "E1135", {"start": v(-174.08, -76.56) * mm, "end": v(-173.84, -76.4) * mm});
            skLineSegment(sketch, "E1136", {"start": v(-173.84, -76.4) * mm, "end": v(-173.55, -76.34) * mm});
            skLineSegment(sketch, "E1137", {"start": v(-173.55, -76.34) * mm, "end": v(-173.27, -76.4) * mm});
            skLineSegment(sketch, "E1138", {"start": v(-173.27, -76.4) * mm, "end": v(-173.02, -76.56) * mm});
            skLineSegment(sketch, "E1139", {"start": v(-173.02, -76.56) * mm, "end": v(-172.86, -76.8) * mm});
            skLineSegment(sketch, "E1140", {"start": v(-172.86, -76.8) * mm, "end": v(-172.8, -77.1) * mm});
            skLineSegment(sketch, "E1141", {"start": v(-172.8, -77.1) * mm, "end": v(-172.86, -77.38) * mm});
            skLineSegment(sketch, "E1142", {"start": v(-172.86, -77.38) * mm, "end": v(-173.02, -77.62) * mm});
            skLineSegment(sketch, "E1143", {"start": v(-173.02, -77.62) * mm, "end": v(-173.27, -77.79) * mm});
            skLineSegment(sketch, "E1144", {"start": v(-173.27, -77.79) * mm, "end": v(-173.55, -77.84) * mm});
            skLineSegment(sketch, "E1145", {"start": v(-173.55, -77.84) * mm, "end": v(-173.84, -77.79) * mm});
            skLineSegment(sketch, "E1146", {"start": v(-173.84, -77.79) * mm, "end": v(-174.08, -77.62) * mm});
            skLineSegment(sketch, "E1147", {"start": v(-174.08, -77.62) * mm, "end": v(-174.24, -77.38) * mm});
            skLineSegment(sketch, "E1148", {"start": v(-174.24, -77.38) * mm, "end": v(-174.3, -77.1) * mm});
            skLineSegment(sketch, "E1149", {"start": v(-168.2, -79.36) * mm, "end": v(-168.14, -79.07) * mm});
            skLineSegment(sketch, "E1150", {"start": v(-168.14, -79.07) * mm, "end": v(-167.98, -78.83) * mm});
            skLineSegment(sketch, "E1151", {"start": v(-167.98, -78.83) * mm, "end": v(-167.74, -78.67) * mm});
            skLineSegment(sketch, "E1152", {"start": v(-167.74, -78.67) * mm, "end": v(-167.45, -78.6) * mm});
            skLineSegment(sketch, "E1153", {"start": v(-167.45, -78.6) * mm, "end": v(-167.17, -78.67) * mm});
            skLineSegment(sketch, "E1154", {"start": v(-167.17, -78.67) * mm, "end": v(-166.92, -78.83) * mm});
            skLineSegment(sketch, "E1155", {"start": v(-166.92, -78.83) * mm, "end": v(-166.76, -79.07) * mm});
            skLineSegment(sketch, "E1156", {"start": v(-166.76, -79.07) * mm, "end": v(-166.7, -79.36) * mm});
            skLineSegment(sketch, "E1157", {"start": v(-166.7, -79.36) * mm, "end": v(-166.76, -79.64) * mm});
            skLineSegment(sketch, "E1158", {"start": v(-166.76, -79.64) * mm, "end": v(-166.92, -79.89) * mm});
            skLineSegment(sketch, "E1159", {"start": v(-166.92, -79.89) * mm, "end": v(-167.17, -80.05) * mm});
            skLineSegment(sketch, "E1160", {"start": v(-167.17, -80.05) * mm, "end": v(-167.45, -80.1) * mm});
            skLineSegment(sketch, "E1161", {"start": v(-167.45, -80.1) * mm, "end": v(-167.74, -80.05) * mm});
            skLineSegment(sketch, "E1162", {"start": v(-167.74, -80.05) * mm, "end": v(-167.98, -79.89) * mm});
            skLineSegment(sketch, "E1163", {"start": v(-167.98, -79.89) * mm, "end": v(-168.14, -79.64) * mm});
            skLineSegment(sketch, "E1164", {"start": v(-168.14, -79.64) * mm, "end": v(-168.2, -79.36) * mm});
            skLineSegment(sketch, "E1165", {"start": v(-170.49, -81.64) * mm, "end": v(-170.43, -81.36) * mm});
            skLineSegment(sketch, "E1166", {"start": v(-170.43, -81.36) * mm, "end": v(-170.27, -81.11) * mm});
            skLineSegment(sketch, "E1167", {"start": v(-170.27, -81.11) * mm, "end": v(-170.02, -80.95) * mm});
            skLineSegment(sketch, "E1168", {"start": v(-170.02, -80.95) * mm, "end": v(-169.74, -80.9) * mm});
            skLineSegment(sketch, "E1169", {"start": v(-169.74, -80.9) * mm, "end": v(-169.45, -80.95) * mm});
            skLineSegment(sketch, "E1170", {"start": v(-169.45, -80.95) * mm, "end": v(-169.2, -81.11) * mm});
            skLineSegment(sketch, "E1171", {"start": v(-169.2, -81.11) * mm, "end": v(-169.05, -81.36) * mm});
            skLineSegment(sketch, "E1172", {"start": v(-169.05, -81.36) * mm, "end": v(-168.99, -81.64) * mm});
            skLineSegment(sketch, "E1173", {"start": v(-168.99, -81.64) * mm, "end": v(-169.05, -81.93) * mm});
            skLineSegment(sketch, "E1174", {"start": v(-169.05, -81.93) * mm, "end": v(-169.2, -82.17) * mm});
            skLineSegment(sketch, "E1175", {"start": v(-169.2, -82.17) * mm, "end": v(-169.45, -82.33) * mm});
            skLineSegment(sketch, "E1176", {"start": v(-169.45, -82.33) * mm, "end": v(-169.74, -82.4) * mm});
            skLineSegment(sketch, "E1177", {"start": v(-169.74, -82.4) * mm, "end": v(-170.02, -82.33) * mm});
            skLineSegment(sketch, "E1178", {"start": v(-170.02, -82.33) * mm, "end": v(-170.27, -82.17) * mm});
            skLineSegment(sketch, "E1179", {"start": v(-170.27, -82.17) * mm, "end": v(-170.43, -81.93) * mm});
            skLineSegment(sketch, "E1180", {"start": v(-170.43, -81.93) * mm, "end": v(-170.49, -81.64) * mm});
            skLineSegment(sketch, "E1181", {"start": v(-170.49, -79.36) * mm, "end": v(-170.43, -79.07) * mm});
            skLineSegment(sketch, "E1182", {"start": v(-170.43, -79.07) * mm, "end": v(-170.27, -78.83) * mm});
            skLineSegment(sketch, "E1183", {"start": v(-170.27, -78.83) * mm, "end": v(-170.02, -78.67) * mm});
            skLineSegment(sketch, "E1184", {"start": v(-170.02, -78.67) * mm, "end": v(-169.74, -78.6) * mm});
            skLineSegment(sketch, "E1185", {"start": v(-169.74, -78.6) * mm, "end": v(-169.45, -78.67) * mm});
            skLineSegment(sketch, "E1186", {"start": v(-169.45, -78.67) * mm, "end": v(-169.2, -78.83) * mm});
            skLineSegment(sketch, "E1187", {"start": v(-169.2, -78.83) * mm, "end": v(-169.05, -79.07) * mm});
            skLineSegment(sketch, "E1188", {"start": v(-169.05, -79.07) * mm, "end": v(-168.99, -79.36) * mm});
            skLineSegment(sketch, "E1189", {"start": v(-168.99, -79.36) * mm, "end": v(-169.05, -79.64) * mm});
            skLineSegment(sketch, "E1190", {"start": v(-169.05, -79.64) * mm, "end": v(-169.2, -79.89) * mm});
            skLineSegment(sketch, "E1191", {"start": v(-169.2, -79.89) * mm, "end": v(-169.45, -80.05) * mm});
            skLineSegment(sketch, "E1192", {"start": v(-169.45, -80.05) * mm, "end": v(-169.74, -80.1) * mm});
            skLineSegment(sketch, "E1193", {"start": v(-169.74, -80.1) * mm, "end": v(-170.02, -80.05) * mm});
            skLineSegment(sketch, "E1194", {"start": v(-170.02, -80.05) * mm, "end": v(-170.27, -79.89) * mm});
            skLineSegment(sketch, "E1195", {"start": v(-170.27, -79.89) * mm, "end": v(-170.43, -79.64) * mm});
            skLineSegment(sketch, "E1196", {"start": v(-170.43, -79.64) * mm, "end": v(-170.49, -79.36) * mm});
            skLineSegment(sketch, "E1197", {"start": v(-170.51, -77.07) * mm, "end": v(-170.45, -76.78) * mm});
            skLineSegment(sketch, "E1198", {"start": v(-170.45, -76.78) * mm, "end": v(-170.3, -76.54) * mm});
            skLineSegment(sketch, "E1199", {"start": v(-170.3, -76.54) * mm, "end": v(-170.05, -76.38) * mm});
            skLineSegment(sketch, "E1200", {"start": v(-170.05, -76.38) * mm, "end": v(-169.76, -76.32) * mm});
            skLineSegment(sketch, "E1201", {"start": v(-169.76, -76.32) * mm, "end": v(-169.47, -76.38) * mm});
            skLineSegment(sketch, "E1202", {"start": v(-169.47, -76.38) * mm, "end": v(-169.23, -76.54) * mm});
            skLineSegment(sketch, "E1203", {"start": v(-169.23, -76.54) * mm, "end": v(-169.07, -76.78) * mm});
            skLineSegment(sketch, "E1204", {"start": v(-169.07, -76.78) * mm, "end": v(-169.01, -77.07) * mm});
            skLineSegment(sketch, "E1205", {"start": v(-169.01, -77.07) * mm, "end": v(-169.07, -77.36) * mm});
            skLineSegment(sketch, "E1206", {"start": v(-169.07, -77.36) * mm, "end": v(-169.23, -77.6) * mm});
            skLineSegment(sketch, "E1207", {"start": v(-169.23, -77.6) * mm, "end": v(-169.47, -77.76) * mm});
            skLineSegment(sketch, "E1208", {"start": v(-169.47, -77.76) * mm, "end": v(-169.76, -77.82) * mm});
            skLineSegment(sketch, "E1209", {"start": v(-169.76, -77.82) * mm, "end": v(-170.05, -77.76) * mm});
            skLineSegment(sketch, "E1210", {"start": v(-170.05, -77.76) * mm, "end": v(-170.3, -77.6) * mm});
            skLineSegment(sketch, "E1211", {"start": v(-170.3, -77.6) * mm, "end": v(-170.45, -77.36) * mm});
            skLineSegment(sketch, "E1212", {"start": v(-170.45, -77.36) * mm, "end": v(-170.51, -77.07) * mm});
            skLineSegment(sketch, "E1213", {"start": v(-162.08, -79.36) * mm, "end": v(-162.02, -79.07) * mm});
            skLineSegment(sketch, "E1214", {"start": v(-162.02, -79.07) * mm, "end": v(-161.86, -78.83) * mm});
            skLineSegment(sketch, "E1215", {"start": v(-161.86, -78.83) * mm, "end": v(-161.62, -78.67) * mm});
            skLineSegment(sketch, "E1216", {"start": v(-161.62, -78.67) * mm, "end": v(-161.33, -78.6) * mm});
            skLineSegment(sketch, "E1217", {"start": v(-161.33, -78.6) * mm, "end": v(-161.04, -78.67) * mm});
            skLineSegment(sketch, "E1218", {"start": v(-161.04, -78.67) * mm, "end": v(-160.8, -78.83) * mm});
            skLineSegment(sketch, "E1219", {"start": v(-160.8, -78.83) * mm, "end": v(-160.64, -79.07) * mm});
            skLineSegment(sketch, "E1220", {"start": v(-160.64, -79.07) * mm, "end": v(-160.58, -79.36) * mm});
            skLineSegment(sketch, "E1221", {"start": v(-160.58, -79.36) * mm, "end": v(-160.64, -79.64) * mm});
            skLineSegment(sketch, "E1222", {"start": v(-160.64, -79.64) * mm, "end": v(-160.8, -79.89) * mm});
            skLineSegment(sketch, "E1223", {"start": v(-160.8, -79.89) * mm, "end": v(-161.04, -80.05) * mm});
            skLineSegment(sketch, "E1224", {"start": v(-161.04, -80.05) * mm, "end": v(-161.33, -80.1) * mm});
            skLineSegment(sketch, "E1225", {"start": v(-161.33, -80.1) * mm, "end": v(-161.62, -80.05) * mm});
            skLineSegment(sketch, "E1226", {"start": v(-161.62, -80.05) * mm, "end": v(-161.86, -79.89) * mm});
            skLineSegment(sketch, "E1227", {"start": v(-161.86, -79.89) * mm, "end": v(-162.02, -79.64) * mm});
            skLineSegment(sketch, "E1228", {"start": v(-162.02, -79.64) * mm, "end": v(-162.08, -79.36) * mm});
            skLineSegment(sketch, "E1229", {"start": v(-164.37, -81.64) * mm, "end": v(-164.3, -81.36) * mm});
            skLineSegment(sketch, "E1230", {"start": v(-164.3, -81.36) * mm, "end": v(-164.15, -81.11) * mm});
            skLineSegment(sketch, "E1231", {"start": v(-164.15, -81.11) * mm, "end": v(-163.9, -80.95) * mm});
            skLineSegment(sketch, "E1232", {"start": v(-163.9, -80.95) * mm, "end": v(-163.62, -80.9) * mm});
            skLineSegment(sketch, "E1233", {"start": v(-163.62, -80.9) * mm, "end": v(-163.33, -80.95) * mm});
            skLineSegment(sketch, "E1234", {"start": v(-163.33, -80.95) * mm, "end": v(-163.09, -81.11) * mm});
            skLineSegment(sketch, "E1235", {"start": v(-163.09, -81.11) * mm, "end": v(-162.93, -81.36) * mm});
            skLineSegment(sketch, "E1236", {"start": v(-162.93, -81.36) * mm, "end": v(-162.87, -81.64) * mm});
            skLineSegment(sketch, "E1237", {"start": v(-162.87, -81.64) * mm, "end": v(-162.93, -81.93) * mm});
            skLineSegment(sketch, "E1238", {"start": v(-162.93, -81.93) * mm, "end": v(-163.09, -82.17) * mm});
            skLineSegment(sketch, "E1239", {"start": v(-163.09, -82.17) * mm, "end": v(-163.33, -82.33) * mm});
            skLineSegment(sketch, "E1240", {"start": v(-163.33, -82.33) * mm, "end": v(-163.62, -82.4) * mm});
            skLineSegment(sketch, "E1241", {"start": v(-163.62, -82.4) * mm, "end": v(-163.9, -82.33) * mm});
            skLineSegment(sketch, "E1242", {"start": v(-163.9, -82.33) * mm, "end": v(-164.15, -82.17) * mm});
            skLineSegment(sketch, "E1243", {"start": v(-164.15, -82.17) * mm, "end": v(-164.3, -81.93) * mm});
            skLineSegment(sketch, "E1244", {"start": v(-164.3, -81.93) * mm, "end": v(-164.37, -81.64) * mm});
            skLineSegment(sketch, "E1245", {"start": v(-164.39, -77.07) * mm, "end": v(-164.33, -76.78) * mm});
            skLineSegment(sketch, "E1246", {"start": v(-164.33, -76.78) * mm, "end": v(-164.17, -76.54) * mm});
            skLineSegment(sketch, "E1247", {"start": v(-164.17, -76.54) * mm, "end": v(-163.93, -76.38) * mm});
            skLineSegment(sketch, "E1248", {"start": v(-163.93, -76.38) * mm, "end": v(-163.64, -76.32) * mm});
            skLineSegment(sketch, "E1249", {"start": v(-163.64, -76.32) * mm, "end": v(-163.35, -76.38) * mm});
            skLineSegment(sketch, "E1250", {"start": v(-163.35, -76.38) * mm, "end": v(-163.1, -76.54) * mm});
            skLineSegment(sketch, "E1251", {"start": v(-163.1, -76.54) * mm, "end": v(-162.95, -76.78) * mm});
            skLineSegment(sketch, "E1252", {"start": v(-162.95, -76.78) * mm, "end": v(-162.9, -77.07) * mm});
            skLineSegment(sketch, "E1253", {"start": v(-162.9, -77.07) * mm, "end": v(-162.95, -77.36) * mm});
            skLineSegment(sketch, "E1254", {"start": v(-162.95, -77.36) * mm, "end": v(-163.1, -77.6) * mm});
            skLineSegment(sketch, "E1255", {"start": v(-163.1, -77.6) * mm, "end": v(-163.35, -77.76) * mm});
            skLineSegment(sketch, "E1256", {"start": v(-163.35, -77.76) * mm, "end": v(-163.64, -77.82) * mm});
            skLineSegment(sketch, "E1257", {"start": v(-163.64, -77.82) * mm, "end": v(-163.93, -77.76) * mm});
            skLineSegment(sketch, "E1258", {"start": v(-163.93, -77.76) * mm, "end": v(-164.17, -77.6) * mm});
            skLineSegment(sketch, "E1259", {"start": v(-164.17, -77.6) * mm, "end": v(-164.33, -77.36) * mm});
            skLineSegment(sketch, "E1260", {"start": v(-164.33, -77.36) * mm, "end": v(-164.39, -77.07) * mm});
            skLineSegment(sketch, "E1261", {"start": v(-155.96, -79.36) * mm, "end": v(-155.9, -79.07) * mm});
            skLineSegment(sketch, "E1262", {"start": v(-155.9, -79.07) * mm, "end": v(-155.74, -78.83) * mm});
            skLineSegment(sketch, "E1263", {"start": v(-155.74, -78.83) * mm, "end": v(-155.5, -78.67) * mm});
            skLineSegment(sketch, "E1264", {"start": v(-155.5, -78.67) * mm, "end": v(-155.2, -78.6) * mm});
            skLineSegment(sketch, "E1265", {"start": v(-155.2, -78.6) * mm, "end": v(-154.92, -78.67) * mm});
            skLineSegment(sketch, "E1266", {"start": v(-154.92, -78.67) * mm, "end": v(-154.68, -78.83) * mm});
            skLineSegment(sketch, "E1267", {"start": v(-154.68, -78.83) * mm, "end": v(-154.52, -79.07) * mm});
            skLineSegment(sketch, "E1268", {"start": v(-154.52, -79.07) * mm, "end": v(-154.46, -79.36) * mm});
            skLineSegment(sketch, "E1269", {"start": v(-154.46, -79.36) * mm, "end": v(-154.52, -79.64) * mm});
            skLineSegment(sketch, "E1270", {"start": v(-154.52, -79.64) * mm, "end": v(-154.68, -79.89) * mm});
            skLineSegment(sketch, "E1271", {"start": v(-154.68, -79.89) * mm, "end": v(-154.92, -80.05) * mm});
            skLineSegment(sketch, "E1272", {"start": v(-154.92, -80.05) * mm, "end": v(-155.2, -80.1) * mm});
            skLineSegment(sketch, "E1273", {"start": v(-155.2, -80.1) * mm, "end": v(-155.5, -80.05) * mm});
            skLineSegment(sketch, "E1274", {"start": v(-155.5, -80.05) * mm, "end": v(-155.74, -79.89) * mm});
            skLineSegment(sketch, "E1275", {"start": v(-155.74, -79.89) * mm, "end": v(-155.9, -79.64) * mm});
            skLineSegment(sketch, "E1276", {"start": v(-155.9, -79.64) * mm, "end": v(-155.96, -79.36) * mm});
            skLineSegment(sketch, "E1277", {"start": v(-158.24, -81.64) * mm, "end": v(-158.19, -81.36) * mm});
            skLineSegment(sketch, "E1278", {"start": v(-158.19, -81.36) * mm, "end": v(-158.03, -81.11) * mm});
            skLineSegment(sketch, "E1279", {"start": v(-158.03, -81.11) * mm, "end": v(-157.78, -80.95) * mm});
            skLineSegment(sketch, "E1280", {"start": v(-157.78, -80.95) * mm, "end": v(-157.5, -80.9) * mm});
            skLineSegment(sketch, "E1281", {"start": v(-157.5, -80.9) * mm, "end": v(-157.2, -80.95) * mm});
            skLineSegment(sketch, "E1282", {"start": v(-157.2, -80.95) * mm, "end": v(-156.97, -81.11) * mm});
            skLineSegment(sketch, "E1283", {"start": v(-156.97, -81.11) * mm, "end": v(-156.8, -81.36) * mm});
            skLineSegment(sketch, "E1284", {"start": v(-156.8, -81.36) * mm, "end": v(-156.75, -81.64) * mm});
            skLineSegment(sketch, "E1285", {"start": v(-156.75, -81.64) * mm, "end": v(-156.8, -81.93) * mm});
            skLineSegment(sketch, "E1286", {"start": v(-156.8, -81.93) * mm, "end": v(-156.97, -82.17) * mm});
            skLineSegment(sketch, "E1287", {"start": v(-156.97, -82.17) * mm, "end": v(-157.2, -82.33) * mm});
            skLineSegment(sketch, "E1288", {"start": v(-157.2, -82.33) * mm, "end": v(-157.5, -82.4) * mm});
            skLineSegment(sketch, "E1289", {"start": v(-157.5, -82.4) * mm, "end": v(-157.78, -82.33) * mm});
            skLineSegment(sketch, "E1290", {"start": v(-157.78, -82.33) * mm, "end": v(-158.03, -82.17) * mm});
            skLineSegment(sketch, "E1291", {"start": v(-158.03, -82.17) * mm, "end": v(-158.19, -81.93) * mm});
            skLineSegment(sketch, "E1292", {"start": v(-158.19, -81.93) * mm, "end": v(-158.24, -81.64) * mm});
            skLineSegment(sketch, "E1293", {"start": v(-158.27, -77.07) * mm, "end": v(-158.2, -76.78) * mm});
            skLineSegment(sketch, "E1294", {"start": v(-158.2, -76.78) * mm, "end": v(-158.05, -76.54) * mm});
            skLineSegment(sketch, "E1295", {"start": v(-158.05, -76.54) * mm, "end": v(-157.8, -76.38) * mm});
            skLineSegment(sketch, "E1296", {"start": v(-157.8, -76.38) * mm, "end": v(-157.52, -76.32) * mm});
            skLineSegment(sketch, "E1297", {"start": v(-157.52, -76.32) * mm, "end": v(-157.23, -76.38) * mm});
            skLineSegment(sketch, "E1298", {"start": v(-157.23, -76.38) * mm, "end": v(-156.99, -76.54) * mm});
            skLineSegment(sketch, "E1299", {"start": v(-156.99, -76.54) * mm, "end": v(-156.83, -76.78) * mm});
            skLineSegment(sketch, "E1300", {"start": v(-156.83, -76.78) * mm, "end": v(-156.77, -77.07) * mm});
            skLineSegment(sketch, "E1301", {"start": v(-156.77, -77.07) * mm, "end": v(-156.83, -77.36) * mm});
            skLineSegment(sketch, "E1302", {"start": v(-156.83, -77.36) * mm, "end": v(-156.99, -77.6) * mm});
            skLineSegment(sketch, "E1303", {"start": v(-156.99, -77.6) * mm, "end": v(-157.23, -77.76) * mm});
            skLineSegment(sketch, "E1304", {"start": v(-157.23, -77.76) * mm, "end": v(-157.52, -77.82) * mm});
            skLineSegment(sketch, "E1305", {"start": v(-157.52, -77.82) * mm, "end": v(-157.8, -77.76) * mm});
            skLineSegment(sketch, "E1306", {"start": v(-157.8, -77.76) * mm, "end": v(-158.05, -77.6) * mm});
            skLineSegment(sketch, "E1307", {"start": v(-158.05, -77.6) * mm, "end": v(-158.2, -77.36) * mm});
            skLineSegment(sketch, "E1308", {"start": v(-158.2, -77.36) * mm, "end": v(-158.27, -77.07) * mm});
            skLineSegment(sketch, "E1309", {"start": v(-152.12, -81.64) * mm, "end": v(-152.07, -81.36) * mm});
            skLineSegment(sketch, "E1310", {"start": v(-152.07, -81.36) * mm, "end": v(-151.9, -81.11) * mm});
            skLineSegment(sketch, "E1311", {"start": v(-151.9, -81.11) * mm, "end": v(-151.66, -80.95) * mm});
            skLineSegment(sketch, "E1312", {"start": v(-151.66, -80.95) * mm, "end": v(-151.37, -80.9) * mm});
            skLineSegment(sketch, "E1313", {"start": v(-151.37, -80.9) * mm, "end": v(-151.09, -80.95) * mm});
            skLineSegment(sketch, "E1314", {"start": v(-151.09, -80.95) * mm, "end": v(-150.84, -81.11) * mm});
            skLineSegment(sketch, "E1315", {"start": v(-150.84, -81.11) * mm, "end": v(-150.68, -81.36) * mm});
            skLineSegment(sketch, "E1316", {"start": v(-150.68, -81.36) * mm, "end": v(-150.62, -81.64) * mm});
            skLineSegment(sketch, "E1317", {"start": v(-150.62, -81.64) * mm, "end": v(-150.68, -81.93) * mm});
            skLineSegment(sketch, "E1318", {"start": v(-150.68, -81.93) * mm, "end": v(-150.84, -82.17) * mm});
            skLineSegment(sketch, "E1319", {"start": v(-150.84, -82.17) * mm, "end": v(-151.09, -82.33) * mm});
            skLineSegment(sketch, "E1320", {"start": v(-151.09, -82.33) * mm, "end": v(-151.37, -82.4) * mm});
            skLineSegment(sketch, "E1321", {"start": v(-151.37, -82.4) * mm, "end": v(-151.66, -82.33) * mm});
            skLineSegment(sketch, "E1322", {"start": v(-151.66, -82.33) * mm, "end": v(-151.9, -82.17) * mm});
            skLineSegment(sketch, "E1323", {"start": v(-151.9, -82.17) * mm, "end": v(-152.07, -81.93) * mm});
            skLineSegment(sketch, "E1324", {"start": v(-152.07, -81.93) * mm, "end": v(-152.12, -81.64) * mm});
            skLineSegment(sketch, "E1325", {"start": v(-149.82, -77.1) * mm, "end": v(-149.76, -76.8) * mm});
            skLineSegment(sketch, "E1326", {"start": v(-149.76, -76.8) * mm, "end": v(-149.6, -76.56) * mm});
            skLineSegment(sketch, "E1327", {"start": v(-149.6, -76.56) * mm, "end": v(-149.35, -76.4) * mm});
            skLineSegment(sketch, "E1328", {"start": v(-149.35, -76.4) * mm, "end": v(-149.07, -76.34) * mm});
            skLineSegment(sketch, "E1329", {"start": v(-149.07, -76.34) * mm, "end": v(-148.78, -76.4) * mm});
            skLineSegment(sketch, "E1330", {"start": v(-148.78, -76.4) * mm, "end": v(-148.54, -76.56) * mm});
            skLineSegment(sketch, "E1331", {"start": v(-148.54, -76.56) * mm, "end": v(-148.37, -76.8) * mm});
            skLineSegment(sketch, "E1332", {"start": v(-148.37, -76.8) * mm, "end": v(-148.32, -77.1) * mm});
            skLineSegment(sketch, "E1333", {"start": v(-148.32, -77.1) * mm, "end": v(-148.37, -77.38) * mm});
            skLineSegment(sketch, "E1334", {"start": v(-148.37, -77.38) * mm, "end": v(-148.54, -77.62) * mm});
            skLineSegment(sketch, "E1335", {"start": v(-148.54, -77.62) * mm, "end": v(-148.78, -77.79) * mm});
            skLineSegment(sketch, "E1336", {"start": v(-148.78, -77.79) * mm, "end": v(-149.07, -77.84) * mm});
            skLineSegment(sketch, "E1337", {"start": v(-149.07, -77.84) * mm, "end": v(-149.35, -77.79) * mm});
            skLineSegment(sketch, "E1338", {"start": v(-149.35, -77.79) * mm, "end": v(-149.6, -77.62) * mm});
            skLineSegment(sketch, "E1339", {"start": v(-149.6, -77.62) * mm, "end": v(-149.76, -77.38) * mm});
            skLineSegment(sketch, "E1340", {"start": v(-149.76, -77.38) * mm, "end": v(-149.82, -77.1) * mm});
            skLineSegment(sketch, "E1341", {"start": v(-152.15, -77.07) * mm, "end": v(-152.09, -76.78) * mm});
            skLineSegment(sketch, "E1342", {"start": v(-152.09, -76.78) * mm, "end": v(-151.93, -76.54) * mm});
            skLineSegment(sketch, "E1343", {"start": v(-151.93, -76.54) * mm, "end": v(-151.68, -76.38) * mm});
            skLineSegment(sketch, "E1344", {"start": v(-151.68, -76.38) * mm, "end": v(-151.4, -76.32) * mm});
            skLineSegment(sketch, "E1345", {"start": v(-151.4, -76.32) * mm, "end": v(-151.11, -76.38) * mm});
            skLineSegment(sketch, "E1346", {"start": v(-151.11, -76.38) * mm, "end": v(-150.87, -76.54) * mm});
            skLineSegment(sketch, "E1347", {"start": v(-150.87, -76.54) * mm, "end": v(-150.7, -76.78) * mm});
            skLineSegment(sketch, "E1348", {"start": v(-150.7, -76.78) * mm, "end": v(-150.65, -77.07) * mm});
            skLineSegment(sketch, "E1349", {"start": v(-150.65, -77.07) * mm, "end": v(-150.7, -77.36) * mm});
            skLineSegment(sketch, "E1350", {"start": v(-150.7, -77.36) * mm, "end": v(-150.87, -77.6) * mm});
            skLineSegment(sketch, "E1351", {"start": v(-150.87, -77.6) * mm, "end": v(-151.11, -77.76) * mm});
            skLineSegment(sketch, "E1352", {"start": v(-151.11, -77.76) * mm, "end": v(-151.4, -77.82) * mm});
            skLineSegment(sketch, "E1353", {"start": v(-151.4, -77.82) * mm, "end": v(-151.68, -77.76) * mm});
            skLineSegment(sketch, "E1354", {"start": v(-151.68, -77.76) * mm, "end": v(-151.93, -77.6) * mm});
            skLineSegment(sketch, "E1355", {"start": v(-151.93, -77.6) * mm, "end": v(-152.09, -77.36) * mm});
            skLineSegment(sketch, "E1356", {"start": v(-152.09, -77.36) * mm, "end": v(-152.15, -77.07) * mm});
            skLineSegment(sketch, "E1357", {"start": v(-75.05, -119.02) * mm, "end": v(-46.7, 95.32) * mm});
            skLineSegment(sketch, "E1358", {"start": v(-46.7, 95.32) * mm, "end": v(-290.49, 166.29) * mm});
            skLineSegment(sketch, "E1359", {"start": v(-290.49, 166.29) * mm, "end": v(-261.83, -119.05) * mm});
            skLineSegment(sketch, "E1360", {"start": v(-261.83, -119.05) * mm, "end": v(-75.05, -119.02) * mm});
            skLineSegment(sketch, "E1361", {"start": v(-88.87, -98.01) * mm, "end": v(-64.71, 84.67) * mm});
            skLineSegment(sketch, "E1362", {"start": v(-64.71, 84.67) * mm, "end": v(-272.48, 145.15) * mm});
            skLineSegment(sketch, "E1363", {"start": v(-272.48, 145.15) * mm, "end": v(-248.63, -98) * mm});
            skLineSegment(sketch, "E1364", {"start": v(-248.63, -98) * mm, "end": v(-88.87, -98.01) * mm});
            skLineSegment(sketch, "E1365", {"start": v(-251.47, 115.27) * mm, "end": v(-252.27, 115.34) * mm});
            skLineSegment(sketch, "E1366", {"start": v(-252.27, 115.34) * mm, "end": v(-253.05, 115.55) * mm});
            skLineSegment(sketch, "E1367", {"start": v(-253.05, 115.55) * mm, "end": v(-253.77, 115.89) * mm});
            skLineSegment(sketch, "E1368", {"start": v(-253.77, 115.89) * mm, "end": v(-254.28, 116.22) * mm});
            skLineSegment(sketch, "E1369", {"start": v(-254.28, 116.22) * mm, "end": v(-254.73, 116.62) * mm});
            skLineSegment(sketch, "E1370", {"start": v(-254.73, 116.62) * mm, "end": v(-255.3, 117.32) * mm});
            skLineSegment(sketch, "E1371", {"start": v(-255.3, 117.32) * mm, "end": v(-255.73, 118.12) * mm});
            skLineSegment(sketch, "E1372", {"start": v(-255.73, 118.12) * mm, "end": v(-256, 118.98) * mm});
            skLineSegment(sketch, "E1373", {"start": v(-256, 118.98) * mm, "end": v(-256.08, 119.88) * mm});
            skLineSegment(sketch, "E1374", {"start": v(-256.08, 119.88) * mm, "end": v(-256, 120.68) * mm});
            skLineSegment(sketch, "E1375", {"start": v(-256, 120.68) * mm, "end": v(-255.8, 121.46) * mm});
            skLineSegment(sketch, "E1376", {"start": v(-255.8, 121.46) * mm, "end": v(-255.46, 122.18) * mm});
            skLineSegment(sketch, "E1377", {"start": v(-255.46, 122.18) * mm, "end": v(-255.13, 122.69) * mm});
            skLineSegment(sketch, "E1378", {"start": v(-255.13, 122.69) * mm, "end": v(-254.73, 123.14) * mm});
            skLineSegment(sketch, "E1379", {"start": v(-254.73, 123.14) * mm, "end": v(-254.03, 123.71) * mm});
            skLineSegment(sketch, "E1380", {"start": v(-254.03, 123.71) * mm, "end": v(-253.24, 124.14) * mm});
            skLineSegment(sketch, "E1381", {"start": v(-253.24, 124.14) * mm, "end": v(-252.37, 124.4) * mm});
            skLineSegment(sketch, "E1382", {"start": v(-252.37, 124.4) * mm, "end": v(-251.47, 124.49) * mm});
            skLineSegment(sketch, "E1383", {"start": v(-251.47, 124.49) * mm, "end": v(-250.67, 124.42) * mm});
            skLineSegment(sketch, "E1384", {"start": v(-250.67, 124.42) * mm, "end": v(-249.9, 124.21) * mm});
            skLineSegment(sketch, "E1385", {"start": v(-249.9, 124.21) * mm, "end": v(-249.17, 123.87) * mm});
            skLineSegment(sketch, "E1386", {"start": v(-249.17, 123.87) * mm, "end": v(-248.66, 123.54) * mm});
            skLineSegment(sketch, "E1387", {"start": v(-248.66, 123.54) * mm, "end": v(-248.21, 123.14) * mm});
            skLineSegment(sketch, "E1388", {"start": v(-248.21, 123.14) * mm, "end": v(-247.64, 122.44) * mm});
            skLineSegment(sketch, "E1389", {"start": v(-247.64, 122.44) * mm, "end": v(-247.2, 121.65) * mm});
            skLineSegment(sketch, "E1390", {"start": v(-247.2, 121.65) * mm, "end": v(-246.95, 120.78) * mm});
            skLineSegment(sketch, "E1391", {"start": v(-246.95, 120.78) * mm, "end": v(-246.86, 119.88) * mm});
            skLineSegment(sketch, "E1392", {"start": v(-246.86, 119.88) * mm, "end": v(-246.93, 119.08) * mm});
            skLineSegment(sketch, "E1393", {"start": v(-246.93, 119.08) * mm, "end": v(-247.14, 118.3) * mm});
            skLineSegment(sketch, "E1394", {"start": v(-247.14, 118.3) * mm, "end": v(-247.48, 117.58) * mm});
            skLineSegment(sketch, "E1395", {"start": v(-247.48, 117.58) * mm, "end": v(-247.81, 117.07) * mm});
            skLineSegment(sketch, "E1396", {"start": v(-247.81, 117.07) * mm, "end": v(-248.21, 116.62) * mm});
            skLineSegment(sketch, "E1397", {"start": v(-248.21, 116.62) * mm, "end": v(-248.9, 116.05) * mm});
            skLineSegment(sketch, "E1398", {"start": v(-248.9, 116.05) * mm, "end": v(-249.7, 115.62) * mm});
            skLineSegment(sketch, "E1399", {"start": v(-249.7, 115.62) * mm, "end": v(-250.57, 115.36) * mm});
            skLineSegment(sketch, "E1400", {"start": v(-250.57, 115.36) * mm, "end": v(-251.47, 115.27) * mm});
            skLineSegment(sketch, "E1401", {"start": v(-85.2, 66.76) * mm, "end": v(-86, 66.83) * mm});
            skLineSegment(sketch, "E1402", {"start": v(-86, 66.83) * mm, "end": v(-86.78, 67.04) * mm});
            skLineSegment(sketch, "E1403", {"start": v(-86.78, 67.04) * mm, "end": v(-87.5, 67.38) * mm});
            skLineSegment(sketch, "E1404", {"start": v(-87.5, 67.38) * mm, "end": v(-88, 67.72) * mm});
            skLineSegment(sketch, "E1405", {"start": v(-88, 67.72) * mm, "end": v(-88.46, 68.11) * mm});
            skLineSegment(sketch, "E1406", {"start": v(-88.46, 68.11) * mm, "end": v(-89.04, 68.81) * mm});
            skLineSegment(sketch, "E1407", {"start": v(-89.04, 68.81) * mm, "end": v(-89.46, 69.6) * mm});
            skLineSegment(sketch, "E1408", {"start": v(-89.46, 69.6) * mm, "end": v(-89.72, 70.47) * mm});
            skLineSegment(sketch, "E1409", {"start": v(-89.72, 70.47) * mm, "end": v(-89.81, 71.37) * mm});
            skLineSegment(sketch, "E1410", {"start": v(-89.81, 71.37) * mm, "end": v(-89.74, 72.17) * mm});
            skLineSegment(sketch, "E1411", {"start": v(-89.74, 72.17) * mm, "end": v(-89.53, 72.95) * mm});
            skLineSegment(sketch, "E1412", {"start": v(-89.53, 72.95) * mm, "end": v(-89.2, 73.68) * mm});
            skLineSegment(sketch, "E1413", {"start": v(-89.2, 73.68) * mm, "end": v(-88.86, 74.18) * mm});
            skLineSegment(sketch, "E1414", {"start": v(-88.86, 74.18) * mm, "end": v(-88.46, 74.63) * mm});
            skLineSegment(sketch, "E1415", {"start": v(-88.46, 74.63) * mm, "end": v(-87.76, 75.2) * mm});
            skLineSegment(sketch, "E1416", {"start": v(-87.76, 75.2) * mm, "end": v(-86.97, 75.63) * mm});
            skLineSegment(sketch, "E1417", {"start": v(-86.97, 75.63) * mm, "end": v(-86.1, 75.9) * mm});
            skLineSegment(sketch, "E1418", {"start": v(-86.1, 75.9) * mm, "end": v(-85.2, 75.98) * mm});
            skLineSegment(sketch, "E1419", {"start": v(-85.2, 75.98) * mm, "end": v(-84.4, 75.91) * mm});
            skLineSegment(sketch, "E1420", {"start": v(-84.4, 75.91) * mm, "end": v(-83.62, 75.7) * mm});
            skLineSegment(sketch, "E1421", {"start": v(-83.62, 75.7) * mm, "end": v(-82.9, 75.36) * mm});
            skLineSegment(sketch, "E1422", {"start": v(-82.9, 75.36) * mm, "end": v(-82.4, 75.03) * mm});
            skLineSegment(sketch, "E1423", {"start": v(-82.4, 75.03) * mm, "end": v(-81.94, 74.63) * mm});
            skLineSegment(sketch, "E1424", {"start": v(-81.94, 74.63) * mm, "end": v(-81.37, 73.93) * mm});
            skLineSegment(sketch, "E1425", {"start": v(-81.37, 73.93) * mm, "end": v(-80.94, 73.14) * mm});
            skLineSegment(sketch, "E1426", {"start": v(-80.94, 73.14) * mm, "end": v(-80.68, 72.27) * mm});
            skLineSegment(sketch, "E1427", {"start": v(-80.68, 72.27) * mm, "end": v(-80.6, 71.37) * mm});
            skLineSegment(sketch, "E1428", {"start": v(-80.6, 71.37) * mm, "end": v(-80.66, 70.57) * mm});
            skLineSegment(sketch, "E1429", {"start": v(-80.66, 70.57) * mm, "end": v(-80.87, 69.8) * mm});
            skLineSegment(sketch, "E1430", {"start": v(-80.87, 69.8) * mm, "end": v(-81.2, 69.07) * mm});
            skLineSegment(sketch, "E1431", {"start": v(-81.2, 69.07) * mm, "end": v(-81.54, 68.57) * mm});
            skLineSegment(sketch, "E1432", {"start": v(-81.54, 68.57) * mm, "end": v(-81.94, 68.11) * mm});
            skLineSegment(sketch, "E1433", {"start": v(-81.94, 68.11) * mm, "end": v(-82.64, 67.54) * mm});
            skLineSegment(sketch, "E1434", {"start": v(-82.64, 67.54) * mm, "end": v(-83.44, 67.11) * mm});
            skLineSegment(sketch, "E1435", {"start": v(-83.44, 67.11) * mm, "end": v(-84.3, 66.85) * mm});
            skLineSegment(sketch, "E1436", {"start": v(-84.3, 66.85) * mm, "end": v(-85.2, 66.76) * mm});
            skLineSegment(sketch, "E1437", {"start": v(-105.08, -84.21) * mm, "end": v(-105.88, -84.14) * mm});
            skLineSegment(sketch, "E1438", {"start": v(-105.88, -84.14) * mm, "end": v(-106.66, -83.94) * mm});
            skLineSegment(sketch, "E1439", {"start": v(-106.66, -83.94) * mm, "end": v(-107.39, -83.6) * mm});
            skLineSegment(sketch, "E1440", {"start": v(-107.39, -83.6) * mm, "end": v(-107.89, -83.26) * mm});
            skLineSegment(sketch, "E1441", {"start": v(-107.89, -83.26) * mm, "end": v(-108.34, -82.86) * mm});
            skLineSegment(sketch, "E1442", {"start": v(-108.34, -82.86) * mm, "end": v(-108.92, -82.17) * mm});
            skLineSegment(sketch, "E1443", {"start": v(-108.92, -82.17) * mm, "end": v(-109.34, -81.37) * mm});
            skLineSegment(sketch, "E1444", {"start": v(-109.34, -81.37) * mm, "end": v(-109.6, -80.5) * mm});
            skLineSegment(sketch, "E1445", {"start": v(-109.6, -80.5) * mm, "end": v(-109.7, -79.6) * mm});
            skLineSegment(sketch, "E1446", {"start": v(-109.7, -79.6) * mm, "end": v(-109.62, -78.8) * mm});
            skLineSegment(sketch, "E1447", {"start": v(-109.62, -78.8) * mm, "end": v(-109.41, -78.03) * mm});
            skLineSegment(sketch, "E1448", {"start": v(-109.41, -78.03) * mm, "end": v(-109.07, -77.3) * mm});
            skLineSegment(sketch, "E1449", {"start": v(-109.07, -77.3) * mm, "end": v(-108.74, -76.8) * mm});
            skLineSegment(sketch, "E1450", {"start": v(-108.74, -76.8) * mm, "end": v(-108.34, -76.35) * mm});
            skLineSegment(sketch, "E1451", {"start": v(-108.34, -76.35) * mm, "end": v(-107.64, -75.77) * mm});
            skLineSegment(sketch, "E1452", {"start": v(-107.64, -75.77) * mm, "end": v(-106.85, -75.34) * mm});
            skLineSegment(sketch, "E1453", {"start": v(-106.85, -75.34) * mm, "end": v(-105.98, -75.08) * mm});
            skLineSegment(sketch, "E1454", {"start": v(-105.98, -75.08) * mm, "end": v(-105.08, -75) * mm});
            skLineSegment(sketch, "E1455", {"start": v(-105.08, -75) * mm, "end": v(-104.28, -75.07) * mm});
            skLineSegment(sketch, "E1456", {"start": v(-104.28, -75.07) * mm, "end": v(-103.5, -75.27) * mm});
            skLineSegment(sketch, "E1457", {"start": v(-103.5, -75.27) * mm, "end": v(-102.78, -75.61) * mm});
            skLineSegment(sketch, "E1458", {"start": v(-102.78, -75.61) * mm, "end": v(-102.28, -75.95) * mm});
            skLineSegment(sketch, "E1459", {"start": v(-102.28, -75.95) * mm, "end": v(-101.82, -76.35) * mm});
            skLineSegment(sketch, "E1460", {"start": v(-101.82, -76.35) * mm, "end": v(-101.25, -77.04) * mm});
            skLineSegment(sketch, "E1461", {"start": v(-101.25, -77.04) * mm, "end": v(-100.82, -77.84) * mm});
            skLineSegment(sketch, "E1462", {"start": v(-100.82, -77.84) * mm, "end": v(-100.56, -78.7) * mm});
            skLineSegment(sketch, "E1463", {"start": v(-100.56, -78.7) * mm, "end": v(-100.47, -79.6) * mm});
            skLineSegment(sketch, "E1464", {"start": v(-100.47, -79.6) * mm, "end": v(-100.54, -80.4) * mm});
            skLineSegment(sketch, "E1465", {"start": v(-100.54, -80.4) * mm, "end": v(-100.75, -81.18) * mm});
            skLineSegment(sketch, "E1466", {"start": v(-100.75, -81.18) * mm, "end": v(-101.1, -81.91) * mm});
            skLineSegment(sketch, "E1467", {"start": v(-101.1, -81.91) * mm, "end": v(-101.43, -82.41) * mm});
            skLineSegment(sketch, "E1468", {"start": v(-101.43, -82.41) * mm, "end": v(-101.82, -82.86) * mm});
            skLineSegment(sketch, "E1469", {"start": v(-101.82, -82.86) * mm, "end": v(-102.52, -83.44) * mm});
            skLineSegment(sketch, "E1470", {"start": v(-102.52, -83.44) * mm, "end": v(-103.32, -83.87) * mm});
            skLineSegment(sketch, "E1471", {"start": v(-103.32, -83.87) * mm, "end": v(-104.18, -84.13) * mm});
            skLineSegment(sketch, "E1472", {"start": v(-104.18, -84.13) * mm, "end": v(-105.08, -84.21) * mm});
            skLineSegment(sketch, "E1473", {"start": v(-232.46, -85.25) * mm, "end": v(-233.26, -85.18) * mm});
            skLineSegment(sketch, "E1474", {"start": v(-233.26, -85.18) * mm, "end": v(-234.04, -84.98) * mm});
            skLineSegment(sketch, "E1475", {"start": v(-234.04, -84.98) * mm, "end": v(-234.77, -84.64) * mm});
            skLineSegment(sketch, "E1476", {"start": v(-234.77, -84.64) * mm, "end": v(-235.27, -84.3) * mm});
            skLineSegment(sketch, "E1477", {"start": v(-235.27, -84.3) * mm, "end": v(-235.72, -83.9) * mm});
            skLineSegment(sketch, "E1478", {"start": v(-235.72, -83.9) * mm, "end": v(-236.3, -83.2) * mm});
            skLineSegment(sketch, "E1479", {"start": v(-236.3, -83.2) * mm, "end": v(-236.72, -82.4) * mm});
            skLineSegment(sketch, "E1480", {"start": v(-236.72, -82.4) * mm, "end": v(-236.98, -81.54) * mm});
            skLineSegment(sketch, "E1481", {"start": v(-236.98, -81.54) * mm, "end": v(-237.07, -80.64) * mm});
            skLineSegment(sketch, "E1482", {"start": v(-237.07, -80.64) * mm, "end": v(-237, -79.84) * mm});
            skLineSegment(sketch, "E1483", {"start": v(-237, -79.84) * mm, "end": v(-236.8, -79.07) * mm});
            skLineSegment(sketch, "E1484", {"start": v(-236.8, -79.07) * mm, "end": v(-236.45, -78.34) * mm});
            skLineSegment(sketch, "E1485", {"start": v(-236.45, -78.34) * mm, "end": v(-236.12, -77.84) * mm});
            skLineSegment(sketch, "E1486", {"start": v(-236.12, -77.84) * mm, "end": v(-235.72, -77.38) * mm});
            skLineSegment(sketch, "E1487", {"start": v(-235.72, -77.38) * mm, "end": v(-235.02, -76.8) * mm});
            skLineSegment(sketch, "E1488", {"start": v(-235.02, -76.8) * mm, "end": v(-234.23, -76.38) * mm});
            skLineSegment(sketch, "E1489", {"start": v(-234.23, -76.38) * mm, "end": v(-233.36, -76.12) * mm});
            skLineSegment(sketch, "E1490", {"start": v(-233.36, -76.12) * mm, "end": v(-232.46, -76.03) * mm});
            skLineSegment(sketch, "E1491", {"start": v(-232.46, -76.03) * mm, "end": v(-231.66, -76.1) * mm});
            skLineSegment(sketch, "E1492", {"start": v(-231.66, -76.1) * mm, "end": v(-230.89, -76.31) * mm});
            skLineSegment(sketch, "E1493", {"start": v(-230.89, -76.31) * mm, "end": v(-230.16, -76.65) * mm});
            skLineSegment(sketch, "E1494", {"start": v(-230.16, -76.65) * mm, "end": v(-229.66, -76.99) * mm});
            skLineSegment(sketch, "E1495", {"start": v(-229.66, -76.99) * mm, "end": v(-229.2, -77.38) * mm});
            skLineSegment(sketch, "E1496", {"start": v(-229.2, -77.38) * mm, "end": v(-228.63, -78.08) * mm});
            skLineSegment(sketch, "E1497", {"start": v(-228.63, -78.08) * mm, "end": v(-228.2, -78.88) * mm});
            skLineSegment(sketch, "E1498", {"start": v(-228.2, -78.88) * mm, "end": v(-227.94, -79.74) * mm});
            skLineSegment(sketch, "E1499", {"start": v(-227.94, -79.74) * mm, "end": v(-227.85, -80.64) * mm});
            skLineSegment(sketch, "E1500", {"start": v(-227.85, -80.64) * mm, "end": v(-227.92, -81.44) * mm});
            skLineSegment(sketch, "E1501", {"start": v(-227.92, -81.44) * mm, "end": v(-228.13, -82.22) * mm});
            skLineSegment(sketch, "E1502", {"start": v(-228.13, -82.22) * mm, "end": v(-228.47, -82.95) * mm});
            skLineSegment(sketch, "E1503", {"start": v(-228.47, -82.95) * mm, "end": v(-228.8, -83.45) * mm});
            skLineSegment(sketch, "E1504", {"start": v(-228.8, -83.45) * mm, "end": v(-229.2, -83.9) * mm});
            skLineSegment(sketch, "E1505", {"start": v(-229.2, -83.9) * mm, "end": v(-229.9, -84.48) * mm});
            skLineSegment(sketch, "E1506", {"start": v(-229.9, -84.48) * mm, "end": v(-230.7, -84.9) * mm});
            skLineSegment(sketch, "E1507", {"start": v(-230.7, -84.9) * mm, "end": v(-231.56, -85.17) * mm});
            skLineSegment(sketch, "E1508", {"start": v(-231.56, -85.17) * mm, "end": v(-232.46, -85.25) * mm});
            skSolve(sketch);
        }
        {
            var Q0;
            Q0=makeQuery(id+"F0.imprint","IMPRINT",FACE,{"disambiguationData":[TD([[makeQuery(id+"F0.imprint","IMPRINT",EDGE,{"derivedFrom":sQuery(id+"F0.wireOp",EDGE,"E0")}),1.0]])]});
            var Q1;
            Q1=makeQuery(id+"F0.imprint","IMPRINT",FACE,{"disambiguationData":[TD([[makeQuery(id+"F0.imprint","IMPRINT",EDGE,{"derivedFrom":sQuery(id+"F0.wireOp",EDGE,"E4")}),1.0]])]});
            var Q2;
            Q2=makeQuery(id+"F0.imprint","IMPRINT",FACE,{"disambiguationData":[TD([[makeQuery(id+"F0.imprint","IMPRINT",EDGE,{"derivedFrom":sQuery(id+"F0.wireOp",EDGE,"E164")}),1.0]])]});
            var Q3;
            Q3=makeQuery(id+"F0.imprint","IMPRINT",FACE,{"disambiguationData":[TD([[makeQuery(id+"F0.imprint","IMPRINT",EDGE,{"derivedFrom":sQuery(id+"F0.wireOp",EDGE,"E238")}),1.0]])]});
            var Q4;
            Q4=makeQuery(id+"F0.imprint","IMPRINT",FACE,{"disambiguationData":[TD([[makeQuery(id+"F0.imprint","IMPRINT",EDGE,{"derivedFrom":sQuery(id+"F0.wireOp",EDGE,"E465")}),1.0]])]});
            var Q5;
            Q5=makeQuery(id+"F0.imprint","IMPRINT",FACE,{"disambiguationData":[TD([[makeQuery(id+"F0.imprint","IMPRINT",EDGE,{"derivedFrom":sQuery(id+"F0.wireOp",EDGE,"E1357")}),1.0]])]});
            var Q6;
            Q6=makeQuery(id+"F0.imprint","IMPRINT",FACE,{"disambiguationData":[TD([[makeQuery(id+"F0.imprint","IMPRINT",EDGE,{"derivedFrom":sQuery(id+"F0.wireOp",EDGE,"E0")}),-1.0]])]});
            var Q7;
            Q7=makeQuery(id+"F0.imprint","IMPRINT",FACE,{"disambiguationData":[TD([[makeQuery(id+"F0.imprint","IMPRINT",EDGE,{"derivedFrom":sQuery(id+"F0.wireOp",EDGE,"E561")}),-1.0]])]});
            var Q8;
            Q8=makeQuery(id+"F0.imprint","IMPRINT",FACE,{"disambiguationData":[TD([[makeQuery(id+"F0.imprint","IMPRINT",EDGE,{"derivedFrom":sQuery(id+"F0.wireOp",EDGE,"E824")}),-1.0]])]});
            var Q9;
            Q9=makeQuery(id+"F0.imprint","IMPRINT",FACE,{"disambiguationData":[TD([[makeQuery(id+"F0.imprint","IMPRINT",EDGE,{"derivedFrom":sQuery(id+"F0.wireOp",EDGE,"E949")}),-1.0]])]});
            var Q10;
            Q10=makeQuery(id+"F0.imprint","IMPRINT",FACE,{"disambiguationData":[TD([[makeQuery(id+"F0.imprint","IMPRINT",EDGE,{"derivedFrom":sQuery(id+"F0.wireOp",EDGE,"E626")}),1.0]])]});
            var Q11;
            Q11=makeQuery(id+"F0.imprint","IMPRINT",FACE,{"disambiguationData":[TD([[makeQuery(id+"F0.imprint","IMPRINT",EDGE,{"derivedFrom":sQuery(id+"F0.wireOp",EDGE,"E1001")}),1.0]])]});
            var Q12;
            Q12=makeQuery(id+"F0.imprint","IMPRINT",FACE,{"disambiguationData":[TD([[makeQuery(id+"F0.imprint","IMPRINT",EDGE,{"derivedFrom":sQuery(id+"F0.wireOp",EDGE,"E764")}),-1.0]])]});
            var Q13;
            Q13=makeQuery(id+"F0.imprint","IMPRINT",FACE,{"disambiguationData":[TD([[makeQuery(id+"F0.imprint","IMPRINT",EDGE,{"derivedFrom":sQuery(id+"F0.wireOp",EDGE,"E961")}),-1.0]])]});
            var Q14;
            Q14=makeQuery(id+"F0.imprint","IMPRINT",FACE,{"disambiguationData":[TD([[makeQuery(id+"F0.imprint","IMPRINT",EDGE,{"derivedFrom":sQuery(id+"F0.wireOp",EDGE,"E804")}),1.0]])]});
            var Q15;
            Q15=makeQuery(id+"F0.imprint","IMPRINT",FACE,{"disambiguationData":[TD([[makeQuery(id+"F0.imprint","IMPRINT",EDGE,{"derivedFrom":sQuery(id+"F0.wireOp",EDGE,"E719")}),1.0]])]});
            var Q16;
            Q16=makeQuery(id+"F0.imprint","IMPRINT",FACE,{"disambiguationData":[TD([[makeQuery(id+"F0.imprint","IMPRINT",EDGE,{"derivedFrom":sQuery(id+"F0.wireOp",EDGE,"E1365")}),-1.0]])]});
            var Q17;
            Q17=makeQuery(id+"F0.imprint","IMPRINT",FACE,{"disambiguationData":[TD([[makeQuery(id+"F0.imprint","IMPRINT",EDGE,{"derivedFrom":sQuery(id+"F0.wireOp",EDGE,"E1473")}),-1.0]])]});
            var Q18;
            Q18=makeQuery(id+"F0.imprint","IMPRINT",FACE,{"disambiguationData":[TD([[makeQuery(id+"F0.imprint","IMPRINT",EDGE,{"derivedFrom":sQuery(id+"F0.wireOp",EDGE,"E1401")}),-1.0]])]});
            var Q19;
            Q19=makeQuery(id+"F0.imprint","IMPRINT",FACE,{"disambiguationData":[TD([[makeQuery(id+"F0.imprint","IMPRINT",EDGE,{"derivedFrom":sQuery(id+"F0.wireOp",EDGE,"E1437")}),-1.0]])]});
            var Q20;
            Q20=makeQuery(id+"F0.imprint","IMPRINT",FACE,{"disambiguationData":[TD([[makeQuery(id+"F0.imprint","IMPRINT",EDGE,{"derivedFrom":sQuery(id+"F0.wireOp",EDGE,"E578")}),-1.0]])]});
            var Q21;
            Q21=makeQuery(id+"F0.imprint","IMPRINT",FACE,{"disambiguationData":[TD([[makeQuery(id+"F0.imprint","IMPRINT",EDGE,{"derivedFrom":sQuery(id+"F0.wireOp",EDGE,"E832")}),-1.0]])]});
            var Q22;
            Q22=makeQuery(id+"F0.imprint","IMPRINT",FACE,{"disambiguationData":[TD([[makeQuery(id+"F0.imprint","IMPRINT",EDGE,{"derivedFrom":sQuery(id+"F0.wireOp",EDGE,"E671")}),-1.0]])]});
            var Q23;
            Q23=makeQuery(id+"F0.imprint","IMPRINT",FACE,{"disambiguationData":[TD([[makeQuery(id+"F0.imprint","IMPRINT",EDGE,{"derivedFrom":sQuery(id+"F0.wireOp",EDGE,"E1117")}),-1.0]])]});
            var Q24;
            Q24=makeQuery(id+"F0.imprint","IMPRINT",FACE,{"disambiguationData":[TD([[makeQuery(id+"F0.imprint","IMPRINT",EDGE,{"derivedFrom":sQuery(id+"F0.wireOp",EDGE,"E1133")}),-1.0]])]});
            var Q25;
            Q25=makeQuery(id+"F0.imprint","IMPRINT",FACE,{"disambiguationData":[TD([[makeQuery(id+"F0.imprint","IMPRINT",EDGE,{"derivedFrom":sQuery(id+"F0.wireOp",EDGE,"E1037")}),-1.0]])]});
            var Q26;
            Q26=makeQuery(id+"F0.imprint","IMPRINT",FACE,{"disambiguationData":[TD([[makeQuery(id+"F0.imprint","IMPRINT",EDGE,{"derivedFrom":sQuery(id+"F0.wireOp",EDGE,"E1277")}),-1.0]])]});
            var Q27;
            Q27=makeQuery(id+"F0.imprint","IMPRINT",FACE,{"disambiguationData":[TD([[makeQuery(id+"F0.imprint","IMPRINT",EDGE,{"derivedFrom":sQuery(id+"F0.wireOp",EDGE,"E1293")}),-1.0]])]});
            var Q28;
            Q28=makeQuery(id+"F0.imprint","IMPRINT",FACE,{"disambiguationData":[TD([[makeQuery(id+"F0.imprint","IMPRINT",EDGE,{"derivedFrom":sQuery(id+"F0.wireOp",EDGE,"E1069")}),-1.0]])]});
            var Q29;
            Q29=makeQuery(id+"F0.imprint","IMPRINT",FACE,{"disambiguationData":[TD([[makeQuery(id+"F0.imprint","IMPRINT",EDGE,{"derivedFrom":sQuery(id+"F0.wireOp",EDGE,"E1021")}),-1.0]])]});
            var Q30;
            Q30=makeQuery(id+"F0.imprint","IMPRINT",FACE,{"disambiguationData":[TD([[makeQuery(id+"F0.imprint","IMPRINT",EDGE,{"derivedFrom":sQuery(id+"F0.wireOp",EDGE,"E1085")}),-1.0]])]});
            var Q31;
            Q31=makeQuery(id+"F0.imprint","IMPRINT",FACE,{"disambiguationData":[TD([[makeQuery(id+"F0.imprint","IMPRINT",EDGE,{"derivedFrom":sQuery(id+"F0.wireOp",EDGE,"E1261")}),-1.0]])]});
            var Q32;
            Q32=makeQuery(id+"F0.imprint","IMPRINT",FACE,{"disambiguationData":[TD([[makeQuery(id+"F0.imprint","IMPRINT",EDGE,{"derivedFrom":sQuery(id+"F0.wireOp",EDGE,"E1325")}),-1.0]])]});
            var Q33;
            Q33=makeQuery(id+"F0.imprint","IMPRINT",FACE,{"disambiguationData":[TD([[makeQuery(id+"F0.imprint","IMPRINT",EDGE,{"derivedFrom":sQuery(id+"F0.wireOp",EDGE,"E1341")}),-1.0]])]});
            var Q34;
            Q34=makeQuery(id+"F0.imprint","IMPRINT",FACE,{"disambiguationData":[TD([[makeQuery(id+"F0.imprint","IMPRINT",EDGE,{"derivedFrom":sQuery(id+"F0.wireOp",EDGE,"E1101")}),-1.0]])]});
            var Q35;
            Q35=makeQuery(id+"F0.imprint","IMPRINT",FACE,{"disambiguationData":[TD([[makeQuery(id+"F0.imprint","IMPRINT",EDGE,{"derivedFrom":sQuery(id+"F0.wireOp",EDGE,"E1309")}),-1.0]])]});
            var Q36;
            Q36=makeQuery(id+"F0.imprint","IMPRINT",FACE,{"disambiguationData":[TD([[makeQuery(id+"F0.imprint","IMPRINT",EDGE,{"derivedFrom":sQuery(id+"F0.wireOp",EDGE,"E1053")}),-1.0]])]});
            var Q37;
            Q37=makeQuery(id+"F0.imprint","IMPRINT",FACE,{"disambiguationData":[TD([[makeQuery(id+"F0.imprint","IMPRINT",EDGE,{"derivedFrom":sQuery(id+"F0.wireOp",EDGE,"E1213")}),-1.0]])]});
            var Q38;
            Q38=makeQuery(id+"F0.imprint","IMPRINT",FACE,{"disambiguationData":[TD([[makeQuery(id+"F0.imprint","IMPRINT",EDGE,{"derivedFrom":sQuery(id+"F0.wireOp",EDGE,"E1165")}),-1.0]])]});
            var Q39;
            Q39=makeQuery(id+"F0.imprint","IMPRINT",FACE,{"disambiguationData":[TD([[makeQuery(id+"F0.imprint","IMPRINT",EDGE,{"derivedFrom":sQuery(id+"F0.wireOp",EDGE,"E1181")}),-1.0]])]});
            var Q40;
            Q40=makeQuery(id+"F0.imprint","IMPRINT",FACE,{"disambiguationData":[TD([[makeQuery(id+"F0.imprint","IMPRINT",EDGE,{"derivedFrom":sQuery(id+"F0.wireOp",EDGE,"E1197")}),-1.0]])]});
            var Q41;
            Q41=makeQuery(id+"F0.imprint","IMPRINT",FACE,{"disambiguationData":[TD([[makeQuery(id+"F0.imprint","IMPRINT",EDGE,{"derivedFrom":sQuery(id+"F0.wireOp",EDGE,"E1149")}),-1.0]])]});
            var Q42;
            Q42=makeQuery(id+"F0.imprint","IMPRINT",FACE,{"disambiguationData":[TD([[makeQuery(id+"F0.imprint","IMPRINT",EDGE,{"derivedFrom":sQuery(id+"F0.wireOp",EDGE,"E1245")}),-1.0]])]});
            var Q43;
            Q43=makeQuery(id+"F0.imprint","IMPRINT",FACE,{"disambiguationData":[TD([[makeQuery(id+"F0.imprint","IMPRINT",EDGE,{"derivedFrom":sQuery(id+"F0.wireOp",EDGE,"E1229")}),-1.0]])]});
            extrude(context, id + "F1", {"entities" : qUnion([Q0, Q1, Q2, Q3, Q4, Q5, Q6, Q7, Q8, Q9, Q10, Q11, Q12, Q13, Q14, Q15, Q16, Q17, Q18, Q19, Q20, Q21, Q22, Q23, Q24, Q25, Q26, Q27, Q28, Q29, Q30, Q31, Q32, Q33, Q34, Q35, Q36, Q37, Q38, Q39, Q40, Q41, Q42, Q43]), "depth" : 6.35 * mm, "offsetDistance" : 25.4 * mm});
        }
        {
            var Q0;
            Q0=makeQuery(id+"F0.imprint","IMPRINT",FACE,{"disambiguationData":[TD([[makeQuery(id+"F0.imprint","IMPRINT",EDGE,{"derivedFrom":sQuery(id+"F0.wireOp",EDGE,"E719")}),1.0]])]});
            var Q1;
            Q1=makeQuery(id+"F0.imprint","IMPRINT",FACE,{"disambiguationData":[TD([[makeQuery(id+"F0.imprint","IMPRINT",EDGE,{"derivedFrom":sQuery(id+"F0.wireOp",EDGE,"E626")}),1.0]])]});
            var Q2;
            Q2=makeQuery(id+"F0.imprint","IMPRINT",FACE,{"disambiguationData":[TD([[makeQuery(id+"F0.imprint","IMPRINT",EDGE,{"derivedFrom":sQuery(id+"F0.wireOp",EDGE,"E4")}),1.0]])]});
            var Q3;
            Q3=makeQuery(id+"F0.imprint","IMPRINT",FACE,{"disambiguationData":[TD([[makeQuery(id+"F0.imprint","IMPRINT",EDGE,{"derivedFrom":sQuery(id+"F0.wireOp",EDGE,"E164")}),1.0]])]});
            var Q4;
            Q4=makeQuery(id+"F0.imprint","IMPRINT",FACE,{"disambiguationData":[TD([[makeQuery(id+"F0.imprint","IMPRINT",EDGE,{"derivedFrom":sQuery(id+"F0.wireOp",EDGE,"E0")}),1.0]])]});
            var Q5;
            Q5=makeQuery(id+"F0.imprint","IMPRINT",FACE,{"disambiguationData":[TD([[makeQuery(id+"F0.imprint","IMPRINT",EDGE,{"derivedFrom":sQuery(id+"F0.wireOp",EDGE,"E0")}),-1.0]])]});
            var Q6;
            Q6=makeQuery(id+"F0.imprint","IMPRINT",FACE,{"disambiguationData":[TD([[makeQuery(id+"F0.imprint","IMPRINT",EDGE,{"derivedFrom":sQuery(id+"F0.wireOp",EDGE,"E465")}),1.0]])]});
            var Q7;
            Q7=makeQuery(id+"F0.imprint","IMPRINT",FACE,{"disambiguationData":[TD([[makeQuery(id+"F0.imprint","IMPRINT",EDGE,{"derivedFrom":sQuery(id+"F0.wireOp",EDGE,"E238")}),1.0]])]});
            var Q8;
            Q8=makeQuery(id+"F0.imprint","IMPRINT",FACE,{"disambiguationData":[TD([[makeQuery(id+"F0.imprint","IMPRINT",EDGE,{"derivedFrom":sQuery(id+"F0.wireOp",EDGE,"E804")}),1.0]])]});
            var Q9;
            Q9=makeQuery(id+"F0.imprint","IMPRINT",FACE,{"disambiguationData":[TD([[makeQuery(id+"F0.imprint","IMPRINT",EDGE,{"derivedFrom":sQuery(id+"F0.wireOp",EDGE,"E764")}),-1.0]])]});
            var Q10;
            Q10=makeQuery(id+"F0.imprint","IMPRINT",FACE,{"disambiguationData":[TD([[makeQuery(id+"F0.imprint","IMPRINT",EDGE,{"derivedFrom":sQuery(id+"F0.wireOp",EDGE,"E671")}),-1.0]])]});
            var Q11;
            Q11=makeQuery(id+"F0.imprint","IMPRINT",FACE,{"disambiguationData":[TD([[makeQuery(id+"F0.imprint","IMPRINT",EDGE,{"derivedFrom":sQuery(id+"F0.wireOp",EDGE,"E578")}),-1.0]])]});
            var Q12;
            Q12=makeQuery(id+"F0.imprint","IMPRINT",FACE,{"disambiguationData":[TD([[makeQuery(id+"F0.imprint","IMPRINT",EDGE,{"derivedFrom":sQuery(id+"F0.wireOp",EDGE,"E824")}),-1.0]])]});
            var Q13;
            Q13=makeQuery(id+"F0.imprint","IMPRINT",FACE,{"disambiguationData":[TD([[makeQuery(id+"F0.imprint","IMPRINT",EDGE,{"derivedFrom":sQuery(id+"F0.wireOp",EDGE,"E832")}),-1.0]])]});
            var Q14;
            Q14=makeQuery(id+"F0.imprint","IMPRINT",FACE,{"disambiguationData":[TD([[makeQuery(id+"F0.imprint","IMPRINT",EDGE,{"derivedFrom":sQuery(id+"F0.wireOp",EDGE,"E949")}),-1.0]])]});
            var Q15;
            Q15=makeQuery(id+"F0.imprint","IMPRINT",FACE,{"disambiguationData":[TD([[makeQuery(id+"F0.imprint","IMPRINT",EDGE,{"derivedFrom":sQuery(id+"F0.wireOp",EDGE,"E961")}),-1.0]])]});
            var Q16;
            Q16=makeQuery(id+"F0.imprint","IMPRINT",FACE,{"disambiguationData":[TD([[makeQuery(id+"F0.imprint","IMPRINT",EDGE,{"derivedFrom":sQuery(id+"F0.wireOp",EDGE,"E1001")}),1.0]])]});
            var Q17;
            Q17=makeQuery(id+"F0.imprint","IMPRINT",FACE,{"disambiguationData":[TD([[makeQuery(id+"F0.imprint","IMPRINT",EDGE,{"derivedFrom":sQuery(id+"F0.wireOp",EDGE,"E1473")}),-1.0]])]});
            var Q18;
            Q18=makeQuery(id+"F0.imprint","IMPRINT",FACE,{"disambiguationData":[TD([[makeQuery(id+"F0.imprint","IMPRINT",EDGE,{"derivedFrom":sQuery(id+"F0.wireOp",EDGE,"E1437")}),-1.0]])]});
            var Q19;
            Q19=makeQuery(id+"F0.imprint","IMPRINT",FACE,{"disambiguationData":[TD([[makeQuery(id+"F0.imprint","IMPRINT",EDGE,{"derivedFrom":sQuery(id+"F0.wireOp",EDGE,"E561")}),-1.0]])]});
            var Q20;
            Q20=makeQuery(id+"F0.imprint","IMPRINT",FACE,{"disambiguationData":[TD([[makeQuery(id+"F0.imprint","IMPRINT",EDGE,{"derivedFrom":sQuery(id+"F0.wireOp",EDGE,"E1401")}),-1.0]])]});
            var Q21;
            Q21=makeQuery(id+"F0.imprint","IMPRINT",FACE,{"disambiguationData":[TD([[makeQuery(id+"F0.imprint","IMPRINT",EDGE,{"derivedFrom":sQuery(id+"F0.wireOp",EDGE,"E1365")}),-1.0]])]});
            extrude(context, id + "F2", {"entities" : qUnion([Q0, Q1, Q2, Q3, Q4, Q5, Q6, Q7, Q8, Q9, Q10, Q11, Q12, Q13, Q14, Q15, Q16, Q17, Q18, Q19, Q20, Q21]), "depth" : 8.9 * mm, "offsetDistance" : 25.4 * mm});
        }
        {
            var Q0;
            Q0=makeQuery(id+"F0.imprint","IMPRINT",FACE,{"disambiguationData":[TD([[makeQuery(id+"F0.imprint","IMPRINT",EDGE,{"derivedFrom":sQuery(id+"F0.wireOp",EDGE,"E238")}),1.0]])]});
            var Q1;
            Q1=makeQuery(id+"F0.imprint","IMPRINT",FACE,{"disambiguationData":[TD([[makeQuery(id+"F0.imprint","IMPRINT",EDGE,{"derivedFrom":sQuery(id+"F0.wireOp",EDGE,"E465")}),1.0]])]});
            var Q2;
            Q2=makeQuery(id+"F0.imprint","IMPRINT",FACE,{"disambiguationData":[TD([[makeQuery(id+"F0.imprint","IMPRINT",EDGE,{"derivedFrom":sQuery(id+"F0.wireOp",EDGE,"E0")}),1.0]])]});
            var Q3;
            Q3=makeQuery(id+"F0.imprint","IMPRINT",FACE,{"disambiguationData":[TD([[makeQuery(id+"F0.imprint","IMPRINT",EDGE,{"derivedFrom":sQuery(id+"F0.wireOp",EDGE,"E4")}),1.0]])]});
            var Q4;
            Q4=makeQuery(id+"F0.imprint","IMPRINT",FACE,{"disambiguationData":[TD([[makeQuery(id+"F0.imprint","IMPRINT",EDGE,{"derivedFrom":sQuery(id+"F0.wireOp",EDGE,"E164")}),1.0]])]});
            var Q5;
            Q5=makeQuery(id+"F0.imprint","IMPRINT",FACE,{"disambiguationData":[TD([[makeQuery(id+"F0.imprint","IMPRINT",EDGE,{"derivedFrom":sQuery(id+"F0.wireOp",EDGE,"E961")}),-1.0]])]});
            var Q6;
            Q6=makeQuery(id+"F0.imprint","IMPRINT",FACE,{"disambiguationData":[TD([[makeQuery(id+"F0.imprint","IMPRINT",EDGE,{"derivedFrom":sQuery(id+"F0.wireOp",EDGE,"E949")}),-1.0]])]});
            var Q7;
            Q7=makeQuery(id+"F0.imprint","IMPRINT",FACE,{"disambiguationData":[TD([[makeQuery(id+"F0.imprint","IMPRINT",EDGE,{"derivedFrom":sQuery(id+"F0.wireOp",EDGE,"E832")}),-1.0]])]});
            var Q8;
            Q8=makeQuery(id+"F0.imprint","IMPRINT",FACE,{"disambiguationData":[TD([[makeQuery(id+"F0.imprint","IMPRINT",EDGE,{"derivedFrom":sQuery(id+"F0.wireOp",EDGE,"E824")}),-1.0]])]});
            var Q9;
            Q9=makeQuery(id+"F0.imprint","IMPRINT",FACE,{"disambiguationData":[TD([[makeQuery(id+"F0.imprint","IMPRINT",EDGE,{"derivedFrom":sQuery(id+"F0.wireOp",EDGE,"E764")}),-1.0]])]});
            var Q10;
            Q10=makeQuery(id+"F0.imprint","IMPRINT",FACE,{"disambiguationData":[TD([[makeQuery(id+"F0.imprint","IMPRINT",EDGE,{"derivedFrom":sQuery(id+"F0.wireOp",EDGE,"E671")}),-1.0]])]});
            var Q11;
            Q11=makeQuery(id+"F0.imprint","IMPRINT",FACE,{"disambiguationData":[TD([[makeQuery(id+"F0.imprint","IMPRINT",EDGE,{"derivedFrom":sQuery(id+"F0.wireOp",EDGE,"E578")}),-1.0]])]});
            var Q12;
            Q12=makeQuery(id+"F0.imprint","IMPRINT",FACE,{"disambiguationData":[TD([[makeQuery(id+"F0.imprint","IMPRINT",EDGE,{"derivedFrom":sQuery(id+"F0.wireOp",EDGE,"E561")}),-1.0]])]});
            extrude(context, id + "F3", {"entities" : qUnion([Q0, Q1, Q2, Q3, Q4, Q5, Q6, Q7, Q8, Q9, Q10, Q11, Q12]), "depth" : 10.16 * mm, "offsetDistance" : 25.4 * mm});
        }
    });
